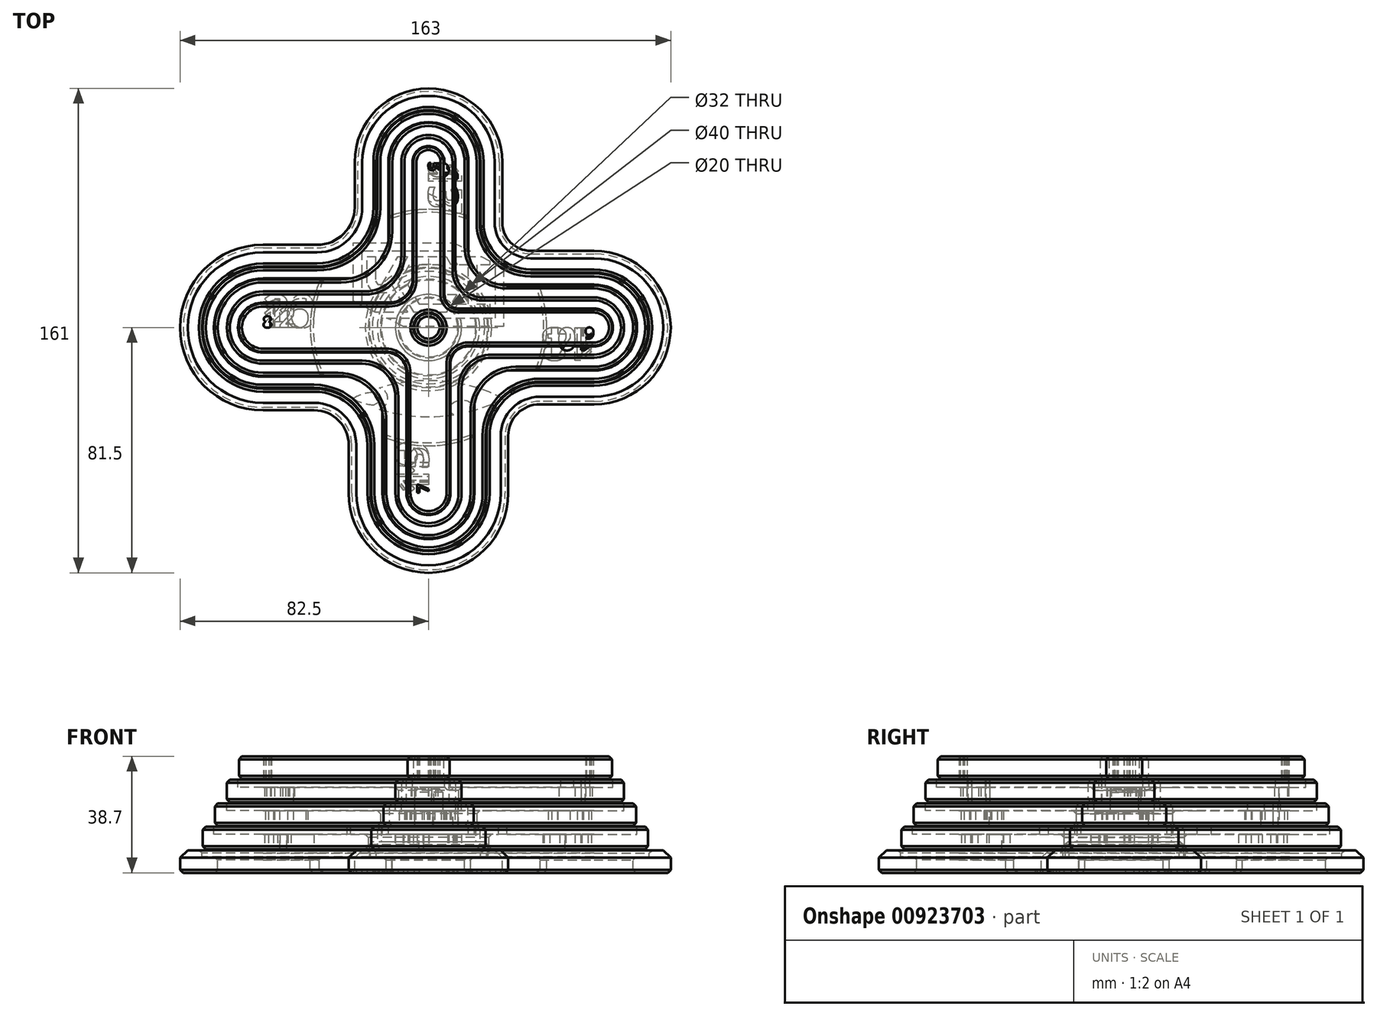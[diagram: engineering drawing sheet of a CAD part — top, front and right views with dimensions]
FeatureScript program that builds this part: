
annotation { "Feature Type Name" : "Feature", "Feature Type Description" : "" }
export const myFeature = defineFeature(function(context is Context, id is Id, definition is map)
    precondition{}
    {
        {
            assignVariable(context, id + "F0", {"name" : "x1", "anyValue" : 7.5});
        }
        {
            assignVariable(context, id + "F1", {"name" : "x2", "anyValue" : .3});
        }
        {
            assignVariable(context, id + "F2", {"name" : "x3", "anyValue" : 2.5});
        }
        {
            var Q0;
            Q0=qCreatedBy(makeId("Top.planeOp"),FACE);
            var sketch = newSketch(context, id + "F3", { "sketchPlane" : qUnion([Q0])});
            skLineSegment(sketch, "E0", {"start": v(-17, 55) * mm, "end": v(-17, 40) * mm});
            skLineSegment(sketch, "E1", {"start": v(-37, 20) * mm, "end": v(-55, 20) * mm});
            skLineSegment(sketch, "E2", {"start": v(-55, -20) * mm, "end": v(-38, -20) * mm});
            skLineSegment(sketch, "E3", {"start": v(-19, -39) * mm, "end": v(-19, -55) * mm});
            skLineSegment(sketch, "E4", {"start": v(19, -55) * mm, "end": v(19, -36) * mm});
            skLineSegment(sketch, "E5", {"start": v(37, -18) * mm, "end": v(55, -18) * mm});
            skLineSegment(sketch, "E6", {"start": v(55, 18) * mm, "end": v(34, 18) * mm});
            skLineSegment(sketch, "E7", {"start": v(17, 35) * mm, "end": v(17, 55) * mm});
            skArc(sketch, "E8", {"start": v(-55, 20) * mm, "mid": v(-75, 0) * mm, "end": v(-55, -20) * mm});
            skArc(sketch, "E9", {"start": v(-19, -55) * mm, "mid": v(0, -74) * mm, "end": v(19, -55) * mm});
            skArc(sketch, "E10", {"start": v(55, -18) * mm, "mid": v(73, 0) * mm, "end": v(55, 18) * mm});
            skArc(sketch, "E11", {"start": v(17, 55) * mm, "mid": v(0, 72) * mm, "end": v(-17, 55) * mm});
            skArc(sketch, "E12.filletArc", {"start": v(-37, 20) * mm, "mid": v(-22.86, 25.86) * mm, "end": v(-17, 40) * mm});
            skArc(sketch, "E13.filletArc", {"start": v(17, 35) * mm, "mid": v(21.98, 22.98) * mm, "end": v(34, 18) * mm});
            skArc(sketch, "E14.filletArc", {"start": v(37, -18) * mm, "mid": v(24.27, -23.27) * mm, "end": v(19, -36) * mm});
            skArc(sketch, "E15.filletArc", {"start": v(-19, -39) * mm, "mid": v(-24.56, -25.56) * mm, "end": v(-38, -20) * mm});
            skCircle(sketch, "E16", {"center": v(0, 0) * mm, "radius": 20 * mm});
            skText(sketch, "E17", { "text": "20\n", "fontName": "OpenSans-Bold.ttf"});
            skText(sketch, "E18", { "text": "19", "fontName": "OpenSans-Bold.ttf"});
            skText(sketch, "E19", { "text": "18", "fontName": "OpenSans-Bold.ttf"});
            skText(sketch, "E20", { "text": "17", "fontName": "OpenSans-Bold.ttf"});
            const initialGuessF3  = {"E17": [-0.055, 0, 1, 0, 0.01107], "E18": [0, -0.055, 0, 1, 0.01106], "E19": [0.055, 0, -1, 0, 0.01106], "E20": [0, 0.055, 0, -1, 0.01103]};
            skSetInitialGuess(sketch, initialGuessF3);
            skSolve(sketch);
        }
        {
            var Q0;
            Q0=makeQuery(id+"F3.imprint","IMPRINT",FACE,{"disambiguationData":[TD([[makeQuery(id+"F3.imprint","IMPRINT",EDGE,{"derivedFrom":sQuery(id+"F3.wireOp",EDGE,"E0")}),1.0]])]});
            extrude(context, id + "F4", {"entities" : qUnion([Q0]), "depth" : (getVariable(context, 'x1')) * mm, "offsetDistance" : 25 * mm});
        }
        {
            var Q0;
            Q0=makeQuery(id+"F4.opExtrude","CAP_FACE",FACE,{"disambiguationData":[OSD([sQuery(id+"F3.wireOp",EDGE,"E0"),sQuery(id+"F3.wireOp",EDGE,"E1"),sQuery(id+"F3.wireOp",EDGE,"E2"),sQuery(id+"F3.wireOp",EDGE,"E3"),sQuery(id+"F3.wireOp",EDGE,"E4"),sQuery(id+"F3.wireOp",EDGE,"E5"),sQuery(id+"F3.wireOp",EDGE,"E6"),sQuery(id+"F3.wireOp",EDGE,"E7"),sQuery(id+"F3.wireOp",EDGE,"E8"),sQuery(id+"F3.wireOp",EDGE,"E9"),sQuery(id+"F3.wireOp",EDGE,"E10"),sQuery(id+"F3.wireOp",EDGE,"E11"),sQuery(id+"F3.wireOp",EDGE,"E12.filletArc"),sQuery(id+"F3.wireOp",EDGE,"E13.filletArc"),sQuery(id+"F3.wireOp",EDGE,"E14.filletArc"),sQuery(id+"F3.wireOp",EDGE,"E15.filletArc"),sQuery(id+"F3.wireOp",EDGE,"E16")])],"isStart":false});
            cPlane(context, id + "F5", {"entities" : qUnion([Q0]), "cplaneType" : CPlaneType.OFFSET, "offset" : (getVariable(context, 'x2')) * mm, "width" : 150 * mm, "height" : 150 * mm});
        }
        {
            var Q0;
            Q0=qCreatedBy(id+"F5.planeOp",FACE);
            var sketch = newSketch(context, id + "F6", { "sketchPlane" : qUnion([Q0])});
            skLineSegment(sketch, "E21", {"start": v(-13, 55) * mm, "end": v(-13, 32) * mm});
            skLineSegment(sketch, "E22", {"start": v(-29, 16) * mm, "end": v(-55, 16) * mm});
            skLineSegment(sketch, "E23", {"start": v(-55, -16) * mm, "end": v(-30, -16) * mm});
            skLineSegment(sketch, "E24", {"start": v(-15, -31) * mm, "end": v(-15, -55) * mm});
            skLineSegment(sketch, "E25", {"start": v(15, -55) * mm, "end": v(15, -28) * mm});
            skLineSegment(sketch, "E26", {"start": v(29, -14) * mm, "end": v(55, -14) * mm});
            skLineSegment(sketch, "E27", {"start": v(55, 14) * mm, "end": v(26, 14) * mm});
            skLineSegment(sketch, "E28", {"start": v(13, 27) * mm, "end": v(13, 55) * mm});
            skArc(sketch, "E29", {"start": v(-55, 16) * mm, "mid": v(-71, 0) * mm, "end": v(-55, -16) * mm});
            skArc(sketch, "E30", {"start": v(-15, -55) * mm, "mid": v(0, -70) * mm, "end": v(15, -55) * mm});
            skArc(sketch, "E31", {"start": v(55, -14) * mm, "mid": v(69, 0) * mm, "end": v(55, 14) * mm});
            skArc(sketch, "E32", {"start": v(13, 55) * mm, "mid": v(0, 68) * mm, "end": v(-13, 55) * mm});
            skPoint(sketch, "E33.visualSharp", {"position": v(-13, 16) * mm});
            skArc(sketch, "E33.filletArc", {"start": v(-29, 16) * mm, "mid": v(-17.69, 20.69) * mm, "end": v(-13, 32) * mm});
            skPoint(sketch, "E34.visualSharp", {"position": v(13, 14) * mm});
            skArc(sketch, "E34.filletArc", {"start": v(13, 27) * mm, "mid": v(16.8, 17.8) * mm, "end": v(26, 14) * mm});
            skPoint(sketch, "E35.visualSharp", {"position": v(15, -14) * mm});
            skArc(sketch, "E35.filletArc", {"start": v(29, -14) * mm, "mid": v(19.1, -18.1) * mm, "end": v(15, -28) * mm});
            skPoint(sketch, "E36.visualSharp", {"position": v(-15, -16) * mm});
            skArc(sketch, "E36.filletArc", {"start": v(-15, -31) * mm, "mid": v(-19.4, -20.4) * mm, "end": v(-30, -16) * mm});
            skCircle(sketch, "E37", {"center": v(0, 0) * mm, "radius": 16 * mm});
            skText(sketch, "E38", { "text": "13\n", "fontName": "OpenSans-Bold.ttf"});
            skLineSegment(sketch, "E39", {"start": v(0, 27) * mm, "end": v(6.5, 27) * mm, "construction": true});
            skLineSegment(sketch, "E40", {"start": v(6.5, 27) * mm, "end": v(13, 27) * mm, "construction": true});
            skPoint(sketch, "E41", {"position": v(9.75, 27) * mm});
            skText(sketch, "E42", { "text": "16", "fontName": "OpenSans-Bold.ttf"});
            skText(sketch, "E43", { "text": "15", "fontName": "OpenSans-Bold.ttf"});
            skText(sketch, "E44", { "text": "14\n", "fontName": "OpenSans-Bold.ttf"});
            const initialGuessF6  = {"E38": [0, 0.055, 0, -1, 0.00975], "E42": [-0.055, 0, 1, 0, 0.0097], "E43": [0, -0.055, 0, 1, 0.0098], "E44": [0.055, 0, -1, 0, 0.00975]};
            skSetInitialGuess(sketch, initialGuessF6);
            skSolve(sketch);
        }
        {
            var Q0;
            Q0=makeQuery(id+"F6.imprint","IMPRINT",FACE,{"disambiguationData":[TD([[makeQuery(id+"F6.imprint","IMPRINT",EDGE,{"derivedFrom":sQuery(id+"F6.wireOp",EDGE,"E21")}),1.0]])]});
            extrude(context, id + "F7", {"entities" : qUnion([Q0]), "depth" : (getVariable(context, 'x1')) * mm, "offsetDistance" : 25 * mm});
        }
        {
            var Q0;
            Q0=makeQuery(id+"F7.opExtrude","CAP_FACE",FACE,{"disambiguationData":[OSD([sQuery(id+"F6.wireOp",EDGE,"E21"),sQuery(id+"F6.wireOp",EDGE,"E22"),sQuery(id+"F6.wireOp",EDGE,"E23"),sQuery(id+"F6.wireOp",EDGE,"E24"),sQuery(id+"F6.wireOp",EDGE,"E25"),sQuery(id+"F6.wireOp",EDGE,"E26"),sQuery(id+"F6.wireOp",EDGE,"E27"),sQuery(id+"F6.wireOp",EDGE,"E28"),sQuery(id+"F6.wireOp",EDGE,"E29"),sQuery(id+"F6.wireOp",EDGE,"E30"),sQuery(id+"F6.wireOp",EDGE,"E31"),sQuery(id+"F6.wireOp",EDGE,"E32"),sQuery(id+"F6.wireOp",EDGE,"E33.filletArc"),sQuery(id+"F6.wireOp",EDGE,"E34.filletArc"),sQuery(id+"F6.wireOp",EDGE,"E35.filletArc"),sQuery(id+"F6.wireOp",EDGE,"E36.filletArc"),sQuery(id+"F6.wireOp",EDGE,"E37")])],"isStart":false});
            cPlane(context, id + "F8", {"entities" : qUnion([Q0]), "cplaneType" : CPlaneType.OFFSET, "offset" : (getVariable(context, 'x2')) * mm, "width" : 150 * mm, "height" : 150 * mm});
        }
        {
            var Q0;
            Q0=qCreatedBy(id+"F8.planeOp",FACE);
            var sketch = newSketch(context, id + "F9", { "sketchPlane" : qUnion([Q0])});
            skLineSegment(sketch, "E45", {"start": v(-55, 12) * mm, "end": v(-21, 12) * mm});
            skLineSegment(sketch, "E46", {"start": v(-9, 24) * mm, "end": v(-9, 55) * mm});
            skLineSegment(sketch, "E47", {"start": v(9, 55) * mm, "end": v(9, 19) * mm});
            skLineSegment(sketch, "E48", {"start": v(18, 10) * mm, "end": v(55, 10) * mm});
            skLineSegment(sketch, "E49", {"start": v(55, -10) * mm, "end": v(21, -10) * mm});
            skLineSegment(sketch, "E50", {"start": v(11, -20) * mm, "end": v(11, -55) * mm});
            skLineSegment(sketch, "E51", {"start": v(-11, -55) * mm, "end": v(-11, -23) * mm});
            skLineSegment(sketch, "E52", {"start": v(-22, -12) * mm, "end": v(-55, -12) * mm});
            skArc(sketch, "E53", {"start": v(-55, 12) * mm, "mid": v(-67, 0) * mm, "end": v(-55, -12) * mm});
            skArc(sketch, "E54", {"start": v(9, 55) * mm, "mid": v(0, 64) * mm, "end": v(-9, 55) * mm});
            skArc(sketch, "E55", {"start": v(55, -10) * mm, "mid": v(65, 0) * mm, "end": v(55, 10) * mm});
            skArc(sketch, "E56", {"start": v(-11, -55) * mm, "mid": v(0, -66) * mm, "end": v(11, -55) * mm});
            skPoint(sketch, "E57.visualSharp", {"position": v(-9, 12) * mm});
            skArc(sketch, "E57.filletArc", {"start": v(-21, 12) * mm, "mid": v(-12.51, 15.51) * mm, "end": v(-9, 24) * mm});
            skPoint(sketch, "E58.visualSharp", {"position": v(9, 10) * mm});
            skArc(sketch, "E58.filletArc", {"start": v(9, 19) * mm, "mid": v(11.64, 12.64) * mm, "end": v(18, 10) * mm});
            skPoint(sketch, "E59.visualSharp", {"position": v(11, -10) * mm});
            skArc(sketch, "E59.filletArc", {"start": v(21, -10) * mm, "mid": v(13.93, -12.93) * mm, "end": v(11, -20) * mm});
            skPoint(sketch, "E60.visualSharp", {"position": v(-11, -12) * mm});
            skArc(sketch, "E60.filletArc", {"start": v(-11, -23) * mm, "mid": v(-14.22, -15.22) * mm, "end": v(-22, -12) * mm});
            skCircle(sketch, "E61", {"center": v(0, 0) * mm, "radius": 10 * mm});
            skText(sketch, "E62", { "text": "9\n", "fontName": "OpenSans-Bold.ttf"});
            skLineSegment(sketch, "E63", {"start": v(0, 19) * mm, "end": v(4.5, 19) * mm, "construction": true});
            skLineSegment(sketch, "E64", {"start": v(4.5, 19) * mm, "end": v(9, 19) * mm, "construction": true});
            skPoint(sketch, "E65", {"position": v(6.75, 19) * mm});
            skText(sketch, "E66", { "text": "12", "fontName": "OpenSans-Bold.ttf"});
            skText(sketch, "E67", { "text": "11\n", "fontName": "OpenSans-Bold.ttf"});
            skText(sketch, "E68", { "text": "10", "fontName": "OpenSans-Bold.ttf"});
            const initialGuessF9  = {"E62": [0, 0.055, 0, -1, 0.00675], "E66": [-0.055, 0, 1, 0, 0.00675], "E67": [0, -0.055, 0, 1, 0.00756], "E68": [0.055, 0, -1, 0, 0.00756]};
            skSetInitialGuess(sketch, initialGuessF9);
            skSolve(sketch);
        }
        {
            var Q0;
            Q0=makeQuery(id+"F9.imprint","IMPRINT",FACE,{"disambiguationData":[TD([[makeQuery(id+"F9.imprint","IMPRINT",EDGE,{"derivedFrom":sQuery(id+"F9.wireOp",EDGE,"E45")}),-1.0]])]});
            extrude(context, id + "F10", {"entities" : qUnion([Q0]), "depth" : (getVariable(context, 'x1')) * mm, "offsetDistance" : 25 * mm});
        }
        {
            var Q0;
            Q0=makeQuery(id+"F10.opExtrude","CAP_FACE",FACE,{"disambiguationData":[OSD([sQuery(id+"F9.wireOp",EDGE,"E45"),sQuery(id+"F9.wireOp",EDGE,"E46"),sQuery(id+"F9.wireOp",EDGE,"E47"),sQuery(id+"F9.wireOp",EDGE,"E48"),sQuery(id+"F9.wireOp",EDGE,"E49"),sQuery(id+"F9.wireOp",EDGE,"E50"),sQuery(id+"F9.wireOp",EDGE,"E51"),sQuery(id+"F9.wireOp",EDGE,"E52"),sQuery(id+"F9.wireOp",EDGE,"E53"),sQuery(id+"F9.wireOp",EDGE,"E54"),sQuery(id+"F9.wireOp",EDGE,"E55"),sQuery(id+"F9.wireOp",EDGE,"E56"),sQuery(id+"F9.wireOp",EDGE,"E57.filletArc"),sQuery(id+"F9.wireOp",EDGE,"E58.filletArc"),sQuery(id+"F9.wireOp",EDGE,"E59.filletArc"),sQuery(id+"F9.wireOp",EDGE,"E60.filletArc"),sQuery(id+"F9.wireOp",EDGE,"E61"),sQuery(id+"F9.wireOp",EDGE,"E62.sketch_text.stroke-0"),sQuery(id+"F9.wireOp",EDGE,"E62.sketch_text.stroke-1"),sQuery(id+"F9.wireOp",EDGE,"E62.sketch_text.stroke-2"),sQuery(id+"F9.wireOp",EDGE,"E62.sketch_text.stroke-3"),sQuery(id+"F9.wireOp",EDGE,"E62.sketch_text.stroke-4"),sQuery(id+"F9.wireOp",EDGE,"E62.sketch_text.stroke-5"),sQuery(id+"F9.wireOp",EDGE,"E62.sketch_text.stroke-6"),sQuery(id+"F9.wireOp",EDGE,"E62.sketch_text.stroke-7"),sQuery(id+"F9.wireOp",EDGE,"E62.sketch_text.stroke-8"),sQuery(id+"F9.wireOp",EDGE,"E62.sketch_text.stroke-9"),sQuery(id+"F9.wireOp",EDGE,"E62.sketch_text.stroke-10"),sQuery(id+"F9.wireOp",EDGE,"E62.sketch_text.stroke-11"),sQuery(id+"F9.wireOp",EDGE,"E62.sketch_text.stroke-12"),sQuery(id+"F9.wireOp",EDGE,"E62.sketch_text.stroke-13"),sQuery(id+"F9.wireOp",EDGE,"E62.sketch_text.stroke-14"),sQuery(id+"F9.wireOp",EDGE,"E62.sketch_text.stroke-15"),sQuery(id+"F9.wireOp",EDGE,"E62.sketch_text.stroke-16"),sQuery(id+"F9.wireOp",EDGE,"E62.sketch_text.stroke-17"),sQuery(id+"F9.wireOp",EDGE,"E66.sketch_text.stroke-0"),sQuery(id+"F9.wireOp",EDGE,"E66.sketch_text.stroke-1"),sQuery(id+"F9.wireOp",EDGE,"E66.sketch_text.stroke-2"),sQuery(id+"F9.wireOp",EDGE,"E66.sketch_text.stroke-3"),sQuery(id+"F9.wireOp",EDGE,"E66.sketch_text.stroke-4"),sQuery(id+"F9.wireOp",EDGE,"E66.sketch_text.stroke-5"),sQuery(id+"F9.wireOp",EDGE,"E66.sketch_text.stroke-6"),sQuery(id+"F9.wireOp",EDGE,"E66.sketch_text.stroke-7"),sQuery(id+"F9.wireOp",EDGE,"E66.sketch_text.stroke-8"),sQuery(id+"F9.wireOp",EDGE,"E66.sketch_text.stroke-9"),sQuery(id+"F9.wireOp",EDGE,"E66.sketch_text.stroke-10"),sQuery(id+"F9.wireOp",EDGE,"E66.sketch_text.stroke-11"),sQuery(id+"F9.wireOp",EDGE,"E66.sketch_text.stroke-12"),sQuery(id+"F9.wireOp",EDGE,"E66.sketch_text.stroke-13"),sQuery(id+"F9.wireOp",EDGE,"E66.sketch_text.stroke-14"),sQuery(id+"F9.wireOp",EDGE,"E66.sketch_text.stroke-15"),sQuery(id+"F9.wireOp",EDGE,"E66.sketch_text.stroke-16"),sQuery(id+"F9.wireOp",EDGE,"E66.sketch_text.stroke-17"),sQuery(id+"F9.wireOp",EDGE,"E66.sketch_text.stroke-18"),sQuery(id+"F9.wireOp",EDGE,"E66.sketch_text.stroke-19"),sQuery(id+"F9.wireOp",EDGE,"E66.sketch_text.stroke-20"),sQuery(id+"F9.wireOp",EDGE,"E66.sketch_text.stroke-21"),sQuery(id+"F9.wireOp",EDGE,"E66.sketch_text.stroke-22"),sQuery(id+"F9.wireOp",EDGE,"E66.sketch_text.stroke-23"),sQuery(id+"F9.wireOp",EDGE,"E66.sketch_text.stroke-24"),sQuery(id+"F9.wireOp",EDGE,"E66.sketch_text.stroke-25"),sQuery(id+"F9.wireOp",EDGE,"E66.sketch_text.stroke-26"),sQuery(id+"F9.wireOp",EDGE,"E66.sketch_text.stroke-27"),sQuery(id+"F9.wireOp",EDGE,"E66.sketch_text.stroke-28"),sQuery(id+"F9.wireOp",EDGE,"E66.sketch_text.stroke-29"),sQuery(id+"F9.wireOp",EDGE,"E66.sketch_text.stroke-30"),sQuery(id+"F9.wireOp",EDGE,"E66.sketch_text.stroke-31"),sQuery(id+"F9.wireOp",EDGE,"E66.sketch_text.stroke-32"),sQuery(id+"F9.wireOp",EDGE,"E66.sketch_text.stroke-33"),sQuery(id+"F9.wireOp",EDGE,"E67.sketch_text.stroke-0"),sQuery(id+"F9.wireOp",EDGE,"E67.sketch_text.stroke-1"),sQuery(id+"F9.wireOp",EDGE,"E67.sketch_text.stroke-2"),sQuery(id+"F9.wireOp",EDGE,"E67.sketch_text.stroke-3"),sQuery(id+"F9.wireOp",EDGE,"E67.sketch_text.stroke-4"),sQuery(id+"F9.wireOp",EDGE,"E67.sketch_text.stroke-5"),sQuery(id+"F9.wireOp",EDGE,"E67.sketch_text.stroke-6"),sQuery(id+"F9.wireOp",EDGE,"E67.sketch_text.stroke-7"),sQuery(id+"F9.wireOp",EDGE,"E67.sketch_text.stroke-8"),sQuery(id+"F9.wireOp",EDGE,"E67.sketch_text.stroke-9"),sQuery(id+"F9.wireOp",EDGE,"E67.sketch_text.stroke-10"),sQuery(id+"F9.wireOp",EDGE,"E67.sketch_text.stroke-11"),sQuery(id+"F9.wireOp",EDGE,"E67.sketch_text.stroke-12"),sQuery(id+"F9.wireOp",EDGE,"E67.sketch_text.stroke-13"),sQuery(id+"F9.wireOp",EDGE,"E67.sketch_text.stroke-14"),sQuery(id+"F9.wireOp",EDGE,"E67.sketch_text.stroke-15"),sQuery(id+"F9.wireOp",EDGE,"E67.sketch_text.stroke-16"),sQuery(id+"F9.wireOp",EDGE,"E67.sketch_text.stroke-17"),sQuery(id+"F9.wireOp",EDGE,"E67.sketch_text.stroke-18"),sQuery(id+"F9.wireOp",EDGE,"E67.sketch_text.stroke-19"),sQuery(id+"F9.wireOp",EDGE,"E68.sketch_text.stroke-0"),sQuery(id+"F9.wireOp",EDGE,"E68.sketch_text.stroke-1"),sQuery(id+"F9.wireOp",EDGE,"E68.sketch_text.stroke-2"),sQuery(id+"F9.wireOp",EDGE,"E68.sketch_text.stroke-3"),sQuery(id+"F9.wireOp",EDGE,"E68.sketch_text.stroke-4"),sQuery(id+"F9.wireOp",EDGE,"E68.sketch_text.stroke-5"),sQuery(id+"F9.wireOp",EDGE,"E68.sketch_text.stroke-6"),sQuery(id+"F9.wireOp",EDGE,"E68.sketch_text.stroke-7"),sQuery(id+"F9.wireOp",EDGE,"E68.sketch_text.stroke-8"),sQuery(id+"F9.wireOp",EDGE,"E68.sketch_text.stroke-9"),sQuery(id+"F9.wireOp",EDGE,"E68.sketch_text.stroke-10"),sQuery(id+"F9.wireOp",EDGE,"E68.sketch_text.stroke-11"),sQuery(id+"F9.wireOp",EDGE,"E68.sketch_text.stroke-12"),sQuery(id+"F9.wireOp",EDGE,"E68.sketch_text.stroke-13"),sQuery(id+"F9.wireOp",EDGE,"E68.sketch_text.stroke-14"),sQuery(id+"F9.wireOp",EDGE,"E68.sketch_text.stroke-15"),sQuery(id+"F9.wireOp",EDGE,"E68.sketch_text.stroke-16"),sQuery(id+"F9.wireOp",EDGE,"E68.sketch_text.stroke-17")])],"isStart":false});
            cPlane(context, id + "F11", {"entities" : qUnion([Q0]), "cplaneType" : CPlaneType.OFFSET, "offset" : (getVariable(context, 'x2')) * mm, "width" : 150 * mm, "height" : 150 * mm});
        }
        {
            var Q0;
            Q0=qCreatedBy(id+"F11.planeOp",FACE);
            var sketch = newSketch(context, id + "F12", { "sketchPlane" : qUnion([Q0])});
            skLineSegment(sketch, "E69", {"start": v(-5, 55) * mm, "end": v(-5, 16) * mm});
            skLineSegment(sketch, "E70", {"start": v(-13, 8) * mm, "end": v(-55, 8) * mm});
            skLineSegment(sketch, "E71", {"start": v(-55, -8) * mm, "end": v(-14, -8) * mm});
            skLineSegment(sketch, "E72", {"start": v(-7, -15) * mm, "end": v(-7, -55) * mm});
            skLineSegment(sketch, "E73", {"start": v(7, -55) * mm, "end": v(7, -12) * mm});
            skLineSegment(sketch, "E74", {"start": v(13, -6) * mm, "end": v(55, -6) * mm});
            skLineSegment(sketch, "E75", {"start": v(55, 6) * mm, "end": v(10, 6) * mm});
            skLineSegment(sketch, "E76", {"start": v(5, 11) * mm, "end": v(5, 55) * mm});
            skArc(sketch, "E77", {"start": v(-55, 8) * mm, "mid": v(-63, 0) * mm, "end": v(-55, -8) * mm});
            skArc(sketch, "E78", {"start": v(-7, -55) * mm, "mid": v(0, -62) * mm, "end": v(7, -55) * mm});
            skArc(sketch, "E79", {"start": v(55, -6) * mm, "mid": v(61, 0) * mm, "end": v(55, 6) * mm});
            skArc(sketch, "E80", {"start": v(5, 55) * mm, "mid": v(0, 60) * mm, "end": v(-5, 55) * mm});
            skPoint(sketch, "E81.visualSharp", {"position": v(-5, 8) * mm});
            skArc(sketch, "E81.filletArc", {"start": v(-13, 8) * mm, "mid": v(-7.34, 10.34) * mm, "end": v(-5, 16) * mm});
            skPoint(sketch, "E82.visualSharp", {"position": v(5, 6) * mm});
            skArc(sketch, "E82.filletArc", {"start": v(5, 11) * mm, "mid": v(6.46, 7.46) * mm, "end": v(10, 6) * mm});
            skPoint(sketch, "E83.visualSharp", {"position": v(7, -6) * mm});
            skArc(sketch, "E83.filletArc", {"start": v(13, -6) * mm, "mid": v(8.76, -7.76) * mm, "end": v(7, -12) * mm});
            skPoint(sketch, "E84.visualSharp", {"position": v(-7, -8) * mm});
            skArc(sketch, "E84.filletArc", {"start": v(-7, -15) * mm, "mid": v(-9.05, -10.05) * mm, "end": v(-14, -8) * mm});
            skCircle(sketch, "E85", {"center": v(0, 0) * mm, "radius": 5 * mm});
            skText(sketch, "E86", { "text": "5", "fontName": "OpenSans-Bold.ttf"});
            skLineSegment(sketch, "E87", {"start": v(5, 11) * mm, "end": v(2.5, 11) * mm, "construction": true});
            skLineSegment(sketch, "E88", {"start": v(2.5, 11) * mm, "end": v(0, 11) * mm, "construction": true});
            skPoint(sketch, "E89", {"position": v(3.75, 11) * mm});
            skText(sketch, "E90", { "text": "8", "fontName": "OpenSans-Bold.ttf"});
            skText(sketch, "E91", { "text": "7", "fontName": "OpenSans-Bold.ttf"});
            skText(sketch, "E92", { "text": "6", "fontName": "OpenSans-Bold.ttf"});
            const initialGuessF12  = {"E86": [0, 0.055, 0, -1, 0.00375], "E90": [-0.055, 0, 1, 0, 0.00375], "E91": [0, -0.055, 0, 1, 0.00375], "E92": [0.055, 0, -1, 0, 0.00375]};
            skSetInitialGuess(sketch, initialGuessF12);
            skSolve(sketch);
        }
        {
            var Q0;
            Q0=makeQuery(id+"F12.imprint","IMPRINT",FACE,{"disambiguationData":[TD([[makeQuery(id+"F12.imprint","IMPRINT",EDGE,{"derivedFrom":sQuery(id+"F12.wireOp",EDGE,"E69")}),1.0]])]});
            extrude(context, id + "F13", {"entities" : qUnion([Q0]), "depth" : (getVariable(context, 'x1')) * mm, "offsetDistance" : 25 * mm});
        }
        {
            var Q0;
            Q0=qCreatedBy(makeId("Top.planeOp"),FACE);
            cPlane(context, id + "F14", {"entities" : qUnion([Q0]), "cplaneType" : CPlaneType.OFFSET, "offset" : (getVariable(context, 'x2')) * mm, "oppositeDirection" : true, "width" : 150 * mm, "height" : 150 * mm});
        }
        {
            var Q0;
            Q0=qCreatedBy(id+"F14.planeOp",FACE);
            var sketch = newSketch(context, id + "F15", { "sketchPlane" : qUnion([Q0])});
            skLineSegment(sketch, "E93.0", {"start": v(46, 0) * mm, "end": v(46, -11.06) * mm});
            skLineSegment(sketch, "E93.1", {"start": v(-55, 0) * mm, "end": v(-55, 11.07) * mm});
            skCircle(sketch, "E93.3", {"center": v(0, 0) * mm, "radius": 20 * mm, "construction": true});
            skLineSegment(sketch, "E93.4", {"start": v(0, -55) * mm, "end": v(-11.06, -55) * mm});
            skLineSegment(sketch, "E93.5", {"start": v(0, 55) * mm, "end": v(0, 37) * mm});
            skArc(sketch, "E93.6", {"start": v(-19, -39) * mm, "mid": v(-19.17, -36.49) * mm, "end": v(-19.66, -34.02) * mm, "construction": true});
            skArc(sketch, "E93.7", {"start": v(17, 35) * mm, "mid": v(21.98, 22.98) * mm, "end": v(34, 18) * mm, "construction": true});
            skArc(sketch, "E93.8", {"start": v(37, -18) * mm, "mid": v(35.93, -18.03) * mm, "end": v(34.86, -18.13) * mm, "construction": true});
            skLineSegment(sketch, "E93.9", {"start": v(-17, 55) * mm, "end": v(-17, 40) * mm, "construction": true});
            skLineSegment(sketch, "E93.10", {"start": v(-37, 20) * mm, "end": v(-55, 20) * mm, "construction": true});
            skLineSegment(sketch, "E93.11", {"start": v(-55, -20) * mm, "end": v(-38, -20) * mm, "construction": true});
            skLineSegment(sketch, "E93.12", {"start": v(-19, -39) * mm, "end": v(-19, -55) * mm, "construction": true});
            skLineSegment(sketch, "E93.13", {"start": v(19, -55) * mm, "end": v(19, -36) * mm, "construction": true});
            skLineSegment(sketch, "E93.14", {"start": v(37, -18) * mm, "end": v(55, -18) * mm, "construction": true});
            skLineSegment(sketch, "E93.15", {"start": v(55, 18) * mm, "end": v(34, 18) * mm, "construction": true});
            skLineSegment(sketch, "E93.16", {"start": v(17, 35) * mm, "end": v(17, 55) * mm, "construction": true});
            skArc(sketch, "E93.17", {"start": v(-55, 20) * mm, "mid": v(-75, 0) * mm, "end": v(-55, -20) * mm, "construction": true});
            skArc(sketch, "E93.18", {"start": v(-19, -55) * mm, "mid": v(0, -74) * mm, "end": v(19, -55) * mm, "construction": true});
            skArc(sketch, "E93.19", {"start": v(55, -18) * mm, "mid": v(73, 0) * mm, "end": v(55, 18) * mm, "construction": true});
            skArc(sketch, "E93.20", {"start": v(17, 55) * mm, "mid": v(0, 72) * mm, "end": v(-17, 55) * mm, "construction": true});
            skArc(sketch, "E93.21", {"start": v(-37, 20) * mm, "mid": v(-35.32, 20.07) * mm, "end": v(-33.66, 20.28) * mm, "construction": true});
            skLineSegment(sketch, "E93.22", {"start": v(0, 55) * mm, "end": v(11.03, 55) * mm});
            skLineSegment(sketch, "E93.23", {"start": v(55, 0) * mm, "end": v(37, 0) * mm});
            skLineSegment(sketch, "E93.24", {"start": v(0, 46) * mm, "end": v(11.03, 46) * mm});
            skLineSegment(sketch, "E93.25", {"start": v(55, -11.06) * mm, "end": v(37, -11.06) * mm});
            skLineSegment(sketch, "E93.26", {"start": v(0, -46) * mm, "end": v(-11.06, -46) * mm});
            skLineSegment(sketch, "E93.28", {"start": v(55, 0) * mm, "end": v(55, -11.06) * mm});
            skLineSegment(sketch, "E93.29", {"start": v(-55, 11.07) * mm, "end": v(-37, 11.07) * mm});
            skLineSegment(sketch, "E93.30", {"start": v(0, -37) * mm, "end": v(-11.06, -37) * mm});
            skLineSegment(sketch, "E93.31", {"start": v(-37, 0) * mm, "end": v(-37, 11.07) * mm});
            skLineSegment(sketch, "E93.32", {"start": v(0, -55) * mm, "end": v(0, -37) * mm});
            skLineSegment(sketch, "E93.33", {"start": v(11.03, 55) * mm, "end": v(11.03, 37) * mm});
            skLineSegment(sketch, "E94.0", {"start": v(-37, 27.5) * mm, "end": v(-55, 27.5) * mm});
            skArc(sketch, "E94.1", {"start": v(-37, 27.5) * mm, "mid": v(-28.16, 31.16) * mm, "end": v(-24.5, 40) * mm});
            skLineSegment(sketch, "E94.2", {"start": v(-24.5, 55) * mm, "end": v(-24.5, 40) * mm});
            skArc(sketch, "E94.3", {"start": v(24.5, 55) * mm, "mid": v(0, 79.5) * mm, "end": v(-24.5, 55) * mm});
            skLineSegment(sketch, "E94.4", {"start": v(24.5, 35) * mm, "end": v(24.5, 55) * mm});
            skArc(sketch, "E94.5", {"start": v(-26.5, -55) * mm, "mid": v(0, -81.5) * mm, "end": v(26.5, -55) * mm});
            skLineSegment(sketch, "E94.6", {"start": v(-26.5, -39) * mm, "end": v(-26.5, -55) * mm});
            skArc(sketch, "E94.7", {"start": v(-26.5, -39) * mm, "mid": v(-29.87, -30.87) * mm, "end": v(-38, -27.5) * mm});
            skLineSegment(sketch, "E94.8", {"start": v(-55, -27.5) * mm, "end": v(-38, -27.5) * mm});
            skLineSegment(sketch, "E94.9", {"start": v(26.5, -55) * mm, "end": v(26.5, -36) * mm});
            skArc(sketch, "E94.10", {"start": v(37, -25.5) * mm, "mid": v(29.58, -28.58) * mm, "end": v(26.5, -36) * mm});
            skLineSegment(sketch, "E94.11", {"start": v(37, -25.5) * mm, "end": v(55, -25.5) * mm});
            skArc(sketch, "E94.12", {"start": v(55, -25.5) * mm, "mid": v(80.5, 0) * mm, "end": v(55, 25.5) * mm});
            skLineSegment(sketch, "E94.13", {"start": v(55, 25.5) * mm, "end": v(34, 25.5) * mm});
            skArc(sketch, "E94.14", {"start": v(-55, 27.5) * mm, "mid": v(-82.5, 0) * mm, "end": v(-55, -27.5) * mm});
            skArc(sketch, "E94.15", {"start": v(24.5, 35) * mm, "mid": v(27.28, 28.28) * mm, "end": v(34, 25.5) * mm});
            skArc(sketch, "E95.0", {"start": v(17, 35.43) * mm, "mid": v(-0.33, 39.3) * mm, "end": v(-17.6, 35.13) * mm});
            skArc(sketch, "E96.trimOffspring", {"start": v(-33.66, 20.28) * mm, "mid": v(-39.3, -0.15) * mm, "end": v(-33.5, -20.54) * mm});
            skArc(sketch, "E97.trimOffspring", {"start": v(-17.6, 35.13) * mm, "mid": v(-17.15, 37.55) * mm, "end": v(-17, 40) * mm, "construction": true});
            skArc(sketch, "E98.trimOffspring", {"start": v(-19.66, -34.02) * mm, "mid": v(-0.34, -39.3) * mm, "end": v(19.08, -34.36) * mm});
            skArc(sketch, "E99.trimOffspring", {"start": v(-33.5, -20.54) * mm, "mid": v(-35.73, -20.14) * mm, "end": v(-38, -20) * mm, "construction": true});
            skArc(sketch, "E100.trimOffspring", {"start": v(34.86, -18.13) * mm, "mid": v(39.3, -0.07) * mm, "end": v(34.93, 18) * mm});
            skArc(sketch, "E101.trimOffspring", {"start": v(19.08, -34.36) * mm, "mid": v(19.02, -35.18) * mm, "end": v(19, -36) * mm});
            skPoint(sketch, "E93.27.end.orphan", {"position": v(11.03, 37) * mm});
            skPoint(sketch, "E93.27.start.orphan", {"position": v(0, 37) * mm});
            skPoint(sketch, "E93.2.end.orphan", {"position": v(37, -11.06) * mm});
            skPoint(sketch, "E93.2.start.orphan", {"position": v(37, 0) * mm});
            skArc(sketch, "E102.0", {"start": v(-36.3, -15.06) * mm, "mid": v(-37.15, -15.02) * mm, "end": v(-38, -15) * mm});
            skArc(sketch, "E102.1", {"start": v(-37, 15) * mm, "mid": v(-36.66, 15) * mm, "end": v(-36.32, 15) * mm});
            skLineSegment(sketch, "E102.2", {"start": v(-37, 15) * mm, "end": v(-55, 15) * mm});
            skArc(sketch, "E102.3", {"start": v(-55, 15) * mm, "mid": v(-70, 0) * mm, "end": v(-55, -15) * mm});
            skLineSegment(sketch, "E102.4", {"start": v(-55, -15) * mm, "end": v(-38, -15) * mm});
            skArc(sketch, "E103.0", {"start": v(-14, -39) * mm, "mid": v(-14.03, -37.84) * mm, "end": v(-14.11, -36.67) * mm});
            skArc(sketch, "E103.1", {"start": v(14.1, -33.9) * mm, "mid": v(14.02, -34.95) * mm, "end": v(14, -36) * mm, "construction": true});
            skLineSegment(sketch, "E103.2", {"start": v(14, -55) * mm, "end": v(14, -36.72) * mm});
            skArc(sketch, "E103.3", {"start": v(-14, -55) * mm, "mid": v(0, -69) * mm, "end": v(14, -55) * mm});
            skLineSegment(sketch, "E103.4", {"start": v(-14, -39) * mm, "end": v(-14, -55) * mm});
            skLineSegment(sketch, "E104.0", {"start": v(55, 13) * mm, "end": v(37.08, 13) * mm});
            skArc(sketch, "E104.1", {"start": v(55, -13) * mm, "mid": v(68, 0) * mm, "end": v(55, 13) * mm});
            skLineSegment(sketch, "E104.2", {"start": v(37.08, -13) * mm, "end": v(55, -13) * mm});
            skLineSegment(sketch, "E105.0", {"start": v(12, 37.42) * mm, "end": v(12, 55) * mm});
            skArc(sketch, "E105.1", {"start": v(12, 55) * mm, "mid": v(0, 67) * mm, "end": v(-12, 55) * mm});
            skLineSegment(sketch, "E105.2", {"start": v(-12, 55) * mm, "end": v(-12, 40) * mm});
            skArc(sketch, "E105.3", {"start": v(-12.14, 37.37) * mm, "mid": v(-12.03, 38.69) * mm, "end": v(-12, 40) * mm});
            skSolve(sketch);
        }
        {
            var Q0;
            Q0 = qSketchRegion(id + "F15", true);
            extrude(context, id + "F16", {"entities" : qUnion([Q0]), "oppositeDirection" : true, "depth" : (getVariable(context, 'x1')) * mm, "offsetDistance" : 25 * mm});
        }
        {
            var Q0;
            Q0=makeQuery(id+"F3.imprint","IMPRINT",FACE,{"disambiguationData":[TD([[makeQuery(id+"F3.imprint","IMPRINT",EDGE,{"derivedFrom":sQuery(id+"F3.wireOp",EDGE,"E0")}),1.0]])]});
            var sketch = newSketch(context, id + "F17", { "sketchPlane" : qUnion([Q0])});
            skArc(sketch, "E106.0.0", {"start": v(-19, -55) * mm, "mid": v(0, -74) * mm, "end": v(19, -55) * mm});
            skLineSegment(sketch, "E106.0.1", {"start": v(19, -55) * mm, "end": v(19, -36) * mm});
            skArc(sketch, "E106.0.2", {"start": v(19, -36) * mm, "mid": v(24.27, -23.27) * mm, "end": v(37, -18) * mm});
            skLineSegment(sketch, "E106.0.3", {"start": v(37, -18) * mm, "end": v(55, -18) * mm});
            skArc(sketch, "E106.0.4", {"start": v(55, -18) * mm, "mid": v(73, 0) * mm, "end": v(55, 18) * mm});
            skLineSegment(sketch, "E106.0.5", {"start": v(55, 18) * mm, "end": v(34, 18) * mm});
            skArc(sketch, "E106.0.6", {"start": v(34, 18) * mm, "mid": v(21.98, 22.98) * mm, "end": v(17, 35) * mm});
            skLineSegment(sketch, "E106.0.7", {"start": v(17, 35) * mm, "end": v(17, 55) * mm});
            skArc(sketch, "E106.0.8", {"start": v(17, 55) * mm, "mid": v(0, 72) * mm, "end": v(-17, 55) * mm});
            skLineSegment(sketch, "E106.0.9", {"start": v(-17, 55) * mm, "end": v(-17, 40) * mm});
            skArc(sketch, "E106.0.10", {"start": v(-17, 40) * mm, "mid": v(-22.86, 25.86) * mm, "end": v(-37, 20) * mm});
            skLineSegment(sketch, "E106.0.11", {"start": v(-37, 20) * mm, "end": v(-55, 20) * mm});
            skArc(sketch, "E106.0.12", {"start": v(-55, 20) * mm, "mid": v(-75, 0) * mm, "end": v(-55, -20) * mm});
            skLineSegment(sketch, "E106.0.13", {"start": v(-55, -20) * mm, "end": v(-38, -20) * mm});
            skArc(sketch, "E106.0.14", {"start": v(-38, -20) * mm, "mid": v(-24.56, -25.56) * mm, "end": v(-19, -39) * mm});
            skLineSegment(sketch, "E106.0.15", {"start": v(-19, -39) * mm, "end": v(-19, -55) * mm});
            skLineSegment(sketch, "E107.0", {"start": v(-37, 20.3) * mm, "end": v(-55, 20.3) * mm});
            skArc(sketch, "E107.1", {"start": v(-17.3, 40) * mm, "mid": v(-23.07, 26.07) * mm, "end": v(-37, 20.3) * mm});
            skLineSegment(sketch, "E107.2", {"start": v(-17.3, 55) * mm, "end": v(-17.3, 40) * mm});
            skArc(sketch, "E107.3", {"start": v(17.3, 55) * mm, "mid": v(0, 72.3) * mm, "end": v(-17.3, 55) * mm});
            skLineSegment(sketch, "E107.4", {"start": v(17.3, 35) * mm, "end": v(17.3, 55) * mm});
            skArc(sketch, "E107.5", {"start": v(-19.3, -55) * mm, "mid": v(0, -74.3) * mm, "end": v(19.3, -55) * mm});
            skLineSegment(sketch, "E107.6", {"start": v(-19.3, -39) * mm, "end": v(-19.3, -55) * mm});
            skArc(sketch, "E107.7", {"start": v(-38, -20.3) * mm, "mid": v(-24.78, -25.78) * mm, "end": v(-19.3, -39) * mm});
            skLineSegment(sketch, "E107.8", {"start": v(-55, -20.3) * mm, "end": v(-38, -20.3) * mm});
            skLineSegment(sketch, "E107.9", {"start": v(19.3, -55) * mm, "end": v(19.3, -36) * mm});
            skArc(sketch, "E107.10", {"start": v(19.3, -36) * mm, "mid": v(24.48, -23.48) * mm, "end": v(37, -18.3) * mm});
            skLineSegment(sketch, "E107.11", {"start": v(37, -18.3) * mm, "end": v(55, -18.3) * mm});
            skArc(sketch, "E107.12", {"start": v(55, -18.3) * mm, "mid": v(73.3, 0) * mm, "end": v(55, 18.3) * mm});
            skLineSegment(sketch, "E107.13", {"start": v(55, 18.3) * mm, "end": v(34, 18.3) * mm});
            skArc(sketch, "E107.14", {"start": v(-55, 20.3) * mm, "mid": v(-75.3, 0) * mm, "end": v(-55, -20.3) * mm});
            skArc(sketch, "E107.15", {"start": v(34, 18.3) * mm, "mid": v(22.2, 23.2) * mm, "end": v(17.3, 35) * mm});
            skSolve(sketch);
        }
        {
            var Q0;
            Q0 = qSketchRegion(id + "F17", true);
            var Q1;
            Q1 = qSketchRegion(id + "F3", true);
            extrude(context, id + "F18", {"entities" : qUnion([Q0, Q1]), "operationType" : NewBodyOperationType.REMOVE, "oppositeDirection" : true, "depth" : (getVariable(context, 'x3')) * mm, "offsetDistance" : 25 * mm});
        }
        {
            var Q0;
            Q0=makeQuery(id+"F4.opExtrude","CAP_FACE",FACE,{"disambiguationData":[OSD([sQuery(id+"F3.wireOp",EDGE,"E0"),sQuery(id+"F3.wireOp",EDGE,"E1"),sQuery(id+"F3.wireOp",EDGE,"E2"),sQuery(id+"F3.wireOp",EDGE,"E3"),sQuery(id+"F3.wireOp",EDGE,"E4"),sQuery(id+"F3.wireOp",EDGE,"E5"),sQuery(id+"F3.wireOp",EDGE,"E6"),sQuery(id+"F3.wireOp",EDGE,"E7"),sQuery(id+"F3.wireOp",EDGE,"E8"),sQuery(id+"F3.wireOp",EDGE,"E9"),sQuery(id+"F3.wireOp",EDGE,"E10"),sQuery(id+"F3.wireOp",EDGE,"E11"),sQuery(id+"F3.wireOp",EDGE,"E12.filletArc"),sQuery(id+"F3.wireOp",EDGE,"E13.filletArc"),sQuery(id+"F3.wireOp",EDGE,"E14.filletArc"),sQuery(id+"F3.wireOp",EDGE,"E15.filletArc"),sQuery(id+"F3.wireOp",EDGE,"E16"),sQuery(id+"F3.wireOp",EDGE,"E17.sketch_text.stroke-0"),sQuery(id+"F3.wireOp",EDGE,"E17.sketch_text.stroke-1"),sQuery(id+"F3.wireOp",EDGE,"E17.sketch_text.stroke-2"),sQuery(id+"F3.wireOp",EDGE,"E17.sketch_text.stroke-3"),sQuery(id+"F3.wireOp",EDGE,"E17.sketch_text.stroke-4"),sQuery(id+"F3.wireOp",EDGE,"E17.sketch_text.stroke-5"),sQuery(id+"F3.wireOp",EDGE,"E17.sketch_text.stroke-6"),sQuery(id+"F3.wireOp",EDGE,"E17.sketch_text.stroke-7"),sQuery(id+"F3.wireOp",EDGE,"E17.sketch_text.stroke-8"),sQuery(id+"F3.wireOp",EDGE,"E17.sketch_text.stroke-9"),sQuery(id+"F3.wireOp",EDGE,"E17.sketch_text.stroke-10"),sQuery(id+"F3.wireOp",EDGE,"E17.sketch_text.stroke-11"),sQuery(id+"F3.wireOp",EDGE,"E17.sketch_text.stroke-12"),sQuery(id+"F3.wireOp",EDGE,"E17.sketch_text.stroke-13"),sQuery(id+"F3.wireOp",EDGE,"E17.sketch_text.stroke-14"),sQuery(id+"F3.wireOp",EDGE,"E17.sketch_text.stroke-15"),sQuery(id+"F3.wireOp",EDGE,"E17.sketch_text.stroke-16"),sQuery(id+"F3.wireOp",EDGE,"E17.sketch_text.stroke-17"),sQuery(id+"F3.wireOp",EDGE,"E17.sketch_text.stroke-18"),sQuery(id+"F3.wireOp",EDGE,"E17.sketch_text.stroke-19"),sQuery(id+"F3.wireOp",EDGE,"E17.sketch_text.stroke-20"),sQuery(id+"F3.wireOp",EDGE,"E17.sketch_text.stroke-21"),sQuery(id+"F3.wireOp",EDGE,"E17.sketch_text.stroke-22"),sQuery(id+"F3.wireOp",EDGE,"E17.sketch_text.stroke-23"),sQuery(id+"F3.wireOp",EDGE,"E17.sketch_text.stroke-24"),sQuery(id+"F3.wireOp",EDGE,"E17.sketch_text.stroke-25"),sQuery(id+"F3.wireOp",EDGE,"E17.sketch_text.stroke-26"),sQuery(id+"F3.wireOp",EDGE,"E17.sketch_text.stroke-27"),sQuery(id+"F3.wireOp",EDGE,"E17.sketch_text.stroke-28"),sQuery(id+"F3.wireOp",EDGE,"E17.sketch_text.stroke-29"),sQuery(id+"F3.wireOp",EDGE,"E17.sketch_text.stroke-30"),sQuery(id+"F3.wireOp",EDGE,"E17.sketch_text.stroke-31"),sQuery(id+"F3.wireOp",EDGE,"E18.sketch_text.stroke-0"),sQuery(id+"F3.wireOp",EDGE,"E18.sketch_text.stroke-1"),sQuery(id+"F3.wireOp",EDGE,"E18.sketch_text.stroke-2"),sQuery(id+"F3.wireOp",EDGE,"E18.sketch_text.stroke-3"),sQuery(id+"F3.wireOp",EDGE,"E18.sketch_text.stroke-4"),sQuery(id+"F3.wireOp",EDGE,"E18.sketch_text.stroke-5"),sQuery(id+"F3.wireOp",EDGE,"E18.sketch_text.stroke-6"),sQuery(id+"F3.wireOp",EDGE,"E18.sketch_text.stroke-7"),sQuery(id+"F3.wireOp",EDGE,"E18.sketch_text.stroke-8"),sQuery(id+"F3.wireOp",EDGE,"E18.sketch_text.stroke-9"),sQuery(id+"F3.wireOp",EDGE,"E18.sketch_text.stroke-10"),sQuery(id+"F3.wireOp",EDGE,"E18.sketch_text.stroke-11"),sQuery(id+"F3.wireOp",EDGE,"E18.sketch_text.stroke-12"),sQuery(id+"F3.wireOp",EDGE,"E18.sketch_text.stroke-13"),sQuery(id+"F3.wireOp",EDGE,"E18.sketch_text.stroke-14"),sQuery(id+"F3.wireOp",EDGE,"E18.sketch_text.stroke-15"),sQuery(id+"F3.wireOp",EDGE,"E18.sketch_text.stroke-16"),sQuery(id+"F3.wireOp",EDGE,"E18.sketch_text.stroke-17"),sQuery(id+"F3.wireOp",EDGE,"E18.sketch_text.stroke-18"),sQuery(id+"F3.wireOp",EDGE,"E18.sketch_text.stroke-19"),sQuery(id+"F3.wireOp",EDGE,"E18.sketch_text.stroke-20"),sQuery(id+"F3.wireOp",EDGE,"E18.sketch_text.stroke-21"),sQuery(id+"F3.wireOp",EDGE,"E18.sketch_text.stroke-22"),sQuery(id+"F3.wireOp",EDGE,"E18.sketch_text.stroke-23"),sQuery(id+"F3.wireOp",EDGE,"E18.sketch_text.stroke-24"),sQuery(id+"F3.wireOp",EDGE,"E18.sketch_text.stroke-25"),sQuery(id+"F3.wireOp",EDGE,"E18.sketch_text.stroke-26"),sQuery(id+"F3.wireOp",EDGE,"E18.sketch_text.stroke-27"),sQuery(id+"F3.wireOp",EDGE,"E19.sketch_text.stroke-0"),sQuery(id+"F3.wireOp",EDGE,"E19.sketch_text.stroke-1"),sQuery(id+"F3.wireOp",EDGE,"E19.sketch_text.stroke-2"),sQuery(id+"F3.wireOp",EDGE,"E19.sketch_text.stroke-3"),sQuery(id+"F3.wireOp",EDGE,"E19.sketch_text.stroke-4"),sQuery(id+"F3.wireOp",EDGE,"E19.sketch_text.stroke-5"),sQuery(id+"F3.wireOp",EDGE,"E19.sketch_text.stroke-6"),sQuery(id+"F3.wireOp",EDGE,"E19.sketch_text.stroke-7"),sQuery(id+"F3.wireOp",EDGE,"E19.sketch_text.stroke-8"),sQuery(id+"F3.wireOp",EDGE,"E19.sketch_text.stroke-9"),sQuery(id+"F3.wireOp",EDGE,"E19.sketch_text.stroke-10"),sQuery(id+"F3.wireOp",EDGE,"E19.sketch_text.stroke-11"),sQuery(id+"F3.wireOp",EDGE,"E19.sketch_text.stroke-12"),sQuery(id+"F3.wireOp",EDGE,"E19.sketch_text.stroke-13"),sQuery(id+"F3.wireOp",EDGE,"E19.sketch_text.stroke-14"),sQuery(id+"F3.wireOp",EDGE,"E19.sketch_text.stroke-15"),sQuery(id+"F3.wireOp",EDGE,"E19.sketch_text.stroke-16"),sQuery(id+"F3.wireOp",EDGE,"E19.sketch_text.stroke-17"),sQuery(id+"F3.wireOp",EDGE,"E19.sketch_text.stroke-18"),sQuery(id+"F3.wireOp",EDGE,"E19.sketch_text.stroke-19"),sQuery(id+"F3.wireOp",EDGE,"E19.sketch_text.stroke-20"),sQuery(id+"F3.wireOp",EDGE,"E19.sketch_text.stroke-21"),sQuery(id+"F3.wireOp",EDGE,"E19.sketch_text.stroke-22"),sQuery(id+"F3.wireOp",EDGE,"E19.sketch_text.stroke-23"),sQuery(id+"F3.wireOp",EDGE,"E19.sketch_text.stroke-24"),sQuery(id+"F3.wireOp",EDGE,"E19.sketch_text.stroke-25"),sQuery(id+"F3.wireOp",EDGE,"E20.sketch_text.stroke-0"),sQuery(id+"F3.wireOp",EDGE,"E20.sketch_text.stroke-1"),sQuery(id+"F3.wireOp",EDGE,"E20.sketch_text.stroke-2"),sQuery(id+"F3.wireOp",EDGE,"E20.sketch_text.stroke-3"),sQuery(id+"F3.wireOp",EDGE,"E20.sketch_text.stroke-4"),sQuery(id+"F3.wireOp",EDGE,"E20.sketch_text.stroke-5"),sQuery(id+"F3.wireOp",EDGE,"E20.sketch_text.stroke-6"),sQuery(id+"F3.wireOp",EDGE,"E20.sketch_text.stroke-7"),sQuery(id+"F3.wireOp",EDGE,"E20.sketch_text.stroke-8"),sQuery(id+"F3.wireOp",EDGE,"E20.sketch_text.stroke-9"),sQuery(id+"F3.wireOp",EDGE,"E20.sketch_text.stroke-10"),sQuery(id+"F3.wireOp",EDGE,"E20.sketch_text.stroke-11"),sQuery(id+"F3.wireOp",EDGE,"E20.sketch_text.stroke-12"),sQuery(id+"F3.wireOp",EDGE,"E20.sketch_text.stroke-13"),sQuery(id+"F3.wireOp",EDGE,"E20.sketch_text.stroke-14"),sQuery(id+"F3.wireOp",EDGE,"E20.sketch_text.stroke-15"),sQuery(id+"F3.wireOp",EDGE,"E20.sketch_text.stroke-16")])],"isStart":false});
            var sketch = newSketch(context, id + "F19", { "sketchPlane" : qUnion([Q0])});
            skArc(sketch, "E108.0.0", {"start": v(-15, -55) * mm, "mid": v(0, -70) * mm, "end": v(15, -55) * mm});
            skLineSegment(sketch, "E108.0.1", {"start": v(15, -55) * mm, "end": v(15, -28) * mm});
            skArc(sketch, "E108.0.2", {"start": v(15, -28) * mm, "mid": v(19.1, -18.1) * mm, "end": v(29, -14) * mm});
            skLineSegment(sketch, "E108.0.3", {"start": v(29, -14) * mm, "end": v(55, -14) * mm});
            skArc(sketch, "E108.0.4", {"start": v(55, -14) * mm, "mid": v(69, 0) * mm, "end": v(55, 14) * mm});
            skLineSegment(sketch, "E108.0.5", {"start": v(55, 14) * mm, "end": v(26, 14) * mm});
            skArc(sketch, "E108.0.6", {"start": v(26, 14) * mm, "mid": v(16.8, 17.8) * mm, "end": v(13, 27) * mm});
            skLineSegment(sketch, "E108.0.7", {"start": v(13, 27) * mm, "end": v(13, 55) * mm});
            skArc(sketch, "E108.0.8", {"start": v(13, 55) * mm, "mid": v(0, 68) * mm, "end": v(-13, 55) * mm});
            skLineSegment(sketch, "E108.0.9", {"start": v(-13, 55) * mm, "end": v(-13, 32) * mm});
            skArc(sketch, "E108.0.10", {"start": v(-13, 32) * mm, "mid": v(-17.69, 20.69) * mm, "end": v(-29, 16) * mm});
            skLineSegment(sketch, "E108.0.11", {"start": v(-29, 16) * mm, "end": v(-55, 16) * mm});
            skArc(sketch, "E108.0.12", {"start": v(-55, 16) * mm, "mid": v(-71, 0) * mm, "end": v(-55, -16) * mm});
            skLineSegment(sketch, "E108.0.13", {"start": v(-55, -16) * mm, "end": v(-30, -16) * mm});
            skArc(sketch, "E108.0.14", {"start": v(-30, -16) * mm, "mid": v(-19.4, -20.4) * mm, "end": v(-15, -31) * mm});
            skLineSegment(sketch, "E108.0.15", {"start": v(-15, -31) * mm, "end": v(-15, -55) * mm});
            skLineSegment(sketch, "E109.0", {"start": v(-13.3, 16.3) * mm, "end": v(-55, 16.3) * mm});
            skLineSegment(sketch, "E109.1", {"start": v(15.3, -55) * mm, "end": v(15.3, -14.3) * mm});
            skArc(sketch, "E109.2", {"start": v(-15.3, -55) * mm, "mid": v(0, -70.3) * mm, "end": v(15.3, -55) * mm});
            skLineSegment(sketch, "E109.3", {"start": v(-15.3, -16.3) * mm, "end": v(-15.3, -55) * mm});
            skLineSegment(sketch, "E109.4", {"start": v(-55, -16.3) * mm, "end": v(-15.3, -16.3) * mm});
            skLineSegment(sketch, "E109.5", {"start": v(15.3, -14.3) * mm, "end": v(55, -14.3) * mm});
            skArc(sketch, "E109.6", {"start": v(-55, 16.3) * mm, "mid": v(-71.3, 0) * mm, "end": v(-55, -16.3) * mm});
            skArc(sketch, "E109.7", {"start": v(55, -14.3) * mm, "mid": v(69.3, 0) * mm, "end": v(55, 14.3) * mm});
            skLineSegment(sketch, "E109.8", {"start": v(55, 14.3) * mm, "end": v(13.3, 14.3) * mm});
            skLineSegment(sketch, "E109.9", {"start": v(13.3, 14.3) * mm, "end": v(13.3, 55) * mm});
            skArc(sketch, "E109.10", {"start": v(13.3, 55) * mm, "mid": v(0, 68.3) * mm, "end": v(-13.3, 55) * mm});
            skLineSegment(sketch, "E109.11", {"start": v(-13.3, 55) * mm, "end": v(-13.3, 16.3) * mm});
            skSolve(sketch);
        }
        {
            var Q0;
            Q0 = qSketchRegion(id + "F19", true);
            var Q1;
            Q1 = qSketchRegion(id + "F6", true);
            extrude(context, id + "F20", {"entities" : qUnion([Q0, Q1]), "operationType" : NewBodyOperationType.REMOVE, "oppositeDirection" : true, "depth" : (getVariable(context, 'x3')) * mm, "offsetDistance" : 25 * mm});
        }
        {
            var Q0;
            Q0=makeQuery(id+"F7.opExtrude","CAP_FACE",FACE,{"disambiguationData":[OSD([sQuery(id+"F6.wireOp",EDGE,"E21"),sQuery(id+"F6.wireOp",EDGE,"E22"),sQuery(id+"F6.wireOp",EDGE,"E23"),sQuery(id+"F6.wireOp",EDGE,"E24"),sQuery(id+"F6.wireOp",EDGE,"E25"),sQuery(id+"F6.wireOp",EDGE,"E26"),sQuery(id+"F6.wireOp",EDGE,"E27"),sQuery(id+"F6.wireOp",EDGE,"E28"),sQuery(id+"F6.wireOp",EDGE,"E29"),sQuery(id+"F6.wireOp",EDGE,"E30"),sQuery(id+"F6.wireOp",EDGE,"E31"),sQuery(id+"F6.wireOp",EDGE,"E32"),sQuery(id+"F6.wireOp",EDGE,"E33.filletArc"),sQuery(id+"F6.wireOp",EDGE,"E34.filletArc"),sQuery(id+"F6.wireOp",EDGE,"E35.filletArc"),sQuery(id+"F6.wireOp",EDGE,"E36.filletArc"),sQuery(id+"F6.wireOp",EDGE,"E37"),sQuery(id+"F6.wireOp",EDGE,"E38.sketch_text.stroke-0"),sQuery(id+"F6.wireOp",EDGE,"E38.sketch_text.stroke-1"),sQuery(id+"F6.wireOp",EDGE,"E38.sketch_text.stroke-2"),sQuery(id+"F6.wireOp",EDGE,"E38.sketch_text.stroke-3"),sQuery(id+"F6.wireOp",EDGE,"E38.sketch_text.stroke-4"),sQuery(id+"F6.wireOp",EDGE,"E38.sketch_text.stroke-5"),sQuery(id+"F6.wireOp",EDGE,"E38.sketch_text.stroke-6"),sQuery(id+"F6.wireOp",EDGE,"E38.sketch_text.stroke-7"),sQuery(id+"F6.wireOp",EDGE,"E38.sketch_text.stroke-8"),sQuery(id+"F6.wireOp",EDGE,"E38.sketch_text.stroke-9"),sQuery(id+"F6.wireOp",EDGE,"E38.sketch_text.stroke-10"),sQuery(id+"F6.wireOp",EDGE,"E38.sketch_text.stroke-11"),sQuery(id+"F6.wireOp",EDGE,"E38.sketch_text.stroke-12"),sQuery(id+"F6.wireOp",EDGE,"E38.sketch_text.stroke-13"),sQuery(id+"F6.wireOp",EDGE,"E38.sketch_text.stroke-14"),sQuery(id+"F6.wireOp",EDGE,"E38.sketch_text.stroke-15"),sQuery(id+"F6.wireOp",EDGE,"E38.sketch_text.stroke-16"),sQuery(id+"F6.wireOp",EDGE,"E38.sketch_text.stroke-17"),sQuery(id+"F6.wireOp",EDGE,"E38.sketch_text.stroke-18"),sQuery(id+"F6.wireOp",EDGE,"E38.sketch_text.stroke-19"),sQuery(id+"F6.wireOp",EDGE,"E38.sketch_text.stroke-20"),sQuery(id+"F6.wireOp",EDGE,"E38.sketch_text.stroke-21"),sQuery(id+"F6.wireOp",EDGE,"E38.sketch_text.stroke-22"),sQuery(id+"F6.wireOp",EDGE,"E38.sketch_text.stroke-23"),sQuery(id+"F6.wireOp",EDGE,"E38.sketch_text.stroke-24"),sQuery(id+"F6.wireOp",EDGE,"E38.sketch_text.stroke-25"),sQuery(id+"F6.wireOp",EDGE,"E38.sketch_text.stroke-26"),sQuery(id+"F6.wireOp",EDGE,"E38.sketch_text.stroke-27"),sQuery(id+"F6.wireOp",EDGE,"E38.sketch_text.stroke-28"),sQuery(id+"F6.wireOp",EDGE,"E38.sketch_text.stroke-29"),sQuery(id+"F6.wireOp",EDGE,"E38.sketch_text.stroke-30"),sQuery(id+"F6.wireOp",EDGE,"E38.sketch_text.stroke-31"),sQuery(id+"F6.wireOp",EDGE,"E38.sketch_text.stroke-32"),sQuery(id+"F6.wireOp",EDGE,"E38.sketch_text.stroke-33"),sQuery(id+"F6.wireOp",EDGE,"E38.sketch_text.stroke-34"),sQuery(id+"F6.wireOp",EDGE,"E38.sketch_text.stroke-35"),sQuery(id+"F6.wireOp",EDGE,"E38.sketch_text.stroke-36"),sQuery(id+"F6.wireOp",EDGE,"E42.sketch_text.stroke-0"),sQuery(id+"F6.wireOp",EDGE,"E42.sketch_text.stroke-1"),sQuery(id+"F6.wireOp",EDGE,"E42.sketch_text.stroke-2"),sQuery(id+"F6.wireOp",EDGE,"E42.sketch_text.stroke-3"),sQuery(id+"F6.wireOp",EDGE,"E42.sketch_text.stroke-4"),sQuery(id+"F6.wireOp",EDGE,"E42.sketch_text.stroke-5"),sQuery(id+"F6.wireOp",EDGE,"E42.sketch_text.stroke-6"),sQuery(id+"F6.wireOp",EDGE,"E42.sketch_text.stroke-7"),sQuery(id+"F6.wireOp",EDGE,"E42.sketch_text.stroke-8"),sQuery(id+"F6.wireOp",EDGE,"E42.sketch_text.stroke-9"),sQuery(id+"F6.wireOp",EDGE,"E42.sketch_text.stroke-10"),sQuery(id+"F6.wireOp",EDGE,"E42.sketch_text.stroke-11"),sQuery(id+"F6.wireOp",EDGE,"E42.sketch_text.stroke-12"),sQuery(id+"F6.wireOp",EDGE,"E42.sketch_text.stroke-13"),sQuery(id+"F6.wireOp",EDGE,"E42.sketch_text.stroke-14"),sQuery(id+"F6.wireOp",EDGE,"E42.sketch_text.stroke-15"),sQuery(id+"F6.wireOp",EDGE,"E42.sketch_text.stroke-16"),sQuery(id+"F6.wireOp",EDGE,"E42.sketch_text.stroke-17"),sQuery(id+"F6.wireOp",EDGE,"E42.sketch_text.stroke-18"),sQuery(id+"F6.wireOp",EDGE,"E42.sketch_text.stroke-19"),sQuery(id+"F6.wireOp",EDGE,"E42.sketch_text.stroke-20"),sQuery(id+"F6.wireOp",EDGE,"E42.sketch_text.stroke-21"),sQuery(id+"F6.wireOp",EDGE,"E42.sketch_text.stroke-22"),sQuery(id+"F6.wireOp",EDGE,"E42.sketch_text.stroke-23"),sQuery(id+"F6.wireOp",EDGE,"E42.sketch_text.stroke-24"),sQuery(id+"F6.wireOp",EDGE,"E42.sketch_text.stroke-25"),sQuery(id+"F6.wireOp",EDGE,"E42.sketch_text.stroke-26"),sQuery(id+"F6.wireOp",EDGE,"E43.sketch_text.stroke-0"),sQuery(id+"F6.wireOp",EDGE,"E43.sketch_text.stroke-1"),sQuery(id+"F6.wireOp",EDGE,"E43.sketch_text.stroke-2"),sQuery(id+"F6.wireOp",EDGE,"E43.sketch_text.stroke-3"),sQuery(id+"F6.wireOp",EDGE,"E43.sketch_text.stroke-4"),sQuery(id+"F6.wireOp",EDGE,"E43.sketch_text.stroke-5"),sQuery(id+"F6.wireOp",EDGE,"E43.sketch_text.stroke-6"),sQuery(id+"F6.wireOp",EDGE,"E43.sketch_text.stroke-7"),sQuery(id+"F6.wireOp",EDGE,"E43.sketch_text.stroke-8"),sQuery(id+"F6.wireOp",EDGE,"E43.sketch_text.stroke-9"),sQuery(id+"F6.wireOp",EDGE,"E43.sketch_text.stroke-10"),sQuery(id+"F6.wireOp",EDGE,"E43.sketch_text.stroke-11"),sQuery(id+"F6.wireOp",EDGE,"E43.sketch_text.stroke-12"),sQuery(id+"F6.wireOp",EDGE,"E43.sketch_text.stroke-13"),sQuery(id+"F6.wireOp",EDGE,"E43.sketch_text.stroke-14"),sQuery(id+"F6.wireOp",EDGE,"E43.sketch_text.stroke-15"),sQuery(id+"F6.wireOp",EDGE,"E43.sketch_text.stroke-16"),sQuery(id+"F6.wireOp",EDGE,"E43.sketch_text.stroke-17"),sQuery(id+"F6.wireOp",EDGE,"E43.sketch_text.stroke-18"),sQuery(id+"F6.wireOp",EDGE,"E43.sketch_text.stroke-19"),sQuery(id+"F6.wireOp",EDGE,"E43.sketch_text.stroke-20"),sQuery(id+"F6.wireOp",EDGE,"E43.sketch_text.stroke-21"),sQuery(id+"F6.wireOp",EDGE,"E43.sketch_text.stroke-22"),sQuery(id+"F6.wireOp",EDGE,"E43.sketch_text.stroke-23"),sQuery(id+"F6.wireOp",EDGE,"E43.sketch_text.stroke-24"),sQuery(id+"F6.wireOp",EDGE,"E43.sketch_text.stroke-25"),sQuery(id+"F6.wireOp",EDGE,"E43.sketch_text.stroke-26"),sQuery(id+"F6.wireOp",EDGE,"E43.sketch_text.stroke-27"),sQuery(id+"F6.wireOp",EDGE,"E43.sketch_text.stroke-28"),sQuery(id+"F6.wireOp",EDGE,"E43.sketch_text.stroke-29"),sQuery(id+"F6.wireOp",EDGE,"E44.sketch_text.stroke-0"),sQuery(id+"F6.wireOp",EDGE,"E44.sketch_text.stroke-1"),sQuery(id+"F6.wireOp",EDGE,"E44.sketch_text.stroke-2"),sQuery(id+"F6.wireOp",EDGE,"E44.sketch_text.stroke-3"),sQuery(id+"F6.wireOp",EDGE,"E44.sketch_text.stroke-4"),sQuery(id+"F6.wireOp",EDGE,"E44.sketch_text.stroke-5"),sQuery(id+"F6.wireOp",EDGE,"E44.sketch_text.stroke-6"),sQuery(id+"F6.wireOp",EDGE,"E44.sketch_text.stroke-7"),sQuery(id+"F6.wireOp",EDGE,"E44.sketch_text.stroke-8"),sQuery(id+"F6.wireOp",EDGE,"E44.sketch_text.stroke-9"),sQuery(id+"F6.wireOp",EDGE,"E44.sketch_text.stroke-10"),sQuery(id+"F6.wireOp",EDGE,"E44.sketch_text.stroke-11"),sQuery(id+"F6.wireOp",EDGE,"E44.sketch_text.stroke-12"),sQuery(id+"F6.wireOp",EDGE,"E44.sketch_text.stroke-13"),sQuery(id+"F6.wireOp",EDGE,"E44.sketch_text.stroke-14"),sQuery(id+"F6.wireOp",EDGE,"E44.sketch_text.stroke-15"),sQuery(id+"F6.wireOp",EDGE,"E44.sketch_text.stroke-16"),sQuery(id+"F6.wireOp",EDGE,"E44.sketch_text.stroke-17"),sQuery(id+"F6.wireOp",EDGE,"E44.sketch_text.stroke-18"),sQuery(id+"F6.wireOp",EDGE,"E44.sketch_text.stroke-19"),sQuery(id+"F6.wireOp",EDGE,"E44.sketch_text.stroke-20")])],"isStart":false});
            var sketch = newSketch(context, id + "F21", { "sketchPlane" : qUnion([Q0])});
            skLineSegment(sketch, "E110.0", {"start": v(11, -20) * mm, "end": v(11, -55) * mm});
            skArc(sketch, "E111.0", {"start": v(-11, -55) * mm, "mid": v(0, -66) * mm, "end": v(11, -55) * mm});
            skLineSegment(sketch, "E112.0", {"start": v(-11, -55) * mm, "end": v(-11, -23) * mm});
            skArc(sketch, "E113.0", {"start": v(-11, -23) * mm, "mid": v(-14.22, -15.22) * mm, "end": v(-22, -12) * mm});
            skLineSegment(sketch, "E114.0", {"start": v(-22, -12) * mm, "end": v(-55, -12) * mm});
            skArc(sketch, "E115.0", {"start": v(-55, 12) * mm, "mid": v(-67, 0) * mm, "end": v(-55, -12) * mm});
            skLineSegment(sketch, "E116.0", {"start": v(-55, 12) * mm, "end": v(-21, 12) * mm});
            skArc(sketch, "E117.0", {"start": v(-21, 12) * mm, "mid": v(-12.51, 15.51) * mm, "end": v(-9, 24) * mm});
            skLineSegment(sketch, "E117.1", {"start": v(-9, 24) * mm, "end": v(-9, 55) * mm});
            skLineSegment(sketch, "E117.2", {"start": v(9, 55) * mm, "end": v(9, 19) * mm});
            skArc(sketch, "E117.3", {"start": v(9, 55) * mm, "mid": v(0, 64) * mm, "end": v(-9, 55) * mm});
            skLineSegment(sketch, "E117.4", {"start": v(18, 10) * mm, "end": v(55, 10) * mm});
            skArc(sketch, "E117.5", {"start": v(9, 19) * mm, "mid": v(11.64, 12.64) * mm, "end": v(18, 10) * mm});
            skArc(sketch, "E117.6", {"start": v(55, -10) * mm, "mid": v(65, 0) * mm, "end": v(55, 10) * mm});
            skLineSegment(sketch, "E117.7", {"start": v(55, -10) * mm, "end": v(21, -10) * mm});
            skArc(sketch, "E117.8", {"start": v(21, -10) * mm, "mid": v(13.93, -12.93) * mm, "end": v(11, -20) * mm});
            skSolve(sketch);
        }
        {
            var Q0;
            Q0 = qSketchRegion(id + "F21", true);
            var Q1;
            Q1=makeQuery(id+"F9.imprint","IMPRINT",FACE,{"disambiguationData":[TD([[makeQuery(id+"F9.imprint","IMPRINT",EDGE,{"derivedFrom":sQuery(id+"F9.wireOp",EDGE,"E45")}),-1.0]])]});
            extrude(context, id + "F22", {"entities" : qUnion([Q0, Q1]), "operationType" : NewBodyOperationType.REMOVE, "oppositeDirection" : true, "depth" : (getVariable(context, 'x3')) * mm, "offsetDistance" : 25 * mm});
        }
        {
            var Q0;
            Q0=makeQuery(id+"F21.imprint","IMPRINT",FACE,{"disambiguationData":[TD([[makeQuery(id+"F21.imprint","IMPRINT",EDGE,{"derivedFrom":sQuery(id+"F21.wireOp",EDGE,"E110.0")}),1.0]])]});
            var sketch = newSketch(context, id + "F23", { "sketchPlane" : qUnion([Q0])});
            skArc(sketch, "E118.0", {"start": v(-55, 12) * mm, "mid": v(-67, 0) * mm, "end": v(-55, -12) * mm});
            skLineSegment(sketch, "E119.0", {"start": v(-55, 12) * mm, "end": v(-21, 12) * mm});
            skArc(sketch, "E120.0", {"start": v(-21, 12) * mm, "mid": v(-12.51, 15.51) * mm, "end": v(-9, 24) * mm});
            skLineSegment(sketch, "E121.0", {"start": v(-9, 24) * mm, "end": v(-9, 55) * mm});
            skArc(sketch, "E122.0", {"start": v(9, 55) * mm, "mid": v(0, 64) * mm, "end": v(-9, 55) * mm});
            skLineSegment(sketch, "E123.0", {"start": v(9, 55) * mm, "end": v(9, 19) * mm});
            skArc(sketch, "E124.0", {"start": v(9, 19) * mm, "mid": v(11.64, 12.64) * mm, "end": v(18, 10) * mm});
            skLineSegment(sketch, "E125.0", {"start": v(18, 10) * mm, "end": v(55, 10) * mm});
            skArc(sketch, "E126.0", {"start": v(55, -10) * mm, "mid": v(65, 0) * mm, "end": v(55, 10) * mm});
            skLineSegment(sketch, "E127.0", {"start": v(55, -10) * mm, "end": v(21, -10) * mm});
            skArc(sketch, "E128.0", {"start": v(21, -10) * mm, "mid": v(13.93, -12.93) * mm, "end": v(11, -20) * mm});
            skLineSegment(sketch, "E129.0", {"start": v(11, -20) * mm, "end": v(11, -55) * mm});
            skArc(sketch, "E130.0", {"start": v(-11, -55) * mm, "mid": v(0, -66) * mm, "end": v(11, -55) * mm});
            skLineSegment(sketch, "E131.0", {"start": v(-11, -55) * mm, "end": v(-11, -23) * mm});
            skArc(sketch, "E132.0", {"start": v(-11, -23) * mm, "mid": v(-14.22, -15.22) * mm, "end": v(-22, -12) * mm});
            skLineSegment(sketch, "E133.0", {"start": v(-22, -12) * mm, "end": v(-55, -12) * mm});
            skLineSegment(sketch, "E134.0", {"start": v(-55, 12.3) * mm, "end": v(-21, 12.3) * mm});
            skArc(sketch, "E134.1", {"start": v(-55, 12.3) * mm, "mid": v(-67.3, 0) * mm, "end": v(-55, -12.3) * mm});
            skLineSegment(sketch, "E134.2", {"start": v(-22, -12.3) * mm, "end": v(-55, -12.3) * mm});
            skArc(sketch, "E134.3", {"start": v(-11.3, -23) * mm, "mid": v(-14.43, -15.43) * mm, "end": v(-22, -12.3) * mm});
            skLineSegment(sketch, "E134.4", {"start": v(-11.3, -55) * mm, "end": v(-11.3, -23) * mm});
            skArc(sketch, "E134.5", {"start": v(9.3, 19) * mm, "mid": v(11.85, 12.85) * mm, "end": v(18, 10.3) * mm});
            skLineSegment(sketch, "E134.6", {"start": v(9.3, 55) * mm, "end": v(9.3, 19) * mm});
            skArc(sketch, "E134.7", {"start": v(9.3, 55) * mm, "mid": v(0, 64.3) * mm, "end": v(-9.3, 55) * mm});
            skLineSegment(sketch, "E134.8", {"start": v(-9.3, 24) * mm, "end": v(-9.3, 55) * mm});
            skLineSegment(sketch, "E134.9", {"start": v(18, 10.3) * mm, "end": v(55, 10.3) * mm});
            skArc(sketch, "E134.10", {"start": v(55, -10.3) * mm, "mid": v(65.3, 0) * mm, "end": v(55, 10.3) * mm});
            skLineSegment(sketch, "E134.11", {"start": v(55, -10.3) * mm, "end": v(21, -10.3) * mm});
            skArc(sketch, "E134.12", {"start": v(21, -10.3) * mm, "mid": v(14.14, -13.14) * mm, "end": v(11.3, -20) * mm});
            skLineSegment(sketch, "E134.13", {"start": v(11.3, -20) * mm, "end": v(11.3, -55) * mm});
            skArc(sketch, "E134.14", {"start": v(-21, 12.3) * mm, "mid": v(-12.73, 15.73) * mm, "end": v(-9.3, 24) * mm});
            skArc(sketch, "E134.15", {"start": v(-11.3, -55) * mm, "mid": v(0, -66.3) * mm, "end": v(11.3, -55) * mm});
            skSolve(sketch);
        }
        {
            var Q0;
            Q0=makeQuery(id+"F23.imprint","IMPRINT",FACE,{"disambiguationData":[TD([[makeQuery(id+"F23.imprint","IMPRINT",EDGE,{"derivedFrom":sQuery(id+"F23.wireOp",EDGE,"E118.0")}),-1.0]])]});
            var Q1;
            Q1=makeQuery(id+"F22.boolean.opBoolean","COPY",FACE,{"derivedFrom":makeQuery(id+"F22.opExtrude","CAP_FACE",FACE,{"disambiguationData":[OSD([sQuery(id+"F21.wireOp",EDGE,"E110.0"),sQuery(id+"F21.wireOp",EDGE,"E111.0"),sQuery(id+"F21.wireOp",EDGE,"E112.0"),sQuery(id+"F21.wireOp",EDGE,"E113.0"),sQuery(id+"F21.wireOp",EDGE,"E114.0"),sQuery(id+"F21.wireOp",EDGE,"E115.0"),sQuery(id+"F21.wireOp",EDGE,"E116.0"),sQuery(id+"F21.wireOp",EDGE,"E117.0"),sQuery(id+"F21.wireOp",EDGE,"E117.1"),sQuery(id+"F21.wireOp",EDGE,"E117.2"),sQuery(id+"F21.wireOp",EDGE,"E117.3"),sQuery(id+"F21.wireOp",EDGE,"E117.4"),sQuery(id+"F21.wireOp",EDGE,"E117.5"),sQuery(id+"F21.wireOp",EDGE,"E117.6"),sQuery(id+"F21.wireOp",EDGE,"E117.7"),sQuery(id+"F21.wireOp",EDGE,"E117.8")])],"isStart":false})});
            extrude(context, id + "F24", {"entities" : qUnion([Q0]), "operationType" : NewBodyOperationType.ADD, "endBound" : BoundingType.UP_TO_SURFACE, "oppositeDirection" : true, "depth" : 25 * mm, "endBoundEntityFace" : qUnion([Q1]), "offsetDistance" : 25 * mm});
        }
        {
            var Q0;
            Q0=makeQuery(id+"F10.opExtrude","CAP_FACE",FACE,{"disambiguationData":[OSD([sQuery(id+"F9.wireOp",EDGE,"E45"),sQuery(id+"F9.wireOp",EDGE,"E46"),sQuery(id+"F9.wireOp",EDGE,"E47"),sQuery(id+"F9.wireOp",EDGE,"E48"),sQuery(id+"F9.wireOp",EDGE,"E49"),sQuery(id+"F9.wireOp",EDGE,"E50"),sQuery(id+"F9.wireOp",EDGE,"E51"),sQuery(id+"F9.wireOp",EDGE,"E52"),sQuery(id+"F9.wireOp",EDGE,"E53"),sQuery(id+"F9.wireOp",EDGE,"E54"),sQuery(id+"F9.wireOp",EDGE,"E55"),sQuery(id+"F9.wireOp",EDGE,"E56"),sQuery(id+"F9.wireOp",EDGE,"E57.filletArc"),sQuery(id+"F9.wireOp",EDGE,"E58.filletArc"),sQuery(id+"F9.wireOp",EDGE,"E59.filletArc"),sQuery(id+"F9.wireOp",EDGE,"E60.filletArc"),sQuery(id+"F9.wireOp",EDGE,"E61"),sQuery(id+"F9.wireOp",EDGE,"E62.sketch_text.stroke-0"),sQuery(id+"F9.wireOp",EDGE,"E62.sketch_text.stroke-1"),sQuery(id+"F9.wireOp",EDGE,"E62.sketch_text.stroke-2"),sQuery(id+"F9.wireOp",EDGE,"E62.sketch_text.stroke-3"),sQuery(id+"F9.wireOp",EDGE,"E62.sketch_text.stroke-4"),sQuery(id+"F9.wireOp",EDGE,"E62.sketch_text.stroke-5"),sQuery(id+"F9.wireOp",EDGE,"E62.sketch_text.stroke-6"),sQuery(id+"F9.wireOp",EDGE,"E62.sketch_text.stroke-7"),sQuery(id+"F9.wireOp",EDGE,"E62.sketch_text.stroke-8"),sQuery(id+"F9.wireOp",EDGE,"E62.sketch_text.stroke-9"),sQuery(id+"F9.wireOp",EDGE,"E62.sketch_text.stroke-10"),sQuery(id+"F9.wireOp",EDGE,"E62.sketch_text.stroke-11"),sQuery(id+"F9.wireOp",EDGE,"E62.sketch_text.stroke-12"),sQuery(id+"F9.wireOp",EDGE,"E62.sketch_text.stroke-13"),sQuery(id+"F9.wireOp",EDGE,"E62.sketch_text.stroke-14"),sQuery(id+"F9.wireOp",EDGE,"E62.sketch_text.stroke-15"),sQuery(id+"F9.wireOp",EDGE,"E62.sketch_text.stroke-16"),sQuery(id+"F9.wireOp",EDGE,"E62.sketch_text.stroke-17"),sQuery(id+"F9.wireOp",EDGE,"E66.sketch_text.stroke-0"),sQuery(id+"F9.wireOp",EDGE,"E66.sketch_text.stroke-1"),sQuery(id+"F9.wireOp",EDGE,"E66.sketch_text.stroke-2"),sQuery(id+"F9.wireOp",EDGE,"E66.sketch_text.stroke-3"),sQuery(id+"F9.wireOp",EDGE,"E66.sketch_text.stroke-4"),sQuery(id+"F9.wireOp",EDGE,"E66.sketch_text.stroke-5"),sQuery(id+"F9.wireOp",EDGE,"E66.sketch_text.stroke-6"),sQuery(id+"F9.wireOp",EDGE,"E66.sketch_text.stroke-7"),sQuery(id+"F9.wireOp",EDGE,"E66.sketch_text.stroke-8"),sQuery(id+"F9.wireOp",EDGE,"E66.sketch_text.stroke-9"),sQuery(id+"F9.wireOp",EDGE,"E66.sketch_text.stroke-10"),sQuery(id+"F9.wireOp",EDGE,"E66.sketch_text.stroke-11"),sQuery(id+"F9.wireOp",EDGE,"E66.sketch_text.stroke-12"),sQuery(id+"F9.wireOp",EDGE,"E66.sketch_text.stroke-13"),sQuery(id+"F9.wireOp",EDGE,"E66.sketch_text.stroke-14"),sQuery(id+"F9.wireOp",EDGE,"E66.sketch_text.stroke-15"),sQuery(id+"F9.wireOp",EDGE,"E66.sketch_text.stroke-16"),sQuery(id+"F9.wireOp",EDGE,"E66.sketch_text.stroke-17"),sQuery(id+"F9.wireOp",EDGE,"E66.sketch_text.stroke-18"),sQuery(id+"F9.wireOp",EDGE,"E66.sketch_text.stroke-19"),sQuery(id+"F9.wireOp",EDGE,"E66.sketch_text.stroke-20"),sQuery(id+"F9.wireOp",EDGE,"E66.sketch_text.stroke-21"),sQuery(id+"F9.wireOp",EDGE,"E66.sketch_text.stroke-22"),sQuery(id+"F9.wireOp",EDGE,"E66.sketch_text.stroke-23"),sQuery(id+"F9.wireOp",EDGE,"E66.sketch_text.stroke-24"),sQuery(id+"F9.wireOp",EDGE,"E66.sketch_text.stroke-25"),sQuery(id+"F9.wireOp",EDGE,"E66.sketch_text.stroke-26"),sQuery(id+"F9.wireOp",EDGE,"E66.sketch_text.stroke-27"),sQuery(id+"F9.wireOp",EDGE,"E66.sketch_text.stroke-28"),sQuery(id+"F9.wireOp",EDGE,"E66.sketch_text.stroke-29"),sQuery(id+"F9.wireOp",EDGE,"E66.sketch_text.stroke-30"),sQuery(id+"F9.wireOp",EDGE,"E66.sketch_text.stroke-31"),sQuery(id+"F9.wireOp",EDGE,"E66.sketch_text.stroke-32"),sQuery(id+"F9.wireOp",EDGE,"E66.sketch_text.stroke-33"),sQuery(id+"F9.wireOp",EDGE,"E67.sketch_text.stroke-0"),sQuery(id+"F9.wireOp",EDGE,"E67.sketch_text.stroke-1"),sQuery(id+"F9.wireOp",EDGE,"E67.sketch_text.stroke-2"),sQuery(id+"F9.wireOp",EDGE,"E67.sketch_text.stroke-3"),sQuery(id+"F9.wireOp",EDGE,"E67.sketch_text.stroke-4"),sQuery(id+"F9.wireOp",EDGE,"E67.sketch_text.stroke-5"),sQuery(id+"F9.wireOp",EDGE,"E67.sketch_text.stroke-6"),sQuery(id+"F9.wireOp",EDGE,"E67.sketch_text.stroke-7"),sQuery(id+"F9.wireOp",EDGE,"E67.sketch_text.stroke-8"),sQuery(id+"F9.wireOp",EDGE,"E67.sketch_text.stroke-9"),sQuery(id+"F9.wireOp",EDGE,"E67.sketch_text.stroke-10"),sQuery(id+"F9.wireOp",EDGE,"E67.sketch_text.stroke-11"),sQuery(id+"F9.wireOp",EDGE,"E67.sketch_text.stroke-12"),sQuery(id+"F9.wireOp",EDGE,"E67.sketch_text.stroke-13"),sQuery(id+"F9.wireOp",EDGE,"E67.sketch_text.stroke-14"),sQuery(id+"F9.wireOp",EDGE,"E67.sketch_text.stroke-15"),sQuery(id+"F9.wireOp",EDGE,"E67.sketch_text.stroke-16"),sQuery(id+"F9.wireOp",EDGE,"E67.sketch_text.stroke-17"),sQuery(id+"F9.wireOp",EDGE,"E67.sketch_text.stroke-18"),sQuery(id+"F9.wireOp",EDGE,"E67.sketch_text.stroke-19"),sQuery(id+"F9.wireOp",EDGE,"E68.sketch_text.stroke-0"),sQuery(id+"F9.wireOp",EDGE,"E68.sketch_text.stroke-1"),sQuery(id+"F9.wireOp",EDGE,"E68.sketch_text.stroke-2"),sQuery(id+"F9.wireOp",EDGE,"E68.sketch_text.stroke-3"),sQuery(id+"F9.wireOp",EDGE,"E68.sketch_text.stroke-4"),sQuery(id+"F9.wireOp",EDGE,"E68.sketch_text.stroke-5"),sQuery(id+"F9.wireOp",EDGE,"E68.sketch_text.stroke-6"),sQuery(id+"F9.wireOp",EDGE,"E68.sketch_text.stroke-7"),sQuery(id+"F9.wireOp",EDGE,"E68.sketch_text.stroke-8"),sQuery(id+"F9.wireOp",EDGE,"E68.sketch_text.stroke-9"),sQuery(id+"F9.wireOp",EDGE,"E68.sketch_text.stroke-10"),sQuery(id+"F9.wireOp",EDGE,"E68.sketch_text.stroke-11"),sQuery(id+"F9.wireOp",EDGE,"E68.sketch_text.stroke-12"),sQuery(id+"F9.wireOp",EDGE,"E68.sketch_text.stroke-13"),sQuery(id+"F9.wireOp",EDGE,"E68.sketch_text.stroke-14"),sQuery(id+"F9.wireOp",EDGE,"E68.sketch_text.stroke-15"),sQuery(id+"F9.wireOp",EDGE,"E68.sketch_text.stroke-16"),sQuery(id+"F9.wireOp",EDGE,"E68.sketch_text.stroke-17")])],"isStart":false});
            var sketch = newSketch(context, id + "F25", { "sketchPlane" : qUnion([Q0])});
            skLineSegment(sketch, "E135.0", {"start": v(7, -55) * mm, "end": v(7, -12) * mm});
            skArc(sketch, "E136.0", {"start": v(13, -6) * mm, "mid": v(8.76, -7.76) * mm, "end": v(7, -12) * mm});
            skLineSegment(sketch, "E137.0", {"start": v(13, -6) * mm, "end": v(55, -6) * mm});
            skLineSegment(sketch, "E138.0", {"start": v(55, 6) * mm, "end": v(10, 6) * mm});
            skArc(sketch, "E139.0", {"start": v(5, 11) * mm, "mid": v(6.46, 7.46) * mm, "end": v(10, 6) * mm});
            skLineSegment(sketch, "E140.0", {"start": v(5, 11) * mm, "end": v(5, 55) * mm});
            skLineSegment(sketch, "E141.0", {"start": v(-5, 55) * mm, "end": v(-5, 16) * mm});
            skArc(sketch, "E142.0", {"start": v(-13, 8) * mm, "mid": v(-7.34, 10.34) * mm, "end": v(-5, 16) * mm});
            skLineSegment(sketch, "E143.0", {"start": v(-13, 8) * mm, "end": v(-55, 8) * mm});
            skLineSegment(sketch, "E144.0", {"start": v(-55, -8) * mm, "end": v(-14, -8) * mm});
            skArc(sketch, "E145.0", {"start": v(-7, -15) * mm, "mid": v(-9.05, -10.05) * mm, "end": v(-14, -8) * mm});
            skLineSegment(sketch, "E146.0", {"start": v(-7, -15) * mm, "end": v(-7, -55) * mm});
            skArc(sketch, "E147.0", {"start": v(-55, 8) * mm, "mid": v(-63, 0) * mm, "end": v(-55, -8) * mm});
            skArc(sketch, "E148.0", {"start": v(-7, -55) * mm, "mid": v(0, -62) * mm, "end": v(7, -55) * mm});
            skArc(sketch, "E149.0", {"start": v(55, -6) * mm, "mid": v(61, 0) * mm, "end": v(55, 6) * mm});
            skArc(sketch, "E150.0", {"start": v(5, 55) * mm, "mid": v(0, 60) * mm, "end": v(-5, 55) * mm});
            skArc(sketch, "E151.0", {"start": v(-55, 8.3) * mm, "mid": v(-63.3, 0) * mm, "end": v(-55, -8.3) * mm});
            skLineSegment(sketch, "E151.1", {"start": v(-13, 8.3) * mm, "end": v(-55, 8.3) * mm});
            skArc(sketch, "E151.2", {"start": v(-13, 8.3) * mm, "mid": v(-7.56, 10.56) * mm, "end": v(-5.3, 16) * mm});
            skLineSegment(sketch, "E151.3", {"start": v(7.3, -55) * mm, "end": v(7.3, -12) * mm});
            skArc(sketch, "E151.4", {"start": v(-7.3, -55) * mm, "mid": v(0, -62.3) * mm, "end": v(7.3, -55) * mm});
            skLineSegment(sketch, "E151.5", {"start": v(-7.3, -15) * mm, "end": v(-7.3, -55) * mm});
            skArc(sketch, "E151.6", {"start": v(-7.3, -15) * mm, "mid": v(-9.26, -10.26) * mm, "end": v(-14, -8.3) * mm});
            skLineSegment(sketch, "E151.7", {"start": v(13, -6.3) * mm, "end": v(55, -6.3) * mm});
            skArc(sketch, "E151.8", {"start": v(55, -6.3) * mm, "mid": v(61.3, 0) * mm, "end": v(55, 6.3) * mm});
            skLineSegment(sketch, "E151.9", {"start": v(55, 6.3) * mm, "end": v(10, 6.3) * mm});
            skLineSegment(sketch, "E151.10", {"start": v(-55, -8.3) * mm, "end": v(-14, -8.3) * mm});
            skLineSegment(sketch, "E151.11", {"start": v(5.3, 11) * mm, "end": v(5.3, 55) * mm});
            skArc(sketch, "E151.12", {"start": v(5.3, 55) * mm, "mid": v(0, 60.3) * mm, "end": v(-5.3, 55) * mm});
            skLineSegment(sketch, "E151.13", {"start": v(-5.3, 55) * mm, "end": v(-5.3, 16) * mm});
            skPoint(sketch, "E152.visualSharp", {"position": v(7.3, -6.3) * mm});
            skArc(sketch, "E152.filletArc", {"start": v(13, -6.3) * mm, "mid": v(8.97, -7.97) * mm, "end": v(7.3, -12) * mm});
            skPoint(sketch, "E153.visualSharp", {"position": v(5.3, 6.3) * mm});
            skArc(sketch, "E154", {"start": v(5.3, 11) * mm, "mid": v(6.68, 7.68) * mm, "end": v(10, 6.3) * mm});
            skSolve(sketch);
        }
        {
            var Q0;
            Q0 = qSketchRegion(id + "F25", true);
            var Q1;
            {var subQ6=sQuery(id+"F25.wireOp",EDGE,"E135.0");Q1=makeQuery(id+"F25.imprint","IMPRINT",FACE,{"disambiguationData":[TD([[makeQuery(id+"F25.imprint","IMPRINT",EDGE,{"derivedFrom":subQ6}),1.0]])]});}
            extrude(context, id + "F26", {"entities" : qUnion([Q0, Q1]), "operationType" : NewBodyOperationType.REMOVE, "oppositeDirection" : true, "depth" : (getVariable(context, 'x3')) * mm, "offsetDistance" : 25 * mm});
        }
        {
            var Q0;
            {var subQ0=sQuery(id+"F15.wireOp",EDGE,"E96.trimOffspring");Q0=makeQuery(id+"F18.boolean.opBoolean","SPLIT",FACE,{"disambiguationData":[TD([makeQuery(id+"F16.opExtrude","SWEPT_FACE",FACE,{"disambiguationData":[OSD([subQ0])]})])],"derivedFrom":makeQuery(id+"F16.opExtrude","CAP_FACE",FACE,{"disambiguationData":[OSD([sQuery(id+"F15.wireOp",EDGE,"E94.0"),sQuery(id+"F15.wireOp",EDGE,"E94.1"),sQuery(id+"F15.wireOp",EDGE,"E94.2"),sQuery(id+"F15.wireOp",EDGE,"E94.3"),sQuery(id+"F15.wireOp",EDGE,"E94.4"),sQuery(id+"F15.wireOp",EDGE,"E94.5"),sQuery(id+"F15.wireOp",EDGE,"E94.6"),sQuery(id+"F15.wireOp",EDGE,"E94.7"),sQuery(id+"F15.wireOp",EDGE,"E94.8"),sQuery(id+"F15.wireOp",EDGE,"E94.9"),sQuery(id+"F15.wireOp",EDGE,"E94.10"),sQuery(id+"F15.wireOp",EDGE,"E94.11"),sQuery(id+"F15.wireOp",EDGE,"E94.12"),sQuery(id+"F15.wireOp",EDGE,"E94.13"),sQuery(id+"F15.wireOp",EDGE,"E94.14"),sQuery(id+"F15.wireOp",EDGE,"E94.15"),sQuery(id+"F15.wireOp",EDGE,"E95.0"),subQ0,sQuery(id+"F15.wireOp",EDGE,"E98.trimOffspring"),sQuery(id+"F15.wireOp",EDGE,"E100.trimOffspring"),sQuery(id+"F15.wireOp",EDGE,"E102.0"),sQuery(id+"F15.wireOp",EDGE,"E102.1"),sQuery(id+"F15.wireOp",EDGE,"E102.2"),sQuery(id+"F15.wireOp",EDGE,"E102.3"),sQuery(id+"F15.wireOp",EDGE,"E102.4"),sQuery(id+"F15.wireOp",EDGE,"E103.0"),sQuery(id+"F15.wireOp",EDGE,"E103.2"),sQuery(id+"F15.wireOp",EDGE,"E103.3"),sQuery(id+"F15.wireOp",EDGE,"E103.4"),sQuery(id+"F15.wireOp",EDGE,"E104.0"),sQuery(id+"F15.wireOp",EDGE,"E104.1"),sQuery(id+"F15.wireOp",EDGE,"E104.2"),sQuery(id+"F15.wireOp",EDGE,"E105.0"),sQuery(id+"F15.wireOp",EDGE,"E105.1"),sQuery(id+"F15.wireOp",EDGE,"E105.2"),sQuery(id+"F15.wireOp",EDGE,"E105.3")])],"isStart":true})});}
            var Q1;
            {var subQ0=sQuery(id+"F15.wireOp",EDGE,"E98.trimOffspring");Q1=makeQuery(id+"F18.boolean.opBoolean","SPLIT",FACE,{"disambiguationData":[TD([makeQuery(id+"F16.opExtrude","SWEPT_FACE",FACE,{"disambiguationData":[OSD([subQ0])]})])],"derivedFrom":makeQuery(id+"F16.opExtrude","CAP_FACE",FACE,{"disambiguationData":[OSD([sQuery(id+"F15.wireOp",EDGE,"E94.0"),sQuery(id+"F15.wireOp",EDGE,"E94.1"),sQuery(id+"F15.wireOp",EDGE,"E94.2"),sQuery(id+"F15.wireOp",EDGE,"E94.3"),sQuery(id+"F15.wireOp",EDGE,"E94.4"),sQuery(id+"F15.wireOp",EDGE,"E94.5"),sQuery(id+"F15.wireOp",EDGE,"E94.6"),sQuery(id+"F15.wireOp",EDGE,"E94.7"),sQuery(id+"F15.wireOp",EDGE,"E94.8"),sQuery(id+"F15.wireOp",EDGE,"E94.9"),sQuery(id+"F15.wireOp",EDGE,"E94.10"),sQuery(id+"F15.wireOp",EDGE,"E94.11"),sQuery(id+"F15.wireOp",EDGE,"E94.12"),sQuery(id+"F15.wireOp",EDGE,"E94.13"),sQuery(id+"F15.wireOp",EDGE,"E94.14"),sQuery(id+"F15.wireOp",EDGE,"E94.15"),sQuery(id+"F15.wireOp",EDGE,"E95.0"),sQuery(id+"F15.wireOp",EDGE,"E96.trimOffspring"),subQ0,sQuery(id+"F15.wireOp",EDGE,"E100.trimOffspring"),sQuery(id+"F15.wireOp",EDGE,"E102.0"),sQuery(id+"F15.wireOp",EDGE,"E102.1"),sQuery(id+"F15.wireOp",EDGE,"E102.2"),sQuery(id+"F15.wireOp",EDGE,"E102.3"),sQuery(id+"F15.wireOp",EDGE,"E102.4"),sQuery(id+"F15.wireOp",EDGE,"E103.0"),sQuery(id+"F15.wireOp",EDGE,"E103.2"),sQuery(id+"F15.wireOp",EDGE,"E103.3"),sQuery(id+"F15.wireOp",EDGE,"E103.4"),sQuery(id+"F15.wireOp",EDGE,"E104.0"),sQuery(id+"F15.wireOp",EDGE,"E104.1"),sQuery(id+"F15.wireOp",EDGE,"E104.2"),sQuery(id+"F15.wireOp",EDGE,"E105.0"),sQuery(id+"F15.wireOp",EDGE,"E105.1"),sQuery(id+"F15.wireOp",EDGE,"E105.2"),sQuery(id+"F15.wireOp",EDGE,"E105.3")])],"isStart":true})});}
            var Q2;
            {var subQ0=sQuery(id+"F15.wireOp",EDGE,"E100.trimOffspring");Q2=makeQuery(id+"F18.boolean.opBoolean","SPLIT",FACE,{"disambiguationData":[TD([makeQuery(id+"F18.opExtrude","SWEPT_FACE",FACE,{"disambiguationData":[OSD([sQuery(id+"F3.wireOp",EDGE,"E19.sketch_text.stroke-11")])]})])],"derivedFrom":makeQuery(id+"F16.opExtrude","CAP_FACE",FACE,{"disambiguationData":[OSD([sQuery(id+"F15.wireOp",EDGE,"E94.0"),sQuery(id+"F15.wireOp",EDGE,"E94.1"),sQuery(id+"F15.wireOp",EDGE,"E94.2"),sQuery(id+"F15.wireOp",EDGE,"E94.3"),sQuery(id+"F15.wireOp",EDGE,"E94.4"),sQuery(id+"F15.wireOp",EDGE,"E94.5"),sQuery(id+"F15.wireOp",EDGE,"E94.6"),sQuery(id+"F15.wireOp",EDGE,"E94.7"),sQuery(id+"F15.wireOp",EDGE,"E94.8"),sQuery(id+"F15.wireOp",EDGE,"E94.9"),sQuery(id+"F15.wireOp",EDGE,"E94.10"),sQuery(id+"F15.wireOp",EDGE,"E94.11"),sQuery(id+"F15.wireOp",EDGE,"E94.12"),sQuery(id+"F15.wireOp",EDGE,"E94.13"),sQuery(id+"F15.wireOp",EDGE,"E94.14"),sQuery(id+"F15.wireOp",EDGE,"E94.15"),sQuery(id+"F15.wireOp",EDGE,"E95.0"),sQuery(id+"F15.wireOp",EDGE,"E96.trimOffspring"),sQuery(id+"F15.wireOp",EDGE,"E98.trimOffspring"),subQ0,sQuery(id+"F15.wireOp",EDGE,"E102.0"),sQuery(id+"F15.wireOp",EDGE,"E102.1"),sQuery(id+"F15.wireOp",EDGE,"E102.2"),sQuery(id+"F15.wireOp",EDGE,"E102.3"),sQuery(id+"F15.wireOp",EDGE,"E102.4"),sQuery(id+"F15.wireOp",EDGE,"E103.0"),sQuery(id+"F15.wireOp",EDGE,"E103.2"),sQuery(id+"F15.wireOp",EDGE,"E103.3"),sQuery(id+"F15.wireOp",EDGE,"E103.4"),sQuery(id+"F15.wireOp",EDGE,"E104.0"),sQuery(id+"F15.wireOp",EDGE,"E104.1"),sQuery(id+"F15.wireOp",EDGE,"E104.2"),sQuery(id+"F15.wireOp",EDGE,"E105.0"),sQuery(id+"F15.wireOp",EDGE,"E105.1"),sQuery(id+"F15.wireOp",EDGE,"E105.2"),sQuery(id+"F15.wireOp",EDGE,"E105.3")])],"isStart":true})});}
            var Q3;
            {var subQ0=sQuery(id+"F15.wireOp",EDGE,"E100.trimOffspring");Q3=makeQuery(id+"F18.boolean.opBoolean","SPLIT",FACE,{"disambiguationData":[TD([makeQuery(id+"F18.opExtrude","SWEPT_FACE",FACE,{"disambiguationData":[OSD([sQuery(id+"F3.wireOp",EDGE,"E19.sketch_text.stroke-14")])]})])],"derivedFrom":makeQuery(id+"F16.opExtrude","CAP_FACE",FACE,{"disambiguationData":[OSD([sQuery(id+"F15.wireOp",EDGE,"E94.0"),sQuery(id+"F15.wireOp",EDGE,"E94.1"),sQuery(id+"F15.wireOp",EDGE,"E94.2"),sQuery(id+"F15.wireOp",EDGE,"E94.3"),sQuery(id+"F15.wireOp",EDGE,"E94.4"),sQuery(id+"F15.wireOp",EDGE,"E94.5"),sQuery(id+"F15.wireOp",EDGE,"E94.6"),sQuery(id+"F15.wireOp",EDGE,"E94.7"),sQuery(id+"F15.wireOp",EDGE,"E94.8"),sQuery(id+"F15.wireOp",EDGE,"E94.9"),sQuery(id+"F15.wireOp",EDGE,"E94.10"),sQuery(id+"F15.wireOp",EDGE,"E94.11"),sQuery(id+"F15.wireOp",EDGE,"E94.12"),sQuery(id+"F15.wireOp",EDGE,"E94.13"),sQuery(id+"F15.wireOp",EDGE,"E94.14"),sQuery(id+"F15.wireOp",EDGE,"E94.15"),sQuery(id+"F15.wireOp",EDGE,"E95.0"),sQuery(id+"F15.wireOp",EDGE,"E96.trimOffspring"),sQuery(id+"F15.wireOp",EDGE,"E98.trimOffspring"),subQ0,sQuery(id+"F15.wireOp",EDGE,"E102.0"),sQuery(id+"F15.wireOp",EDGE,"E102.1"),sQuery(id+"F15.wireOp",EDGE,"E102.2"),sQuery(id+"F15.wireOp",EDGE,"E102.3"),sQuery(id+"F15.wireOp",EDGE,"E102.4"),sQuery(id+"F15.wireOp",EDGE,"E103.0"),sQuery(id+"F15.wireOp",EDGE,"E103.2"),sQuery(id+"F15.wireOp",EDGE,"E103.3"),sQuery(id+"F15.wireOp",EDGE,"E103.4"),sQuery(id+"F15.wireOp",EDGE,"E104.0"),sQuery(id+"F15.wireOp",EDGE,"E104.1"),sQuery(id+"F15.wireOp",EDGE,"E104.2"),sQuery(id+"F15.wireOp",EDGE,"E105.0"),sQuery(id+"F15.wireOp",EDGE,"E105.1"),sQuery(id+"F15.wireOp",EDGE,"E105.2"),sQuery(id+"F15.wireOp",EDGE,"E105.3")])],"isStart":true})});}
            var Q4;
            {var subQ0=sQuery(id+"F15.wireOp",EDGE,"E95.0");Q4=makeQuery(id+"F18.boolean.opBoolean","SPLIT",FACE,{"disambiguationData":[TD([makeQuery(id+"F16.opExtrude","SWEPT_FACE",FACE,{"disambiguationData":[OSD([subQ0])]})])],"derivedFrom":makeQuery(id+"F16.opExtrude","CAP_FACE",FACE,{"disambiguationData":[OSD([sQuery(id+"F15.wireOp",EDGE,"E94.0"),sQuery(id+"F15.wireOp",EDGE,"E94.1"),sQuery(id+"F15.wireOp",EDGE,"E94.2"),sQuery(id+"F15.wireOp",EDGE,"E94.3"),sQuery(id+"F15.wireOp",EDGE,"E94.4"),sQuery(id+"F15.wireOp",EDGE,"E94.5"),sQuery(id+"F15.wireOp",EDGE,"E94.6"),sQuery(id+"F15.wireOp",EDGE,"E94.7"),sQuery(id+"F15.wireOp",EDGE,"E94.8"),sQuery(id+"F15.wireOp",EDGE,"E94.9"),sQuery(id+"F15.wireOp",EDGE,"E94.10"),sQuery(id+"F15.wireOp",EDGE,"E94.11"),sQuery(id+"F15.wireOp",EDGE,"E94.12"),sQuery(id+"F15.wireOp",EDGE,"E94.13"),sQuery(id+"F15.wireOp",EDGE,"E94.14"),sQuery(id+"F15.wireOp",EDGE,"E94.15"),subQ0,sQuery(id+"F15.wireOp",EDGE,"E96.trimOffspring"),sQuery(id+"F15.wireOp",EDGE,"E98.trimOffspring"),sQuery(id+"F15.wireOp",EDGE,"E100.trimOffspring"),sQuery(id+"F15.wireOp",EDGE,"E102.0"),sQuery(id+"F15.wireOp",EDGE,"E102.1"),sQuery(id+"F15.wireOp",EDGE,"E102.2"),sQuery(id+"F15.wireOp",EDGE,"E102.3"),sQuery(id+"F15.wireOp",EDGE,"E102.4"),sQuery(id+"F15.wireOp",EDGE,"E103.0"),sQuery(id+"F15.wireOp",EDGE,"E103.2"),sQuery(id+"F15.wireOp",EDGE,"E103.3"),sQuery(id+"F15.wireOp",EDGE,"E103.4"),sQuery(id+"F15.wireOp",EDGE,"E104.0"),sQuery(id+"F15.wireOp",EDGE,"E104.1"),sQuery(id+"F15.wireOp",EDGE,"E104.2"),sQuery(id+"F15.wireOp",EDGE,"E105.0"),sQuery(id+"F15.wireOp",EDGE,"E105.1"),sQuery(id+"F15.wireOp",EDGE,"E105.2"),sQuery(id+"F15.wireOp",EDGE,"E105.3")])],"isStart":true})});}
            var Q5;
            Q5=makeQuery(id+"F18.boolean.opBoolean","SPLIT",FACE,{"disambiguationData":[TD([makeQuery(id+"F18.opExtrude","SWEPT_FACE",FACE,{"disambiguationData":[OSD([sQuery(id+"F3.wireOp",EDGE,"E16")])]})])],"derivedFrom":makeQuery(id+"F16.opExtrude","CAP_FACE",FACE,{"disambiguationData":[OSD([sQuery(id+"F15.wireOp",EDGE,"E94.0"),sQuery(id+"F15.wireOp",EDGE,"E94.1"),sQuery(id+"F15.wireOp",EDGE,"E94.2"),sQuery(id+"F15.wireOp",EDGE,"E94.3"),sQuery(id+"F15.wireOp",EDGE,"E94.4"),sQuery(id+"F15.wireOp",EDGE,"E94.5"),sQuery(id+"F15.wireOp",EDGE,"E94.6"),sQuery(id+"F15.wireOp",EDGE,"E94.7"),sQuery(id+"F15.wireOp",EDGE,"E94.8"),sQuery(id+"F15.wireOp",EDGE,"E94.9"),sQuery(id+"F15.wireOp",EDGE,"E94.10"),sQuery(id+"F15.wireOp",EDGE,"E94.11"),sQuery(id+"F15.wireOp",EDGE,"E94.12"),sQuery(id+"F15.wireOp",EDGE,"E94.13"),sQuery(id+"F15.wireOp",EDGE,"E94.14"),sQuery(id+"F15.wireOp",EDGE,"E94.15"),sQuery(id+"F15.wireOp",EDGE,"E95.0"),sQuery(id+"F15.wireOp",EDGE,"E96.trimOffspring"),sQuery(id+"F15.wireOp",EDGE,"E98.trimOffspring"),sQuery(id+"F15.wireOp",EDGE,"E100.trimOffspring"),sQuery(id+"F15.wireOp",EDGE,"E102.0"),sQuery(id+"F15.wireOp",EDGE,"E102.1"),sQuery(id+"F15.wireOp",EDGE,"E102.2"),sQuery(id+"F15.wireOp",EDGE,"E102.3"),sQuery(id+"F15.wireOp",EDGE,"E102.4"),sQuery(id+"F15.wireOp",EDGE,"E103.0"),sQuery(id+"F15.wireOp",EDGE,"E103.2"),sQuery(id+"F15.wireOp",EDGE,"E103.3"),sQuery(id+"F15.wireOp",EDGE,"E103.4"),sQuery(id+"F15.wireOp",EDGE,"E104.0"),sQuery(id+"F15.wireOp",EDGE,"E104.1"),sQuery(id+"F15.wireOp",EDGE,"E104.2"),sQuery(id+"F15.wireOp",EDGE,"E105.0"),sQuery(id+"F15.wireOp",EDGE,"E105.1"),sQuery(id+"F15.wireOp",EDGE,"E105.2"),sQuery(id+"F15.wireOp",EDGE,"E105.3")])],"isStart":true})});
            var Q6;
            Q6=makeQuery(id+"F18.boolean.opBoolean","MERGE",FACE,{"derivedFrom":[],"fromTools":[makeQuery(id+"F18.opExtrude","CAP_FACE",FACE,{"disambiguationData":[OSD([sQuery(id+"F3.wireOp",EDGE,"E0"),sQuery(id+"F3.wireOp",EDGE,"E1"),sQuery(id+"F3.wireOp",EDGE,"E2"),sQuery(id+"F3.wireOp",EDGE,"E3"),sQuery(id+"F3.wireOp",EDGE,"E4"),sQuery(id+"F3.wireOp",EDGE,"E5"),sQuery(id+"F3.wireOp",EDGE,"E6"),sQuery(id+"F3.wireOp",EDGE,"E7"),sQuery(id+"F3.wireOp",EDGE,"E8"),sQuery(id+"F3.wireOp",EDGE,"E9"),sQuery(id+"F3.wireOp",EDGE,"E10"),sQuery(id+"F3.wireOp",EDGE,"E11"),sQuery(id+"F3.wireOp",EDGE,"E12.filletArc"),sQuery(id+"F3.wireOp",EDGE,"E13.filletArc"),sQuery(id+"F3.wireOp",EDGE,"E14.filletArc"),sQuery(id+"F3.wireOp",EDGE,"E15.filletArc"),sQuery(id+"F3.wireOp",EDGE,"E16"),sQuery(id+"F3.wireOp",EDGE,"E17.sketch_text.stroke-0"),sQuery(id+"F3.wireOp",EDGE,"E17.sketch_text.stroke-1"),sQuery(id+"F3.wireOp",EDGE,"E17.sketch_text.stroke-2"),sQuery(id+"F3.wireOp",EDGE,"E17.sketch_text.stroke-3"),sQuery(id+"F3.wireOp",EDGE,"E17.sketch_text.stroke-4"),sQuery(id+"F3.wireOp",EDGE,"E17.sketch_text.stroke-5"),sQuery(id+"F3.wireOp",EDGE,"E17.sketch_text.stroke-6"),sQuery(id+"F3.wireOp",EDGE,"E17.sketch_text.stroke-7"),sQuery(id+"F3.wireOp",EDGE,"E17.sketch_text.stroke-8"),sQuery(id+"F3.wireOp",EDGE,"E17.sketch_text.stroke-9"),sQuery(id+"F3.wireOp",EDGE,"E17.sketch_text.stroke-10"),sQuery(id+"F3.wireOp",EDGE,"E17.sketch_text.stroke-11"),sQuery(id+"F3.wireOp",EDGE,"E17.sketch_text.stroke-12"),sQuery(id+"F3.wireOp",EDGE,"E17.sketch_text.stroke-13"),sQuery(id+"F3.wireOp",EDGE,"E17.sketch_text.stroke-14"),sQuery(id+"F3.wireOp",EDGE,"E17.sketch_text.stroke-15"),sQuery(id+"F3.wireOp",EDGE,"E17.sketch_text.stroke-16"),sQuery(id+"F3.wireOp",EDGE,"E17.sketch_text.stroke-17"),sQuery(id+"F3.wireOp",EDGE,"E17.sketch_text.stroke-18"),sQuery(id+"F3.wireOp",EDGE,"E17.sketch_text.stroke-19"),sQuery(id+"F3.wireOp",EDGE,"E17.sketch_text.stroke-20"),sQuery(id+"F3.wireOp",EDGE,"E17.sketch_text.stroke-21"),sQuery(id+"F3.wireOp",EDGE,"E17.sketch_text.stroke-22"),sQuery(id+"F3.wireOp",EDGE,"E17.sketch_text.stroke-23"),sQuery(id+"F3.wireOp",EDGE,"E17.sketch_text.stroke-24"),sQuery(id+"F3.wireOp",EDGE,"E17.sketch_text.stroke-25"),sQuery(id+"F3.wireOp",EDGE,"E17.sketch_text.stroke-26"),sQuery(id+"F3.wireOp",EDGE,"E17.sketch_text.stroke-27"),sQuery(id+"F3.wireOp",EDGE,"E17.sketch_text.stroke-28"),sQuery(id+"F3.wireOp",EDGE,"E17.sketch_text.stroke-29"),sQuery(id+"F3.wireOp",EDGE,"E17.sketch_text.stroke-30"),sQuery(id+"F3.wireOp",EDGE,"E17.sketch_text.stroke-31"),sQuery(id+"F3.wireOp",EDGE,"E18.sketch_text.stroke-0"),sQuery(id+"F3.wireOp",EDGE,"E18.sketch_text.stroke-1"),sQuery(id+"F3.wireOp",EDGE,"E18.sketch_text.stroke-2"),sQuery(id+"F3.wireOp",EDGE,"E18.sketch_text.stroke-3"),sQuery(id+"F3.wireOp",EDGE,"E18.sketch_text.stroke-4"),sQuery(id+"F3.wireOp",EDGE,"E18.sketch_text.stroke-5"),sQuery(id+"F3.wireOp",EDGE,"E18.sketch_text.stroke-6"),sQuery(id+"F3.wireOp",EDGE,"E18.sketch_text.stroke-7"),sQuery(id+"F3.wireOp",EDGE,"E18.sketch_text.stroke-8"),sQuery(id+"F3.wireOp",EDGE,"E18.sketch_text.stroke-9"),sQuery(id+"F3.wireOp",EDGE,"E18.sketch_text.stroke-10"),sQuery(id+"F3.wireOp",EDGE,"E18.sketch_text.stroke-11"),sQuery(id+"F3.wireOp",EDGE,"E18.sketch_text.stroke-12"),sQuery(id+"F3.wireOp",EDGE,"E18.sketch_text.stroke-13"),sQuery(id+"F3.wireOp",EDGE,"E18.sketch_text.stroke-14"),sQuery(id+"F3.wireOp",EDGE,"E18.sketch_text.stroke-15"),sQuery(id+"F3.wireOp",EDGE,"E18.sketch_text.stroke-16"),sQuery(id+"F3.wireOp",EDGE,"E18.sketch_text.stroke-17"),sQuery(id+"F3.wireOp",EDGE,"E18.sketch_text.stroke-18"),sQuery(id+"F3.wireOp",EDGE,"E18.sketch_text.stroke-19"),sQuery(id+"F3.wireOp",EDGE,"E18.sketch_text.stroke-20"),sQuery(id+"F3.wireOp",EDGE,"E18.sketch_text.stroke-21"),sQuery(id+"F3.wireOp",EDGE,"E18.sketch_text.stroke-22"),sQuery(id+"F3.wireOp",EDGE,"E18.sketch_text.stroke-23"),sQuery(id+"F3.wireOp",EDGE,"E18.sketch_text.stroke-24"),sQuery(id+"F3.wireOp",EDGE,"E18.sketch_text.stroke-25"),sQuery(id+"F3.wireOp",EDGE,"E18.sketch_text.stroke-26"),sQuery(id+"F3.wireOp",EDGE,"E18.sketch_text.stroke-27"),sQuery(id+"F3.wireOp",EDGE,"E19.sketch_text.stroke-0"),sQuery(id+"F3.wireOp",EDGE,"E19.sketch_text.stroke-1"),sQuery(id+"F3.wireOp",EDGE,"E19.sketch_text.stroke-2"),sQuery(id+"F3.wireOp",EDGE,"E19.sketch_text.stroke-3"),sQuery(id+"F3.wireOp",EDGE,"E19.sketch_text.stroke-4"),sQuery(id+"F3.wireOp",EDGE,"E19.sketch_text.stroke-5"),sQuery(id+"F3.wireOp",EDGE,"E19.sketch_text.stroke-6"),sQuery(id+"F3.wireOp",EDGE,"E19.sketch_text.stroke-7"),sQuery(id+"F3.wireOp",EDGE,"E19.sketch_text.stroke-8"),sQuery(id+"F3.wireOp",EDGE,"E19.sketch_text.stroke-9"),sQuery(id+"F3.wireOp",EDGE,"E19.sketch_text.stroke-10"),sQuery(id+"F3.wireOp",EDGE,"E19.sketch_text.stroke-11"),sQuery(id+"F3.wireOp",EDGE,"E19.sketch_text.stroke-12"),sQuery(id+"F3.wireOp",EDGE,"E19.sketch_text.stroke-13"),sQuery(id+"F3.wireOp",EDGE,"E19.sketch_text.stroke-14"),sQuery(id+"F3.wireOp",EDGE,"E19.sketch_text.stroke-15"),sQuery(id+"F3.wireOp",EDGE,"E19.sketch_text.stroke-16"),sQuery(id+"F3.wireOp",EDGE,"E19.sketch_text.stroke-17"),sQuery(id+"F3.wireOp",EDGE,"E19.sketch_text.stroke-18"),sQuery(id+"F3.wireOp",EDGE,"E19.sketch_text.stroke-19"),sQuery(id+"F3.wireOp",EDGE,"E19.sketch_text.stroke-20"),sQuery(id+"F3.wireOp",EDGE,"E19.sketch_text.stroke-21"),sQuery(id+"F3.wireOp",EDGE,"E19.sketch_text.stroke-22"),sQuery(id+"F3.wireOp",EDGE,"E19.sketch_text.stroke-23"),sQuery(id+"F3.wireOp",EDGE,"E19.sketch_text.stroke-24"),sQuery(id+"F3.wireOp",EDGE,"E19.sketch_text.stroke-25"),sQuery(id+"F3.wireOp",EDGE,"E20.sketch_text.stroke-0"),sQuery(id+"F3.wireOp",EDGE,"E20.sketch_text.stroke-1"),sQuery(id+"F3.wireOp",EDGE,"E20.sketch_text.stroke-2"),sQuery(id+"F3.wireOp",EDGE,"E20.sketch_text.stroke-3"),sQuery(id+"F3.wireOp",EDGE,"E20.sketch_text.stroke-4"),sQuery(id+"F3.wireOp",EDGE,"E20.sketch_text.stroke-5"),sQuery(id+"F3.wireOp",EDGE,"E20.sketch_text.stroke-6"),sQuery(id+"F3.wireOp",EDGE,"E20.sketch_text.stroke-7"),sQuery(id+"F3.wireOp",EDGE,"E20.sketch_text.stroke-8"),sQuery(id+"F3.wireOp",EDGE,"E20.sketch_text.stroke-9"),sQuery(id+"F3.wireOp",EDGE,"E20.sketch_text.stroke-10"),sQuery(id+"F3.wireOp",EDGE,"E20.sketch_text.stroke-11"),sQuery(id+"F3.wireOp",EDGE,"E20.sketch_text.stroke-12"),sQuery(id+"F3.wireOp",EDGE,"E20.sketch_text.stroke-13"),sQuery(id+"F3.wireOp",EDGE,"E20.sketch_text.stroke-14"),sQuery(id+"F3.wireOp",EDGE,"E20.sketch_text.stroke-15"),sQuery(id+"F3.wireOp",EDGE,"E20.sketch_text.stroke-16")])],"isStart":false}),makeQuery(id+"F18.opExtrude","CAP_FACE",FACE,{"disambiguationData":[OSD([sQuery(id+"F17.wireOp",EDGE,"E106.0.0"),sQuery(id+"F17.wireOp",EDGE,"E106.0.1"),sQuery(id+"F17.wireOp",EDGE,"E106.0.2"),sQuery(id+"F17.wireOp",EDGE,"E106.0.3"),sQuery(id+"F17.wireOp",EDGE,"E106.0.4"),sQuery(id+"F17.wireOp",EDGE,"E106.0.5"),sQuery(id+"F17.wireOp",EDGE,"E106.0.6"),sQuery(id+"F17.wireOp",EDGE,"E106.0.7"),sQuery(id+"F17.wireOp",EDGE,"E106.0.8"),sQuery(id+"F17.wireOp",EDGE,"E106.0.9"),sQuery(id+"F17.wireOp",EDGE,"E106.0.10"),sQuery(id+"F17.wireOp",EDGE,"E106.0.11"),sQuery(id+"F17.wireOp",EDGE,"E106.0.12"),sQuery(id+"F17.wireOp",EDGE,"E106.0.13"),sQuery(id+"F17.wireOp",EDGE,"E106.0.14"),sQuery(id+"F17.wireOp",EDGE,"E106.0.15"),sQuery(id+"F17.wireOp",EDGE,"E107.0"),sQuery(id+"F17.wireOp",EDGE,"E107.1"),sQuery(id+"F17.wireOp",EDGE,"E107.2"),sQuery(id+"F17.wireOp",EDGE,"E107.3"),sQuery(id+"F17.wireOp",EDGE,"E107.4"),sQuery(id+"F17.wireOp",EDGE,"E107.5"),sQuery(id+"F17.wireOp",EDGE,"E107.6"),sQuery(id+"F17.wireOp",EDGE,"E107.7"),sQuery(id+"F17.wireOp",EDGE,"E107.8"),sQuery(id+"F17.wireOp",EDGE,"E107.9"),sQuery(id+"F17.wireOp",EDGE,"E107.10"),sQuery(id+"F17.wireOp",EDGE,"E107.11"),sQuery(id+"F17.wireOp",EDGE,"E107.12"),sQuery(id+"F17.wireOp",EDGE,"E107.13"),sQuery(id+"F17.wireOp",EDGE,"E107.14"),sQuery(id+"F17.wireOp",EDGE,"E107.15")])],"isStart":false})]});
            extrude(context, id + "F27", {"entities" : qUnion([Q0, Q1, Q2, Q3, Q4, Q5]), "operationType" : NewBodyOperationType.REMOVE, "endBound" : BoundingType.UP_TO_SURFACE, "oppositeDirection" : true, "depth" : 25 * mm, "endBoundEntityFace" : qUnion([Q6]), "offsetDistance" : 25 * mm});
        }
        {
            var Q0;
            {var subQ0=sQuery(id+"F3.wireOp",EDGE,"E19.sketch_text.stroke-16");var subQ1=sQuery(id+"F3.wireOp",EDGE,"E19.sketch_text.stroke-15");var subQ2=sQuery(id+"F3.wireOp",EDGE,"E19.sketch_text.stroke-14");var subQ3=sQuery(id+"F15.wireOp",EDGE,"E100.trimOffspring");var subQ5=sQuery(id+"F3.wireOp",EDGE,"E19.sketch_text.stroke-17");var subQ6=sQuery(id+"F15.wireOp",EDGE,"E105.3");var subQ7=sQuery(id+"F15.wireOp",EDGE,"E105.2");var subQ8=sQuery(id+"F15.wireOp",EDGE,"E105.1");var subQ9=sQuery(id+"F15.wireOp",EDGE,"E105.0");var subQ10=sQuery(id+"F15.wireOp",EDGE,"E104.2");var subQ11=sQuery(id+"F15.wireOp",EDGE,"E104.1");var subQ12=sQuery(id+"F15.wireOp",EDGE,"E104.0");var subQ13=sQuery(id+"F15.wireOp",EDGE,"E103.4");var subQ14=sQuery(id+"F15.wireOp",EDGE,"E103.3");var subQ15=sQuery(id+"F15.wireOp",EDGE,"E103.2");var subQ16=sQuery(id+"F15.wireOp",EDGE,"E103.0");var subQ17=sQuery(id+"F15.wireOp",EDGE,"E102.4");var subQ18=sQuery(id+"F15.wireOp",EDGE,"E102.3");var subQ19=sQuery(id+"F15.wireOp",EDGE,"E102.2");var subQ20=sQuery(id+"F15.wireOp",EDGE,"E102.1");var subQ21=sQuery(id+"F15.wireOp",EDGE,"E102.0");var subQ22=sQuery(id+"F15.wireOp",EDGE,"E98.trimOffspring");var subQ23=sQuery(id+"F15.wireOp",EDGE,"E96.trimOffspring");var subQ24=sQuery(id+"F15.wireOp",EDGE,"E95.0");var subQ25=sQuery(id+"F15.wireOp",EDGE,"E94.15");var subQ26=sQuery(id+"F15.wireOp",EDGE,"E94.14");var subQ27=sQuery(id+"F15.wireOp",EDGE,"E94.13");var subQ28=sQuery(id+"F15.wireOp",EDGE,"E94.12");var subQ29=sQuery(id+"F15.wireOp",EDGE,"E94.11");var subQ30=sQuery(id+"F15.wireOp",EDGE,"E94.10");var subQ31=sQuery(id+"F15.wireOp",EDGE,"E94.9");var subQ32=sQuery(id+"F15.wireOp",EDGE,"E94.8");var subQ33=sQuery(id+"F15.wireOp",EDGE,"E94.7");var subQ34=sQuery(id+"F15.wireOp",EDGE,"E94.6");var subQ35=sQuery(id+"F15.wireOp",EDGE,"E94.5");var subQ36=sQuery(id+"F15.wireOp",EDGE,"E94.4");var subQ37=sQuery(id+"F15.wireOp",EDGE,"E94.3");var subQ38=sQuery(id+"F15.wireOp",EDGE,"E94.2");var subQ39=sQuery(id+"F15.wireOp",EDGE,"E94.1");var subQ40=sQuery(id+"F15.wireOp",EDGE,"E94.0");var subQ41=makeQuery(id+"F16.opExtrude","CAP_FACE",FACE,{"disambiguationData":[OSD([subQ40,subQ39,subQ38,subQ37,subQ36,subQ35,subQ34,subQ33,subQ32,subQ31,subQ30,subQ29,subQ28,subQ27,subQ26,subQ25,subQ24,subQ23,subQ22,subQ3,subQ21,subQ20,subQ19,subQ18,subQ17,subQ16,subQ15,subQ14,subQ13,subQ12,subQ11,subQ10,subQ9,subQ8,subQ7,subQ6])],"isStart":true});var subQ42=sQuery(id+"F3.wireOp",EDGE,"E17.sketch_text.stroke-24");var subQ43=sQuery(id+"F3.wireOp",EDGE,"E17.sketch_text.stroke-25");var subQ44=sQuery(id+"F3.wireOp",EDGE,"E17.sketch_text.stroke-31");var subQ45=sQuery(id+"F3.wireOp",EDGE,"E19.sketch_text.stroke-11");var subQ46=sQuery(id+"F3.wireOp",EDGE,"E19.sketch_text.stroke-12");var subQ47=sQuery(id+"F3.wireOp",EDGE,"E18.sketch_text.stroke-10");var subQ48=sQuery(id+"F3.wireOp",EDGE,"E18.sketch_text.stroke-27");var subQ49=sQuery(id+"F3.wireOp",EDGE,"E20.sketch_text.stroke-15");var subQ50=sQuery(id+"F3.wireOp",EDGE,"E20.sketch_text.stroke-14");var subQ51=sQuery(id+"F3.wireOp",EDGE,"E16");Q0=makeQuery(id+"F27.boolean.opBoolean","MERGE",FACE,{"derivedFrom":[makeQuery(id+"F18.boolean.opBoolean","MERGE",FACE,{"derivedFrom":[],"fromTools":[makeQuery(id+"F18.opExtrude","CAP_FACE",FACE,{"disambiguationData":[OSD([sQuery(id+"F3.wireOp",EDGE,"E0"),sQuery(id+"F3.wireOp",EDGE,"E1"),sQuery(id+"F3.wireOp",EDGE,"E2"),sQuery(id+"F3.wireOp",EDGE,"E3"),sQuery(id+"F3.wireOp",EDGE,"E4"),sQuery(id+"F3.wireOp",EDGE,"E5"),sQuery(id+"F3.wireOp",EDGE,"E6"),sQuery(id+"F3.wireOp",EDGE,"E7"),sQuery(id+"F3.wireOp",EDGE,"E8"),sQuery(id+"F3.wireOp",EDGE,"E9"),sQuery(id+"F3.wireOp",EDGE,"E10"),sQuery(id+"F3.wireOp",EDGE,"E11"),sQuery(id+"F3.wireOp",EDGE,"E12.filletArc"),sQuery(id+"F3.wireOp",EDGE,"E13.filletArc"),sQuery(id+"F3.wireOp",EDGE,"E14.filletArc"),sQuery(id+"F3.wireOp",EDGE,"E15.filletArc"),subQ51,sQuery(id+"F3.wireOp",EDGE,"E17.sketch_text.stroke-0"),sQuery(id+"F3.wireOp",EDGE,"E17.sketch_text.stroke-1"),sQuery(id+"F3.wireOp",EDGE,"E17.sketch_text.stroke-2"),sQuery(id+"F3.wireOp",EDGE,"E17.sketch_text.stroke-3"),sQuery(id+"F3.wireOp",EDGE,"E17.sketch_text.stroke-4"),sQuery(id+"F3.wireOp",EDGE,"E17.sketch_text.stroke-5"),sQuery(id+"F3.wireOp",EDGE,"E17.sketch_text.stroke-6"),sQuery(id+"F3.wireOp",EDGE,"E17.sketch_text.stroke-7"),sQuery(id+"F3.wireOp",EDGE,"E17.sketch_text.stroke-8"),sQuery(id+"F3.wireOp",EDGE,"E17.sketch_text.stroke-9"),sQuery(id+"F3.wireOp",EDGE,"E17.sketch_text.stroke-10"),sQuery(id+"F3.wireOp",EDGE,"E17.sketch_text.stroke-11"),sQuery(id+"F3.wireOp",EDGE,"E17.sketch_text.stroke-12"),sQuery(id+"F3.wireOp",EDGE,"E17.sketch_text.stroke-13"),sQuery(id+"F3.wireOp",EDGE,"E17.sketch_text.stroke-14"),sQuery(id+"F3.wireOp",EDGE,"E17.sketch_text.stroke-15"),sQuery(id+"F3.wireOp",EDGE,"E17.sketch_text.stroke-16"),sQuery(id+"F3.wireOp",EDGE,"E17.sketch_text.stroke-17"),sQuery(id+"F3.wireOp",EDGE,"E17.sketch_text.stroke-18"),sQuery(id+"F3.wireOp",EDGE,"E17.sketch_text.stroke-19"),sQuery(id+"F3.wireOp",EDGE,"E17.sketch_text.stroke-20"),sQuery(id+"F3.wireOp",EDGE,"E17.sketch_text.stroke-21"),sQuery(id+"F3.wireOp",EDGE,"E17.sketch_text.stroke-22"),sQuery(id+"F3.wireOp",EDGE,"E17.sketch_text.stroke-23"),subQ42,subQ43,sQuery(id+"F3.wireOp",EDGE,"E17.sketch_text.stroke-26"),sQuery(id+"F3.wireOp",EDGE,"E17.sketch_text.stroke-27"),sQuery(id+"F3.wireOp",EDGE,"E17.sketch_text.stroke-28"),sQuery(id+"F3.wireOp",EDGE,"E17.sketch_text.stroke-29"),sQuery(id+"F3.wireOp",EDGE,"E17.sketch_text.stroke-30"),subQ44,sQuery(id+"F3.wireOp",EDGE,"E18.sketch_text.stroke-0"),sQuery(id+"F3.wireOp",EDGE,"E18.sketch_text.stroke-1"),sQuery(id+"F3.wireOp",EDGE,"E18.sketch_text.stroke-2"),sQuery(id+"F3.wireOp",EDGE,"E18.sketch_text.stroke-3"),sQuery(id+"F3.wireOp",EDGE,"E18.sketch_text.stroke-4"),sQuery(id+"F3.wireOp",EDGE,"E18.sketch_text.stroke-5"),sQuery(id+"F3.wireOp",EDGE,"E18.sketch_text.stroke-6"),sQuery(id+"F3.wireOp",EDGE,"E18.sketch_text.stroke-7"),sQuery(id+"F3.wireOp",EDGE,"E18.sketch_text.stroke-8"),sQuery(id+"F3.wireOp",EDGE,"E18.sketch_text.stroke-9"),subQ47,sQuery(id+"F3.wireOp",EDGE,"E18.sketch_text.stroke-11"),sQuery(id+"F3.wireOp",EDGE,"E18.sketch_text.stroke-12"),sQuery(id+"F3.wireOp",EDGE,"E18.sketch_text.stroke-13"),sQuery(id+"F3.wireOp",EDGE,"E18.sketch_text.stroke-14"),sQuery(id+"F3.wireOp",EDGE,"E18.sketch_text.stroke-15"),sQuery(id+"F3.wireOp",EDGE,"E18.sketch_text.stroke-16"),sQuery(id+"F3.wireOp",EDGE,"E18.sketch_text.stroke-17"),sQuery(id+"F3.wireOp",EDGE,"E18.sketch_text.stroke-18"),sQuery(id+"F3.wireOp",EDGE,"E18.sketch_text.stroke-19"),sQuery(id+"F3.wireOp",EDGE,"E18.sketch_text.stroke-20"),sQuery(id+"F3.wireOp",EDGE,"E18.sketch_text.stroke-21"),sQuery(id+"F3.wireOp",EDGE,"E18.sketch_text.stroke-22"),sQuery(id+"F3.wireOp",EDGE,"E18.sketch_text.stroke-23"),sQuery(id+"F3.wireOp",EDGE,"E18.sketch_text.stroke-24"),sQuery(id+"F3.wireOp",EDGE,"E18.sketch_text.stroke-25"),sQuery(id+"F3.wireOp",EDGE,"E18.sketch_text.stroke-26"),subQ48,sQuery(id+"F3.wireOp",EDGE,"E19.sketch_text.stroke-0"),sQuery(id+"F3.wireOp",EDGE,"E19.sketch_text.stroke-1"),sQuery(id+"F3.wireOp",EDGE,"E19.sketch_text.stroke-2"),sQuery(id+"F3.wireOp",EDGE,"E19.sketch_text.stroke-3"),sQuery(id+"F3.wireOp",EDGE,"E19.sketch_text.stroke-4"),sQuery(id+"F3.wireOp",EDGE,"E19.sketch_text.stroke-5"),sQuery(id+"F3.wireOp",EDGE,"E19.sketch_text.stroke-6"),sQuery(id+"F3.wireOp",EDGE,"E19.sketch_text.stroke-7"),sQuery(id+"F3.wireOp",EDGE,"E19.sketch_text.stroke-8"),sQuery(id+"F3.wireOp",EDGE,"E19.sketch_text.stroke-9"),sQuery(id+"F3.wireOp",EDGE,"E19.sketch_text.stroke-10"),subQ45,subQ46,sQuery(id+"F3.wireOp",EDGE,"E19.sketch_text.stroke-13"),subQ2,subQ1,subQ0,subQ5,sQuery(id+"F3.wireOp",EDGE,"E19.sketch_text.stroke-18"),sQuery(id+"F3.wireOp",EDGE,"E19.sketch_text.stroke-19"),sQuery(id+"F3.wireOp",EDGE,"E19.sketch_text.stroke-20"),sQuery(id+"F3.wireOp",EDGE,"E19.sketch_text.stroke-21"),sQuery(id+"F3.wireOp",EDGE,"E19.sketch_text.stroke-22"),sQuery(id+"F3.wireOp",EDGE,"E19.sketch_text.stroke-23"),sQuery(id+"F3.wireOp",EDGE,"E19.sketch_text.stroke-24"),sQuery(id+"F3.wireOp",EDGE,"E19.sketch_text.stroke-25"),sQuery(id+"F3.wireOp",EDGE,"E20.sketch_text.stroke-0"),sQuery(id+"F3.wireOp",EDGE,"E20.sketch_text.stroke-1"),sQuery(id+"F3.wireOp",EDGE,"E20.sketch_text.stroke-2"),sQuery(id+"F3.wireOp",EDGE,"E20.sketch_text.stroke-3"),sQuery(id+"F3.wireOp",EDGE,"E20.sketch_text.stroke-4"),sQuery(id+"F3.wireOp",EDGE,"E20.sketch_text.stroke-5"),sQuery(id+"F3.wireOp",EDGE,"E20.sketch_text.stroke-6"),sQuery(id+"F3.wireOp",EDGE,"E20.sketch_text.stroke-7"),sQuery(id+"F3.wireOp",EDGE,"E20.sketch_text.stroke-8"),sQuery(id+"F3.wireOp",EDGE,"E20.sketch_text.stroke-9"),sQuery(id+"F3.wireOp",EDGE,"E20.sketch_text.stroke-10"),sQuery(id+"F3.wireOp",EDGE,"E20.sketch_text.stroke-11"),sQuery(id+"F3.wireOp",EDGE,"E20.sketch_text.stroke-12"),sQuery(id+"F3.wireOp",EDGE,"E20.sketch_text.stroke-13"),subQ50,subQ49,sQuery(id+"F3.wireOp",EDGE,"E20.sketch_text.stroke-16")])],"isStart":false}),makeQuery(id+"F18.opExtrude","CAP_FACE",FACE,{"disambiguationData":[OSD([sQuery(id+"F17.wireOp",EDGE,"E106.0.0"),sQuery(id+"F17.wireOp",EDGE,"E106.0.1"),sQuery(id+"F17.wireOp",EDGE,"E106.0.2"),sQuery(id+"F17.wireOp",EDGE,"E106.0.3"),sQuery(id+"F17.wireOp",EDGE,"E106.0.4"),sQuery(id+"F17.wireOp",EDGE,"E106.0.5"),sQuery(id+"F17.wireOp",EDGE,"E106.0.6"),sQuery(id+"F17.wireOp",EDGE,"E106.0.7"),sQuery(id+"F17.wireOp",EDGE,"E106.0.8"),sQuery(id+"F17.wireOp",EDGE,"E106.0.9"),sQuery(id+"F17.wireOp",EDGE,"E106.0.10"),sQuery(id+"F17.wireOp",EDGE,"E106.0.11"),sQuery(id+"F17.wireOp",EDGE,"E106.0.12"),sQuery(id+"F17.wireOp",EDGE,"E106.0.13"),sQuery(id+"F17.wireOp",EDGE,"E106.0.14"),sQuery(id+"F17.wireOp",EDGE,"E106.0.15"),sQuery(id+"F17.wireOp",EDGE,"E107.0"),sQuery(id+"F17.wireOp",EDGE,"E107.1"),sQuery(id+"F17.wireOp",EDGE,"E107.2"),sQuery(id+"F17.wireOp",EDGE,"E107.3"),sQuery(id+"F17.wireOp",EDGE,"E107.4"),sQuery(id+"F17.wireOp",EDGE,"E107.5"),sQuery(id+"F17.wireOp",EDGE,"E107.6"),sQuery(id+"F17.wireOp",EDGE,"E107.7"),sQuery(id+"F17.wireOp",EDGE,"E107.8"),sQuery(id+"F17.wireOp",EDGE,"E107.9"),sQuery(id+"F17.wireOp",EDGE,"E107.10"),sQuery(id+"F17.wireOp",EDGE,"E107.11"),sQuery(id+"F17.wireOp",EDGE,"E107.12"),sQuery(id+"F17.wireOp",EDGE,"E107.13"),sQuery(id+"F17.wireOp",EDGE,"E107.14"),sQuery(id+"F17.wireOp",EDGE,"E107.15")])],"isStart":false})]})],"fromTools":[makeQuery(id+"F27.opExtrude","CAP_FACE",FACE,{"disambiguationData":[OSD([subQ40,subQ39,subQ38,subQ37,subQ36,subQ35,subQ34,subQ33,subQ32,subQ31,subQ30,subQ29,subQ28,subQ27,subQ26,subQ25,subQ24,subQ23,subQ22,subQ3,subQ21,subQ20,subQ19,subQ18,subQ17,subQ16,subQ15,subQ14,subQ13,subQ12,subQ11,subQ10,subQ9,subQ8,subQ7,subQ6]),TDD([makeQuery(id+"F18.boolean.opBoolean","SPLIT",FACE,{"disambiguationData":[TD([makeQuery(id+"F18.opExtrude","SWEPT_FACE",FACE,{"disambiguationData":[OSD([subQ51])]})])],"derivedFrom":subQ41})])],"isStart":false}),makeQuery(id+"F27.opExtrude","CAP_FACE",FACE,{"disambiguationData":[OSD([subQ40,subQ39,subQ38,subQ37,subQ36,subQ35,subQ34,subQ33,subQ32,subQ31,subQ30,subQ29,subQ28,subQ27,subQ26,subQ25,subQ24,subQ23,subQ22,subQ3,subQ21,subQ20,subQ19,subQ18,subQ17,subQ16,subQ15,subQ14,subQ13,subQ12,subQ11,subQ10,subQ9,subQ8,subQ7,subQ6]),TDD([makeQuery(id+"F18.boolean.opBoolean","SPLIT",FACE,{"disambiguationData":[TD([makeQuery(id+"F16.opExtrude","SWEPT_FACE",FACE,{"disambiguationData":[OSD([subQ24])]})])],"derivedFrom":subQ41})])],"isStart":false}),makeQuery(id+"F27.opExtrude","CAP_FACE",FACE,{"disambiguationData":[OSD([subQ40,subQ39,subQ38,subQ37,subQ36,subQ35,subQ34,subQ33,subQ32,subQ31,subQ30,subQ29,subQ28,subQ27,subQ26,subQ25,subQ24,subQ23,subQ22,subQ3,subQ21,subQ20,subQ19,subQ18,subQ17,subQ16,subQ15,subQ14,subQ13,subQ12,subQ11,subQ10,subQ9,subQ8,subQ7,subQ6]),TDD([makeQuery(id+"F18.boolean.opBoolean","SPLIT",FACE,{"disambiguationData":[TD([makeQuery(id+"F16.opExtrude","SWEPT_FACE",FACE,{"disambiguationData":[OSD([subQ22])]})])],"derivedFrom":subQ41})])],"isStart":false}),makeQuery(id+"F27.opExtrude","CAP_FACE",FACE,{"disambiguationData":[OSD([subQ40,subQ39,subQ38,subQ37,subQ36,subQ35,subQ34,subQ33,subQ32,subQ31,subQ30,subQ29,subQ28,subQ27,subQ26,subQ25,subQ24,subQ23,subQ22,subQ3,subQ21,subQ20,subQ19,subQ18,subQ17,subQ16,subQ15,subQ14,subQ13,subQ12,subQ11,subQ10,subQ9,subQ8,subQ7,subQ6]),TDD([makeQuery(id+"F18.boolean.opBoolean","SPLIT",FACE,{"disambiguationData":[TD([makeQuery(id+"F18.opExtrude","SWEPT_FACE",FACE,{"disambiguationData":[OSD([subQ45])]})])],"derivedFrom":subQ41})])],"isStart":false}),makeQuery(id+"F27.opExtrude","CAP_FACE",FACE,{"disambiguationData":[OSD([subQ40,subQ39,subQ38,subQ37,subQ36,subQ35,subQ34,subQ33,subQ32,subQ31,subQ30,subQ29,subQ28,subQ27,subQ26,subQ25,subQ24,subQ23,subQ22,subQ3,subQ21,subQ20,subQ19,subQ18,subQ17,subQ16,subQ15,subQ14,subQ13,subQ12,subQ11,subQ10,subQ9,subQ8,subQ7,subQ6]),TDD([makeQuery(id+"F18.boolean.opBoolean","SPLIT",FACE,{"disambiguationData":[TD([makeQuery(id+"F16.opExtrude","SWEPT_FACE",FACE,{"disambiguationData":[OSD([subQ23])]})])],"derivedFrom":subQ41})])],"isStart":false}),makeQuery(id+"F27.opExtrude","CAP_FACE",FACE,{"disambiguationData":[OSD([subQ40,subQ39,subQ38,subQ37,subQ36,subQ35,subQ34,subQ33,subQ32,subQ31,subQ30,subQ29,subQ28,subQ27,subQ26,subQ25,subQ24,subQ23,subQ22,subQ3,subQ21,subQ20,subQ19,subQ18,subQ17,subQ16,subQ15,subQ14,subQ13,subQ12,subQ11,subQ10,subQ9,subQ8,subQ7,subQ6]),TDD([makeQuery(id+"F18.boolean.opBoolean","SPLIT",FACE,{"disambiguationData":[TD([makeQuery(id+"F18.opExtrude","SWEPT_FACE",FACE,{"disambiguationData":[OSD([subQ2])]})])],"derivedFrom":subQ41})])],"isStart":false})]});}
            var sketch = newSketch(context, id + "F28", { "sketchPlane" : qUnion([Q0])});
            skCircle(sketch, "E155.0", {"center": v(0, 0) * mm, "radius": 20 * mm, "construction": true});
            skCircle(sketch, "E156.0", {"center": v(0, 0) * mm, "radius": 16 * mm, "construction": true});
            skCircle(sketch, "E157.0", {"center": v(0, 0) * mm, "radius": 10 * mm, "construction": true});
            skCircle(sketch, "E158.0", {"center": v(0, 0) * mm, "radius": 5 * mm, "construction": true});
            skCircle(sketch, "E159.0", {"center": v(0, 0) * mm, "radius": 19.7 * mm});
            skCircle(sketch, "E160.0", {"center": v(0, 0) * mm, "radius": 15.7 * mm});
            skCircle(sketch, "E161.0", {"center": v(0, 0) * mm, "radius": 9.7 * mm});
            skCircle(sketch, "E162.0", {"center": v(0, 0) * mm, "radius": 4.7 * mm});
            skSolve(sketch);
        }
        {
            var Q0;
            Q0=makeQuery(id+"F28.imprint","IMPRINT",FACE,{"disambiguationData":[TD([[makeQuery(id+"F28.imprint","IMPRINT",EDGE,{"derivedFrom":sQuery(id+"F28.wireOp",EDGE,"E159.0")}),1.0]])]});
            var Q1;
            Q1=makeQuery(id+"F28.imprint","IMPRINT",FACE,{"disambiguationData":[TD([[makeQuery(id+"F28.imprint","IMPRINT",EDGE,{"derivedFrom":sQuery(id+"F28.wireOp",EDGE,"E160.0")}),1.0]])]});
            var Q2;
            Q2=makeQuery(id+"F28.imprint","IMPRINT",FACE,{"disambiguationData":[TD([[makeQuery(id+"F28.imprint","IMPRINT",EDGE,{"derivedFrom":sQuery(id+"F28.wireOp",EDGE,"E161.0")}),1.0]])]});
            var Q3;
            Q3=makeQuery(id+"F28.imprint","IMPRINT",FACE,{"disambiguationData":[TD([[makeQuery(id+"F28.imprint","IMPRINT",EDGE,{"derivedFrom":sQuery(id+"F28.wireOp",EDGE,"E162.0")}),1.0]])]});
            var Q4;
            Q4=makeQuery(id+"F20.boolean.opBoolean","COPY",FACE,{"derivedFrom":makeQuery(id+"F20.opExtrude","CAP_FACE",FACE,{"disambiguationData":[OSD([sQuery(id+"F19.wireOp",EDGE,"E108.0.2"),sQuery(id+"F19.wireOp",EDGE,"E108.0.6"),sQuery(id+"F19.wireOp",EDGE,"E108.0.10"),sQuery(id+"F19.wireOp",EDGE,"E108.0.14"),sQuery(id+"F19.wireOp",EDGE,"E109.0"),sQuery(id+"F19.wireOp",EDGE,"E109.1"),sQuery(id+"F19.wireOp",EDGE,"E109.2"),sQuery(id+"F19.wireOp",EDGE,"E109.3"),sQuery(id+"F19.wireOp",EDGE,"E109.4"),sQuery(id+"F19.wireOp",EDGE,"E109.5"),sQuery(id+"F19.wireOp",EDGE,"E109.6"),sQuery(id+"F19.wireOp",EDGE,"E109.7"),sQuery(id+"F19.wireOp",EDGE,"E109.8"),sQuery(id+"F19.wireOp",EDGE,"E109.9"),sQuery(id+"F19.wireOp",EDGE,"E109.10"),sQuery(id+"F19.wireOp",EDGE,"E109.11")])],"isStart":false})});
            extrude(context, id + "F29", {"entities" : qUnion([Q0, Q1, Q2, Q3]), "operationType" : NewBodyOperationType.ADD, "endBound" : BoundingType.UP_TO_SURFACE, "depth" : 25 * mm, "endBoundEntityFace" : qUnion([Q4]), "hasOffset" : true, "offsetDistance" : (getVariable(context, 'x3')) * mm});
        }
        {
            var Q0;
            Q0=makeQuery(id+"F28.imprint","IMPRINT",FACE,{"disambiguationData":[TD([[makeQuery(id+"F28.imprint","IMPRINT",EDGE,{"derivedFrom":sQuery(id+"F28.wireOp",EDGE,"E160.0")}),1.0]])]});
            var Q1;
            Q1=makeQuery(id+"F28.imprint","IMPRINT",FACE,{"disambiguationData":[TD([[makeQuery(id+"F28.imprint","IMPRINT",EDGE,{"derivedFrom":sQuery(id+"F28.wireOp",EDGE,"E162.0")}),1.0]])]});
            var Q2;
            Q2=makeQuery(id+"F28.imprint","IMPRINT",FACE,{"disambiguationData":[TD([[makeQuery(id+"F28.imprint","IMPRINT",EDGE,{"derivedFrom":sQuery(id+"F28.wireOp",EDGE,"E161.0")}),1.0]])]});
            var Q3;
            Q3=makeQuery(id+"F22.boolean.opBoolean","COPY",FACE,{"derivedFrom":makeQuery(id+"F22.opExtrude","CAP_FACE",FACE,{"disambiguationData":[OSD([sQuery(id+"F21.wireOp",EDGE,"E110.0"),sQuery(id+"F21.wireOp",EDGE,"E111.0"),sQuery(id+"F21.wireOp",EDGE,"E112.0"),sQuery(id+"F21.wireOp",EDGE,"E113.0"),sQuery(id+"F21.wireOp",EDGE,"E114.0"),sQuery(id+"F21.wireOp",EDGE,"E115.0"),sQuery(id+"F21.wireOp",EDGE,"E116.0"),sQuery(id+"F21.wireOp",EDGE,"E117.0"),sQuery(id+"F21.wireOp",EDGE,"E117.1"),sQuery(id+"F21.wireOp",EDGE,"E117.2"),sQuery(id+"F21.wireOp",EDGE,"E117.3"),sQuery(id+"F21.wireOp",EDGE,"E117.4"),sQuery(id+"F21.wireOp",EDGE,"E117.5"),sQuery(id+"F21.wireOp",EDGE,"E117.6"),sQuery(id+"F21.wireOp",EDGE,"E117.7"),sQuery(id+"F21.wireOp",EDGE,"E117.8")])],"isStart":false})});
            extrude(context, id + "F30", {"entities" : qUnion([Q0, Q1, Q2]), "operationType" : NewBodyOperationType.ADD, "endBound" : BoundingType.UP_TO_SURFACE, "depth" : 25 * mm, "endBoundEntityFace" : qUnion([Q3]), "hasOffset" : true, "offsetDistance" : (getVariable(context, 'x3')) * 2 * mm});
        }
        {
            var Q0;
            Q0=makeQuery(id+"F30.opExtrude","CAP_FACE",FACE,{"disambiguationData":[OSD([sQuery(id+"F28.wireOp",EDGE,"E160.0")])],"isStart":false});
            extrude(context, id + "F31", {"entities" : qUnion([Q0]), "operationType" : NewBodyOperationType.REMOVE, "oppositeDirection" : true, "depth" : (getVariable(context, 'x2')) * mm, "offsetDistance" : 25 * mm});
        }
        {
            var Q0;
            Q0=makeQuery(id+"F28.imprint","IMPRINT",FACE,{"disambiguationData":[TD([[makeQuery(id+"F28.imprint","IMPRINT",EDGE,{"derivedFrom":sQuery(id+"F28.wireOp",EDGE,"E161.0")}),1.0]])]});
            var Q1;
            Q1=makeQuery(id+"F28.imprint","IMPRINT",FACE,{"disambiguationData":[TD([[makeQuery(id+"F28.imprint","IMPRINT",EDGE,{"derivedFrom":sQuery(id+"F28.wireOp",EDGE,"E162.0")}),1.0]])]});
            var Q2;
            Q2=makeQuery(id+"F26.boolean.opBoolean","COPY",FACE,{"derivedFrom":makeQuery(id+"F26.opExtrude","CAP_FACE",FACE,{"disambiguationData":[OSD([sQuery(id+"F9.wireOp",EDGE,"E61"),sQuery(id+"F9.wireOp",EDGE,"E62.sketch_text.stroke-0"),sQuery(id+"F9.wireOp",EDGE,"E62.sketch_text.stroke-1"),sQuery(id+"F9.wireOp",EDGE,"E62.sketch_text.stroke-2"),sQuery(id+"F9.wireOp",EDGE,"E62.sketch_text.stroke-3"),sQuery(id+"F9.wireOp",EDGE,"E62.sketch_text.stroke-4"),sQuery(id+"F9.wireOp",EDGE,"E62.sketch_text.stroke-5"),sQuery(id+"F9.wireOp",EDGE,"E62.sketch_text.stroke-6"),sQuery(id+"F9.wireOp",EDGE,"E62.sketch_text.stroke-7"),sQuery(id+"F9.wireOp",EDGE,"E62.sketch_text.stroke-8"),sQuery(id+"F9.wireOp",EDGE,"E62.sketch_text.stroke-9"),sQuery(id+"F9.wireOp",EDGE,"E62.sketch_text.stroke-10"),sQuery(id+"F9.wireOp",EDGE,"E62.sketch_text.stroke-11"),sQuery(id+"F9.wireOp",EDGE,"E62.sketch_text.stroke-12"),sQuery(id+"F9.wireOp",EDGE,"E62.sketch_text.stroke-13"),sQuery(id+"F9.wireOp",EDGE,"E62.sketch_text.stroke-17"),sQuery(id+"F9.wireOp",EDGE,"E66.sketch_text.stroke-0"),sQuery(id+"F9.wireOp",EDGE,"E66.sketch_text.stroke-1"),sQuery(id+"F9.wireOp",EDGE,"E66.sketch_text.stroke-2"),sQuery(id+"F9.wireOp",EDGE,"E66.sketch_text.stroke-3"),sQuery(id+"F9.wireOp",EDGE,"E66.sketch_text.stroke-4"),sQuery(id+"F9.wireOp",EDGE,"E66.sketch_text.stroke-5"),sQuery(id+"F9.wireOp",EDGE,"E66.sketch_text.stroke-6"),sQuery(id+"F9.wireOp",EDGE,"E66.sketch_text.stroke-7"),sQuery(id+"F9.wireOp",EDGE,"E66.sketch_text.stroke-8"),sQuery(id+"F9.wireOp",EDGE,"E66.sketch_text.stroke-9"),sQuery(id+"F9.wireOp",EDGE,"E66.sketch_text.stroke-10"),sQuery(id+"F9.wireOp",EDGE,"E66.sketch_text.stroke-11"),sQuery(id+"F9.wireOp",EDGE,"E66.sketch_text.stroke-12"),sQuery(id+"F9.wireOp",EDGE,"E66.sketch_text.stroke-13"),sQuery(id+"F9.wireOp",EDGE,"E66.sketch_text.stroke-14"),sQuery(id+"F9.wireOp",EDGE,"E66.sketch_text.stroke-15"),sQuery(id+"F9.wireOp",EDGE,"E66.sketch_text.stroke-16"),sQuery(id+"F9.wireOp",EDGE,"E66.sketch_text.stroke-17"),sQuery(id+"F9.wireOp",EDGE,"E66.sketch_text.stroke-18"),sQuery(id+"F9.wireOp",EDGE,"E66.sketch_text.stroke-19"),sQuery(id+"F9.wireOp",EDGE,"E66.sketch_text.stroke-20"),sQuery(id+"F9.wireOp",EDGE,"E66.sketch_text.stroke-21"),sQuery(id+"F9.wireOp",EDGE,"E66.sketch_text.stroke-22"),sQuery(id+"F9.wireOp",EDGE,"E66.sketch_text.stroke-23"),sQuery(id+"F9.wireOp",EDGE,"E66.sketch_text.stroke-24"),sQuery(id+"F9.wireOp",EDGE,"E66.sketch_text.stroke-25"),sQuery(id+"F9.wireOp",EDGE,"E66.sketch_text.stroke-26"),sQuery(id+"F9.wireOp",EDGE,"E66.sketch_text.stroke-27"),sQuery(id+"F9.wireOp",EDGE,"E66.sketch_text.stroke-28"),sQuery(id+"F9.wireOp",EDGE,"E66.sketch_text.stroke-29"),sQuery(id+"F9.wireOp",EDGE,"E66.sketch_text.stroke-30"),sQuery(id+"F9.wireOp",EDGE,"E66.sketch_text.stroke-31"),sQuery(id+"F9.wireOp",EDGE,"E66.sketch_text.stroke-32"),sQuery(id+"F9.wireOp",EDGE,"E66.sketch_text.stroke-33"),sQuery(id+"F9.wireOp",EDGE,"E67.sketch_text.stroke-0"),sQuery(id+"F9.wireOp",EDGE,"E67.sketch_text.stroke-1"),sQuery(id+"F9.wireOp",EDGE,"E67.sketch_text.stroke-2"),sQuery(id+"F9.wireOp",EDGE,"E67.sketch_text.stroke-3"),sQuery(id+"F9.wireOp",EDGE,"E67.sketch_text.stroke-4"),sQuery(id+"F9.wireOp",EDGE,"E67.sketch_text.stroke-5"),sQuery(id+"F9.wireOp",EDGE,"E67.sketch_text.stroke-6"),sQuery(id+"F9.wireOp",EDGE,"E67.sketch_text.stroke-7"),sQuery(id+"F9.wireOp",EDGE,"E67.sketch_text.stroke-9"),sQuery(id+"F9.wireOp",EDGE,"E67.sketch_text.stroke-10"),sQuery(id+"F9.wireOp",EDGE,"E67.sketch_text.stroke-11"),sQuery(id+"F9.wireOp",EDGE,"E67.sketch_text.stroke-12"),sQuery(id+"F9.wireOp",EDGE,"E67.sketch_text.stroke-13"),sQuery(id+"F9.wireOp",EDGE,"E67.sketch_text.stroke-14"),sQuery(id+"F9.wireOp",EDGE,"E67.sketch_text.stroke-15"),sQuery(id+"F9.wireOp",EDGE,"E67.sketch_text.stroke-16"),sQuery(id+"F9.wireOp",EDGE,"E67.sketch_text.stroke-17"),sQuery(id+"F9.wireOp",EDGE,"E67.sketch_text.stroke-19"),sQuery(id+"F9.wireOp",EDGE,"E68.sketch_text.stroke-0"),sQuery(id+"F9.wireOp",EDGE,"E68.sketch_text.stroke-1"),sQuery(id+"F9.wireOp",EDGE,"E68.sketch_text.stroke-2"),sQuery(id+"F9.wireOp",EDGE,"E68.sketch_text.stroke-3"),sQuery(id+"F9.wireOp",EDGE,"E68.sketch_text.stroke-4"),sQuery(id+"F9.wireOp",EDGE,"E68.sketch_text.stroke-5"),sQuery(id+"F9.wireOp",EDGE,"E68.sketch_text.stroke-6"),sQuery(id+"F9.wireOp",EDGE,"E68.sketch_text.stroke-7"),sQuery(id+"F9.wireOp",EDGE,"E68.sketch_text.stroke-9"),sQuery(id+"F9.wireOp",EDGE,"E68.sketch_text.stroke-10"),sQuery(id+"F9.wireOp",EDGE,"E68.sketch_text.stroke-11"),sQuery(id+"F9.wireOp",EDGE,"E68.sketch_text.stroke-12"),sQuery(id+"F9.wireOp",EDGE,"E68.sketch_text.stroke-13"),sQuery(id+"F9.wireOp",EDGE,"E68.sketch_text.stroke-14"),sQuery(id+"F9.wireOp",EDGE,"E68.sketch_text.stroke-17"),sQuery(id+"F25.wireOp",EDGE,"E137.0"),sQuery(id+"F25.wireOp",EDGE,"E139.0"),sQuery(id+"F25.wireOp",EDGE,"E140.0"),sQuery(id+"F25.wireOp",EDGE,"E146.0"),sQuery(id+"F25.wireOp",EDGE,"E151.0"),sQuery(id+"F25.wireOp",EDGE,"E151.1"),sQuery(id+"F25.wireOp",EDGE,"E151.2"),sQuery(id+"F25.wireOp",EDGE,"E151.3"),sQuery(id+"F25.wireOp",EDGE,"E151.4"),sQuery(id+"F25.wireOp",EDGE,"E151.5"),sQuery(id+"F25.wireOp",EDGE,"E151.6"),sQuery(id+"F25.wireOp",EDGE,"E151.7"),sQuery(id+"F25.wireOp",EDGE,"E151.8"),sQuery(id+"F25.wireOp",EDGE,"E151.9"),sQuery(id+"F25.wireOp",EDGE,"E151.10"),sQuery(id+"F25.wireOp",EDGE,"E151.11"),sQuery(id+"F25.wireOp",EDGE,"E151.12"),sQuery(id+"F25.wireOp",EDGE,"E151.13"),sQuery(id+"F25.wireOp",EDGE,"E152.filletArc"),sQuery(id+"F25.wireOp",EDGE,"E154")])],"isStart":false})});
            extrude(context, id + "F32", {"entities" : qUnion([Q0, Q1]), "operationType" : NewBodyOperationType.ADD, "endBound" : BoundingType.UP_TO_SURFACE, "depth" : 25 * mm, "endBoundEntityFace" : qUnion([Q2]), "hasOffset" : true, "offsetDistance" : (getVariable(context, 'x3')) * 3 * mm});
        }
        {
            var Q0;
            Q0=makeQuery(id+"F32.opExtrude","CAP_FACE",FACE,{"disambiguationData":[OSD([sQuery(id+"F28.wireOp",EDGE,"E161.0")])],"isStart":false});
            extrude(context, id + "F33", {"entities" : qUnion([Q0]), "operationType" : NewBodyOperationType.REMOVE, "oppositeDirection" : true, "depth" : (getVariable(context, 'x2') * 2) * mm, "offsetDistance" : 25 * mm});
        }
        {
            var Q0;
            Q0=makeQuery(id+"F28.imprint","IMPRINT",FACE,{"disambiguationData":[TD([[makeQuery(id+"F28.imprint","IMPRINT",EDGE,{"derivedFrom":sQuery(id+"F28.wireOp",EDGE,"E162.0")}),1.0]])]});
            var Q1;
            Q1=makeQuery(id+"F13.opExtrude","CAP_FACE",FACE,{"disambiguationData":[OSD([sQuery(id+"F12.wireOp",EDGE,"E69"),sQuery(id+"F12.wireOp",EDGE,"E70"),sQuery(id+"F12.wireOp",EDGE,"E71"),sQuery(id+"F12.wireOp",EDGE,"E72"),sQuery(id+"F12.wireOp",EDGE,"E73"),sQuery(id+"F12.wireOp",EDGE,"E74"),sQuery(id+"F12.wireOp",EDGE,"E75"),sQuery(id+"F12.wireOp",EDGE,"E76"),sQuery(id+"F12.wireOp",EDGE,"E77"),sQuery(id+"F12.wireOp",EDGE,"E78"),sQuery(id+"F12.wireOp",EDGE,"E79"),sQuery(id+"F12.wireOp",EDGE,"E80"),sQuery(id+"F12.wireOp",EDGE,"E81.filletArc"),sQuery(id+"F12.wireOp",EDGE,"E82.filletArc"),sQuery(id+"F12.wireOp",EDGE,"E83.filletArc"),sQuery(id+"F12.wireOp",EDGE,"E84.filletArc"),sQuery(id+"F12.wireOp",EDGE,"E85"),sQuery(id+"F12.wireOp",EDGE,"E86.sketch_text.stroke-0"),sQuery(id+"F12.wireOp",EDGE,"E86.sketch_text.stroke-1"),sQuery(id+"F12.wireOp",EDGE,"E86.sketch_text.stroke-2"),sQuery(id+"F12.wireOp",EDGE,"E86.sketch_text.stroke-3"),sQuery(id+"F12.wireOp",EDGE,"E86.sketch_text.stroke-4"),sQuery(id+"F12.wireOp",EDGE,"E86.sketch_text.stroke-5"),sQuery(id+"F12.wireOp",EDGE,"E86.sketch_text.stroke-6"),sQuery(id+"F12.wireOp",EDGE,"E86.sketch_text.stroke-7"),sQuery(id+"F12.wireOp",EDGE,"E86.sketch_text.stroke-8"),sQuery(id+"F12.wireOp",EDGE,"E86.sketch_text.stroke-9"),sQuery(id+"F12.wireOp",EDGE,"E86.sketch_text.stroke-10"),sQuery(id+"F12.wireOp",EDGE,"E86.sketch_text.stroke-11"),sQuery(id+"F12.wireOp",EDGE,"E86.sketch_text.stroke-12"),sQuery(id+"F12.wireOp",EDGE,"E86.sketch_text.stroke-13"),sQuery(id+"F12.wireOp",EDGE,"E86.sketch_text.stroke-14"),sQuery(id+"F12.wireOp",EDGE,"E86.sketch_text.stroke-15"),sQuery(id+"F12.wireOp",EDGE,"E86.sketch_text.stroke-16"),sQuery(id+"F12.wireOp",EDGE,"E86.sketch_text.stroke-17"),sQuery(id+"F12.wireOp",EDGE,"E86.sketch_text.stroke-18"),sQuery(id+"F12.wireOp",EDGE,"E86.sketch_text.stroke-19"),sQuery(id+"F12.wireOp",EDGE,"E90.sketch_text.stroke-0"),sQuery(id+"F12.wireOp",EDGE,"E90.sketch_text.stroke-1"),sQuery(id+"F12.wireOp",EDGE,"E90.sketch_text.stroke-2"),sQuery(id+"F12.wireOp",EDGE,"E90.sketch_text.stroke-3"),sQuery(id+"F12.wireOp",EDGE,"E90.sketch_text.stroke-4"),sQuery(id+"F12.wireOp",EDGE,"E90.sketch_text.stroke-5"),sQuery(id+"F12.wireOp",EDGE,"E90.sketch_text.stroke-6"),sQuery(id+"F12.wireOp",EDGE,"E90.sketch_text.stroke-7"),sQuery(id+"F12.wireOp",EDGE,"E90.sketch_text.stroke-8"),sQuery(id+"F12.wireOp",EDGE,"E90.sketch_text.stroke-9"),sQuery(id+"F12.wireOp",EDGE,"E90.sketch_text.stroke-10"),sQuery(id+"F12.wireOp",EDGE,"E90.sketch_text.stroke-11"),sQuery(id+"F12.wireOp",EDGE,"E90.sketch_text.stroke-12"),sQuery(id+"F12.wireOp",EDGE,"E90.sketch_text.stroke-13"),sQuery(id+"F12.wireOp",EDGE,"E90.sketch_text.stroke-14"),sQuery(id+"F12.wireOp",EDGE,"E90.sketch_text.stroke-15"),sQuery(id+"F12.wireOp",EDGE,"E91.sketch_text.stroke-0"),sQuery(id+"F12.wireOp",EDGE,"E91.sketch_text.stroke-1"),sQuery(id+"F12.wireOp",EDGE,"E91.sketch_text.stroke-2"),sQuery(id+"F12.wireOp",EDGE,"E91.sketch_text.stroke-3"),sQuery(id+"F12.wireOp",EDGE,"E91.sketch_text.stroke-4"),sQuery(id+"F12.wireOp",EDGE,"E91.sketch_text.stroke-5"),sQuery(id+"F12.wireOp",EDGE,"E91.sketch_text.stroke-6"),sQuery(id+"F12.wireOp",EDGE,"E92.sketch_text.stroke-0"),sQuery(id+"F12.wireOp",EDGE,"E92.sketch_text.stroke-1"),sQuery(id+"F12.wireOp",EDGE,"E92.sketch_text.stroke-2"),sQuery(id+"F12.wireOp",EDGE,"E92.sketch_text.stroke-3"),sQuery(id+"F12.wireOp",EDGE,"E92.sketch_text.stroke-4"),sQuery(id+"F12.wireOp",EDGE,"E92.sketch_text.stroke-5"),sQuery(id+"F12.wireOp",EDGE,"E92.sketch_text.stroke-6"),sQuery(id+"F12.wireOp",EDGE,"E92.sketch_text.stroke-7"),sQuery(id+"F12.wireOp",EDGE,"E92.sketch_text.stroke-8"),sQuery(id+"F12.wireOp",EDGE,"E92.sketch_text.stroke-9"),sQuery(id+"F12.wireOp",EDGE,"E92.sketch_text.stroke-10"),sQuery(id+"F12.wireOp",EDGE,"E92.sketch_text.stroke-11"),sQuery(id+"F12.wireOp",EDGE,"E92.sketch_text.stroke-12"),sQuery(id+"F12.wireOp",EDGE,"E92.sketch_text.stroke-13"),sQuery(id+"F12.wireOp",EDGE,"E92.sketch_text.stroke-14"),sQuery(id+"F12.wireOp",EDGE,"E92.sketch_text.stroke-15"),sQuery(id+"F12.wireOp",EDGE,"E92.sketch_text.stroke-16")])],"isStart":false});
            extrude(context, id + "F34", {"entities" : qUnion([Q0]), "operationType" : NewBodyOperationType.ADD, "depth" : 22.5 * mm, "endBoundEntityFace" : qUnion([Q1]), "offsetDistance" : (getVariable(context, 'x3') * 5 - getVariable(context, 'x2') * 5) * mm});
        }
        {
            var Q0;
            Q0=makeQuery(id+"F16.opExtrude","CAP_EDGE",EDGE,{"disambiguationData":[OSD([sQuery(id+"F15.wireOp",EDGE,"E94.5")])],"isStart":true});
            chamfer(context, id + "F35", {"entities" : qUnion([Q0]), "width" : 2.5 * mm, "tangentPropagation" : true});
        }
        {
            var Q0;
            Q0=makeQuery(id+"F29.opExtrude","CAP_EDGE",EDGE,{"disambiguationData":[OSD([sQuery(id+"F28.wireOp",EDGE,"E159.0")])],"isStart":false});
            var Q1;
            Q1=makeQuery(id+"F31.boolean.opBoolean","COPY",EDGE,{"derivedFrom":makeQuery(id+"F31.opExtrude","CAP_EDGE",EDGE,{"disambiguationData":[OSD([sQuery(id+"F28.wireOp",EDGE,"E160.0")])],"isStart":false})});
            var Q2;
            Q2=makeQuery(id+"F33.boolean.opBoolean","COPY",EDGE,{"derivedFrom":makeQuery(id+"F33.opExtrude","CAP_EDGE",EDGE,{"disambiguationData":[OSD([sQuery(id+"F28.wireOp",EDGE,"E161.0")])],"isStart":false})});
            var Q3;
            Q3=makeQuery(id+"F34.opExtrude","CAP_EDGE",EDGE,{"disambiguationData":[OSD([sQuery(id+"F28.wireOp",EDGE,"E162.0")])],"isStart":false});
            var Q4;
            Q4=makeQuery(id+"F18.boolean.opBoolean","INTERSECT",EDGE,{"derivedFrom":[makeQuery(id+"F16.opExtrude","CAP_FACE",FACE,{"disambiguationData":[OSD([sQuery(id+"F15.wireOp",EDGE,"E94.0"),sQuery(id+"F15.wireOp",EDGE,"E94.1"),sQuery(id+"F15.wireOp",EDGE,"E94.2"),sQuery(id+"F15.wireOp",EDGE,"E94.3"),sQuery(id+"F15.wireOp",EDGE,"E94.4"),sQuery(id+"F15.wireOp",EDGE,"E94.5"),sQuery(id+"F15.wireOp",EDGE,"E94.6"),sQuery(id+"F15.wireOp",EDGE,"E94.7"),sQuery(id+"F15.wireOp",EDGE,"E94.8"),sQuery(id+"F15.wireOp",EDGE,"E94.9"),sQuery(id+"F15.wireOp",EDGE,"E94.10"),sQuery(id+"F15.wireOp",EDGE,"E94.11"),sQuery(id+"F15.wireOp",EDGE,"E94.12"),sQuery(id+"F15.wireOp",EDGE,"E94.13"),sQuery(id+"F15.wireOp",EDGE,"E94.14"),sQuery(id+"F15.wireOp",EDGE,"E94.15"),sQuery(id+"F15.wireOp",EDGE,"E95.0"),sQuery(id+"F15.wireOp",EDGE,"E96.trimOffspring"),sQuery(id+"F15.wireOp",EDGE,"E98.trimOffspring"),sQuery(id+"F15.wireOp",EDGE,"E100.trimOffspring"),sQuery(id+"F15.wireOp",EDGE,"E102.0"),sQuery(id+"F15.wireOp",EDGE,"E102.1"),sQuery(id+"F15.wireOp",EDGE,"E102.2"),sQuery(id+"F15.wireOp",EDGE,"E102.3"),sQuery(id+"F15.wireOp",EDGE,"E102.4"),sQuery(id+"F15.wireOp",EDGE,"E103.0"),sQuery(id+"F15.wireOp",EDGE,"E103.2"),sQuery(id+"F15.wireOp",EDGE,"E103.3"),sQuery(id+"F15.wireOp",EDGE,"E103.4"),sQuery(id+"F15.wireOp",EDGE,"E104.0"),sQuery(id+"F15.wireOp",EDGE,"E104.1"),sQuery(id+"F15.wireOp",EDGE,"E104.2"),sQuery(id+"F15.wireOp",EDGE,"E105.0"),sQuery(id+"F15.wireOp",EDGE,"E105.1"),sQuery(id+"F15.wireOp",EDGE,"E105.2"),sQuery(id+"F15.wireOp",EDGE,"E105.3")])],"isStart":true}),makeQuery(id+"F18.opExtrude","SWEPT_FACE",FACE,{"disambiguationData":[OSD([sQuery(id+"F17.wireOp",EDGE,"E107.6")])]})]});
            var Q5;
            Q5=makeQuery(id+"F4.opExtrude","SWEPT_FACE",FACE,{"disambiguationData":[OSD([sQuery(id+"F3.wireOp",EDGE,"E16")])]});
            var Q6;
            Q6=makeQuery(id+"F4.opExtrude","CAP_EDGE",EDGE,{"disambiguationData":[OSD([sQuery(id+"F3.wireOp",EDGE,"E2")])],"isStart":true});
            var Q7;
            Q7=makeQuery(id+"F7.opExtrude","SWEPT_FACE",FACE,{"disambiguationData":[OSD([sQuery(id+"F6.wireOp",EDGE,"E37")])]});
            var Q8;
            Q8=makeQuery(id+"F7.opExtrude","CAP_EDGE",EDGE,{"disambiguationData":[OSD([sQuery(id+"F6.wireOp",EDGE,"E36.filletArc")])],"isStart":true});
            var Q9;
            Q9=makeQuery(id+"F10.opExtrude","SWEPT_FACE",FACE,{"disambiguationData":[OSD([sQuery(id+"F9.wireOp",EDGE,"E61")])]});
            var Q10;
            Q10=makeQuery(id+"F10.opExtrude","CAP_EDGE",EDGE,{"disambiguationData":[OSD([sQuery(id+"F9.wireOp",EDGE,"E50")])],"isStart":true});
            var Q11;
            Q11=makeQuery(id+"F4.opExtrude","CAP_EDGE",EDGE,{"disambiguationData":[OSD([sQuery(id+"F3.wireOp",EDGE,"E4")])],"isStart":false});
            var Q12;
            Q12=makeQuery(id+"F7.opExtrude","CAP_EDGE",EDGE,{"disambiguationData":[OSD([sQuery(id+"F6.wireOp",EDGE,"E25")])],"isStart":false});
            var Q13;
            Q13=makeQuery(id+"F10.opExtrude","CAP_EDGE",EDGE,{"disambiguationData":[OSD([sQuery(id+"F9.wireOp",EDGE,"E50")])],"isStart":false});
            var Q14;
            Q14=makeQuery(id+"F13.opExtrude","SWEPT_FACE",FACE,{"disambiguationData":[OSD([sQuery(id+"F12.wireOp",EDGE,"E85")])]});
            var Q15;
            Q15=makeQuery(id+"F13.opExtrude","CAP_EDGE",EDGE,{"disambiguationData":[OSD([sQuery(id+"F12.wireOp",EDGE,"E73")])],"isStart":false});
            var Q16;
            Q16=makeQuery(id+"F13.opExtrude","CAP_EDGE",EDGE,{"disambiguationData":[OSD([sQuery(id+"F12.wireOp",EDGE,"E78")])],"isStart":true});
            var Q17;
            {var subQ0=sQuery(id+"F15.wireOp",EDGE,"E98.trimOffspring");var subQ1=makeQuery(id+"F18.opExtrude","CAP_FACE",FACE,{"disambiguationData":[OSD([sQuery(id+"F3.wireOp",EDGE,"E0"),sQuery(id+"F3.wireOp",EDGE,"E1"),sQuery(id+"F3.wireOp",EDGE,"E2"),sQuery(id+"F3.wireOp",EDGE,"E3"),sQuery(id+"F3.wireOp",EDGE,"E4"),sQuery(id+"F3.wireOp",EDGE,"E5"),sQuery(id+"F3.wireOp",EDGE,"E6"),sQuery(id+"F3.wireOp",EDGE,"E7"),sQuery(id+"F3.wireOp",EDGE,"E8"),sQuery(id+"F3.wireOp",EDGE,"E9"),sQuery(id+"F3.wireOp",EDGE,"E10"),sQuery(id+"F3.wireOp",EDGE,"E11"),sQuery(id+"F3.wireOp",EDGE,"E12.filletArc"),sQuery(id+"F3.wireOp",EDGE,"E13.filletArc"),sQuery(id+"F3.wireOp",EDGE,"E14.filletArc"),sQuery(id+"F3.wireOp",EDGE,"E15.filletArc"),sQuery(id+"F3.wireOp",EDGE,"E16"),sQuery(id+"F3.wireOp",EDGE,"E17.sketch_text.stroke-0"),sQuery(id+"F3.wireOp",EDGE,"E17.sketch_text.stroke-1"),sQuery(id+"F3.wireOp",EDGE,"E17.sketch_text.stroke-2"),sQuery(id+"F3.wireOp",EDGE,"E17.sketch_text.stroke-3"),sQuery(id+"F3.wireOp",EDGE,"E17.sketch_text.stroke-4"),sQuery(id+"F3.wireOp",EDGE,"E17.sketch_text.stroke-5"),sQuery(id+"F3.wireOp",EDGE,"E17.sketch_text.stroke-6"),sQuery(id+"F3.wireOp",EDGE,"E17.sketch_text.stroke-7"),sQuery(id+"F3.wireOp",EDGE,"E17.sketch_text.stroke-8"),sQuery(id+"F3.wireOp",EDGE,"E17.sketch_text.stroke-9"),sQuery(id+"F3.wireOp",EDGE,"E17.sketch_text.stroke-10"),sQuery(id+"F3.wireOp",EDGE,"E17.sketch_text.stroke-11"),sQuery(id+"F3.wireOp",EDGE,"E17.sketch_text.stroke-12"),sQuery(id+"F3.wireOp",EDGE,"E17.sketch_text.stroke-13"),sQuery(id+"F3.wireOp",EDGE,"E17.sketch_text.stroke-14"),sQuery(id+"F3.wireOp",EDGE,"E17.sketch_text.stroke-15"),sQuery(id+"F3.wireOp",EDGE,"E17.sketch_text.stroke-16"),sQuery(id+"F3.wireOp",EDGE,"E17.sketch_text.stroke-17"),sQuery(id+"F3.wireOp",EDGE,"E17.sketch_text.stroke-18"),sQuery(id+"F3.wireOp",EDGE,"E17.sketch_text.stroke-19"),sQuery(id+"F3.wireOp",EDGE,"E17.sketch_text.stroke-20"),sQuery(id+"F3.wireOp",EDGE,"E17.sketch_text.stroke-21"),sQuery(id+"F3.wireOp",EDGE,"E17.sketch_text.stroke-22"),sQuery(id+"F3.wireOp",EDGE,"E17.sketch_text.stroke-23"),sQuery(id+"F3.wireOp",EDGE,"E17.sketch_text.stroke-24"),sQuery(id+"F3.wireOp",EDGE,"E17.sketch_text.stroke-25"),sQuery(id+"F3.wireOp",EDGE,"E17.sketch_text.stroke-26"),sQuery(id+"F3.wireOp",EDGE,"E17.sketch_text.stroke-27"),sQuery(id+"F3.wireOp",EDGE,"E17.sketch_text.stroke-28"),sQuery(id+"F3.wireOp",EDGE,"E17.sketch_text.stroke-29"),sQuery(id+"F3.wireOp",EDGE,"E17.sketch_text.stroke-30"),sQuery(id+"F3.wireOp",EDGE,"E17.sketch_text.stroke-31"),sQuery(id+"F3.wireOp",EDGE,"E18.sketch_text.stroke-0"),sQuery(id+"F3.wireOp",EDGE,"E18.sketch_text.stroke-1"),sQuery(id+"F3.wireOp",EDGE,"E18.sketch_text.stroke-2"),sQuery(id+"F3.wireOp",EDGE,"E18.sketch_text.stroke-3"),sQuery(id+"F3.wireOp",EDGE,"E18.sketch_text.stroke-4"),sQuery(id+"F3.wireOp",EDGE,"E18.sketch_text.stroke-5"),sQuery(id+"F3.wireOp",EDGE,"E18.sketch_text.stroke-6"),sQuery(id+"F3.wireOp",EDGE,"E18.sketch_text.stroke-7"),sQuery(id+"F3.wireOp",EDGE,"E18.sketch_text.stroke-8"),sQuery(id+"F3.wireOp",EDGE,"E18.sketch_text.stroke-9"),sQuery(id+"F3.wireOp",EDGE,"E18.sketch_text.stroke-10"),sQuery(id+"F3.wireOp",EDGE,"E18.sketch_text.stroke-11"),sQuery(id+"F3.wireOp",EDGE,"E18.sketch_text.stroke-12"),sQuery(id+"F3.wireOp",EDGE,"E18.sketch_text.stroke-13"),sQuery(id+"F3.wireOp",EDGE,"E18.sketch_text.stroke-14"),sQuery(id+"F3.wireOp",EDGE,"E18.sketch_text.stroke-15"),sQuery(id+"F3.wireOp",EDGE,"E18.sketch_text.stroke-16"),sQuery(id+"F3.wireOp",EDGE,"E18.sketch_text.stroke-17"),sQuery(id+"F3.wireOp",EDGE,"E18.sketch_text.stroke-18"),sQuery(id+"F3.wireOp",EDGE,"E18.sketch_text.stroke-19"),sQuery(id+"F3.wireOp",EDGE,"E18.sketch_text.stroke-20"),sQuery(id+"F3.wireOp",EDGE,"E18.sketch_text.stroke-21"),sQuery(id+"F3.wireOp",EDGE,"E18.sketch_text.stroke-22"),sQuery(id+"F3.wireOp",EDGE,"E18.sketch_text.stroke-23"),sQuery(id+"F3.wireOp",EDGE,"E18.sketch_text.stroke-24"),sQuery(id+"F3.wireOp",EDGE,"E18.sketch_text.stroke-25"),sQuery(id+"F3.wireOp",EDGE,"E18.sketch_text.stroke-26"),sQuery(id+"F3.wireOp",EDGE,"E18.sketch_text.stroke-27"),sQuery(id+"F3.wireOp",EDGE,"E19.sketch_text.stroke-0"),sQuery(id+"F3.wireOp",EDGE,"E19.sketch_text.stroke-1"),sQuery(id+"F3.wireOp",EDGE,"E19.sketch_text.stroke-2"),sQuery(id+"F3.wireOp",EDGE,"E19.sketch_text.stroke-3"),sQuery(id+"F3.wireOp",EDGE,"E19.sketch_text.stroke-4"),sQuery(id+"F3.wireOp",EDGE,"E19.sketch_text.stroke-5"),sQuery(id+"F3.wireOp",EDGE,"E19.sketch_text.stroke-6"),sQuery(id+"F3.wireOp",EDGE,"E19.sketch_text.stroke-7"),sQuery(id+"F3.wireOp",EDGE,"E19.sketch_text.stroke-8"),sQuery(id+"F3.wireOp",EDGE,"E19.sketch_text.stroke-9"),sQuery(id+"F3.wireOp",EDGE,"E19.sketch_text.stroke-10"),sQuery(id+"F3.wireOp",EDGE,"E19.sketch_text.stroke-11"),sQuery(id+"F3.wireOp",EDGE,"E19.sketch_text.stroke-12"),sQuery(id+"F3.wireOp",EDGE,"E19.sketch_text.stroke-13"),sQuery(id+"F3.wireOp",EDGE,"E19.sketch_text.stroke-14"),sQuery(id+"F3.wireOp",EDGE,"E19.sketch_text.stroke-15"),sQuery(id+"F3.wireOp",EDGE,"E19.sketch_text.stroke-16"),sQuery(id+"F3.wireOp",EDGE,"E19.sketch_text.stroke-17"),sQuery(id+"F3.wireOp",EDGE,"E19.sketch_text.stroke-18"),sQuery(id+"F3.wireOp",EDGE,"E19.sketch_text.stroke-19"),sQuery(id+"F3.wireOp",EDGE,"E19.sketch_text.stroke-20"),sQuery(id+"F3.wireOp",EDGE,"E19.sketch_text.stroke-21"),sQuery(id+"F3.wireOp",EDGE,"E19.sketch_text.stroke-22"),sQuery(id+"F3.wireOp",EDGE,"E19.sketch_text.stroke-23"),sQuery(id+"F3.wireOp",EDGE,"E19.sketch_text.stroke-24"),sQuery(id+"F3.wireOp",EDGE,"E19.sketch_text.stroke-25"),sQuery(id+"F3.wireOp",EDGE,"E20.sketch_text.stroke-0"),sQuery(id+"F3.wireOp",EDGE,"E20.sketch_text.stroke-1"),sQuery(id+"F3.wireOp",EDGE,"E20.sketch_text.stroke-2"),sQuery(id+"F3.wireOp",EDGE,"E20.sketch_text.stroke-3"),sQuery(id+"F3.wireOp",EDGE,"E20.sketch_text.stroke-4"),sQuery(id+"F3.wireOp",EDGE,"E20.sketch_text.stroke-5"),sQuery(id+"F3.wireOp",EDGE,"E20.sketch_text.stroke-6"),sQuery(id+"F3.wireOp",EDGE,"E20.sketch_text.stroke-7"),sQuery(id+"F3.wireOp",EDGE,"E20.sketch_text.stroke-8"),sQuery(id+"F3.wireOp",EDGE,"E20.sketch_text.stroke-9"),sQuery(id+"F3.wireOp",EDGE,"E20.sketch_text.stroke-10"),sQuery(id+"F3.wireOp",EDGE,"E20.sketch_text.stroke-11"),sQuery(id+"F3.wireOp",EDGE,"E20.sketch_text.stroke-12"),sQuery(id+"F3.wireOp",EDGE,"E20.sketch_text.stroke-13"),sQuery(id+"F3.wireOp",EDGE,"E20.sketch_text.stroke-14"),sQuery(id+"F3.wireOp",EDGE,"E20.sketch_text.stroke-15"),sQuery(id+"F3.wireOp",EDGE,"E20.sketch_text.stroke-16")])],"isStart":false});var subQ2=makeQuery(id+"F16.opExtrude","SWEPT_FACE",FACE,{"disambiguationData":[OSD([subQ0])]});Q17=makeQuery(id+"F27.boolean.opBoolean","MERGE",EDGE,{"derivedFrom":[makeQuery(id+"F18.boolean.opBoolean","INTERSECT",EDGE,{"disambiguationData":[OD(0.0)],"derivedFrom":[subQ2,subQ1]}),makeQuery(id+"F18.boolean.opBoolean","INTERSECT",EDGE,{"disambiguationData":[OD(1.0)],"derivedFrom":[subQ2,subQ1]})],"fromTools":[makeQuery(id+"F27.opExtrude","CAP_EDGE",EDGE,{"disambiguationData":[OSD([subQ0])],"isStart":false})]});}
            var Q18;
            {var subQ0=sQuery(id+"F15.wireOp",EDGE,"E100.trimOffspring");var subQ2=makeQuery(id+"F16.opExtrude","SWEPT_FACE",FACE,{"disambiguationData":[OSD([subQ0])]});var subQ3=sQuery(id+"F3.wireOp",EDGE,"E19.sketch_text.stroke-14");var subQ4=sQuery(id+"F3.wireOp",EDGE,"E19.sketch_text.stroke-17");var subQ5=makeQuery(id+"F16.opExtrude","CAP_EDGE",EDGE,{"disambiguationData":[OSD([subQ0])],"isStart":true});var subQ6=sQuery(id+"F3.wireOp",EDGE,"E19.sketch_text.stroke-11");var subQ7=sQuery(id+"F3.wireOp",EDGE,"E19.sketch_text.stroke-12");var subQ8=makeQuery(id+"F18.opExtrude","CAP_FACE",FACE,{"disambiguationData":[OSD([sQuery(id+"F3.wireOp",EDGE,"E0"),sQuery(id+"F3.wireOp",EDGE,"E1"),sQuery(id+"F3.wireOp",EDGE,"E2"),sQuery(id+"F3.wireOp",EDGE,"E3"),sQuery(id+"F3.wireOp",EDGE,"E4"),sQuery(id+"F3.wireOp",EDGE,"E5"),sQuery(id+"F3.wireOp",EDGE,"E6"),sQuery(id+"F3.wireOp",EDGE,"E7"),sQuery(id+"F3.wireOp",EDGE,"E8"),sQuery(id+"F3.wireOp",EDGE,"E9"),sQuery(id+"F3.wireOp",EDGE,"E10"),sQuery(id+"F3.wireOp",EDGE,"E11"),sQuery(id+"F3.wireOp",EDGE,"E12.filletArc"),sQuery(id+"F3.wireOp",EDGE,"E13.filletArc"),sQuery(id+"F3.wireOp",EDGE,"E14.filletArc"),sQuery(id+"F3.wireOp",EDGE,"E15.filletArc"),sQuery(id+"F3.wireOp",EDGE,"E16"),sQuery(id+"F3.wireOp",EDGE,"E17.sketch_text.stroke-0"),sQuery(id+"F3.wireOp",EDGE,"E17.sketch_text.stroke-1"),sQuery(id+"F3.wireOp",EDGE,"E17.sketch_text.stroke-2"),sQuery(id+"F3.wireOp",EDGE,"E17.sketch_text.stroke-3"),sQuery(id+"F3.wireOp",EDGE,"E17.sketch_text.stroke-4"),sQuery(id+"F3.wireOp",EDGE,"E17.sketch_text.stroke-5"),sQuery(id+"F3.wireOp",EDGE,"E17.sketch_text.stroke-6"),sQuery(id+"F3.wireOp",EDGE,"E17.sketch_text.stroke-7"),sQuery(id+"F3.wireOp",EDGE,"E17.sketch_text.stroke-8"),sQuery(id+"F3.wireOp",EDGE,"E17.sketch_text.stroke-9"),sQuery(id+"F3.wireOp",EDGE,"E17.sketch_text.stroke-10"),sQuery(id+"F3.wireOp",EDGE,"E17.sketch_text.stroke-11"),sQuery(id+"F3.wireOp",EDGE,"E17.sketch_text.stroke-12"),sQuery(id+"F3.wireOp",EDGE,"E17.sketch_text.stroke-13"),sQuery(id+"F3.wireOp",EDGE,"E17.sketch_text.stroke-14"),sQuery(id+"F3.wireOp",EDGE,"E17.sketch_text.stroke-15"),sQuery(id+"F3.wireOp",EDGE,"E17.sketch_text.stroke-16"),sQuery(id+"F3.wireOp",EDGE,"E17.sketch_text.stroke-17"),sQuery(id+"F3.wireOp",EDGE,"E17.sketch_text.stroke-18"),sQuery(id+"F3.wireOp",EDGE,"E17.sketch_text.stroke-19"),sQuery(id+"F3.wireOp",EDGE,"E17.sketch_text.stroke-20"),sQuery(id+"F3.wireOp",EDGE,"E17.sketch_text.stroke-21"),sQuery(id+"F3.wireOp",EDGE,"E17.sketch_text.stroke-22"),sQuery(id+"F3.wireOp",EDGE,"E17.sketch_text.stroke-23"),sQuery(id+"F3.wireOp",EDGE,"E17.sketch_text.stroke-24"),sQuery(id+"F3.wireOp",EDGE,"E17.sketch_text.stroke-25"),sQuery(id+"F3.wireOp",EDGE,"E17.sketch_text.stroke-26"),sQuery(id+"F3.wireOp",EDGE,"E17.sketch_text.stroke-27"),sQuery(id+"F3.wireOp",EDGE,"E17.sketch_text.stroke-28"),sQuery(id+"F3.wireOp",EDGE,"E17.sketch_text.stroke-29"),sQuery(id+"F3.wireOp",EDGE,"E17.sketch_text.stroke-30"),sQuery(id+"F3.wireOp",EDGE,"E17.sketch_text.stroke-31"),sQuery(id+"F3.wireOp",EDGE,"E18.sketch_text.stroke-0"),sQuery(id+"F3.wireOp",EDGE,"E18.sketch_text.stroke-1"),sQuery(id+"F3.wireOp",EDGE,"E18.sketch_text.stroke-2"),sQuery(id+"F3.wireOp",EDGE,"E18.sketch_text.stroke-3"),sQuery(id+"F3.wireOp",EDGE,"E18.sketch_text.stroke-4"),sQuery(id+"F3.wireOp",EDGE,"E18.sketch_text.stroke-5"),sQuery(id+"F3.wireOp",EDGE,"E18.sketch_text.stroke-6"),sQuery(id+"F3.wireOp",EDGE,"E18.sketch_text.stroke-7"),sQuery(id+"F3.wireOp",EDGE,"E18.sketch_text.stroke-8"),sQuery(id+"F3.wireOp",EDGE,"E18.sketch_text.stroke-9"),sQuery(id+"F3.wireOp",EDGE,"E18.sketch_text.stroke-10"),sQuery(id+"F3.wireOp",EDGE,"E18.sketch_text.stroke-11"),sQuery(id+"F3.wireOp",EDGE,"E18.sketch_text.stroke-12"),sQuery(id+"F3.wireOp",EDGE,"E18.sketch_text.stroke-13"),sQuery(id+"F3.wireOp",EDGE,"E18.sketch_text.stroke-14"),sQuery(id+"F3.wireOp",EDGE,"E18.sketch_text.stroke-15"),sQuery(id+"F3.wireOp",EDGE,"E18.sketch_text.stroke-16"),sQuery(id+"F3.wireOp",EDGE,"E18.sketch_text.stroke-17"),sQuery(id+"F3.wireOp",EDGE,"E18.sketch_text.stroke-18"),sQuery(id+"F3.wireOp",EDGE,"E18.sketch_text.stroke-19"),sQuery(id+"F3.wireOp",EDGE,"E18.sketch_text.stroke-20"),sQuery(id+"F3.wireOp",EDGE,"E18.sketch_text.stroke-21"),sQuery(id+"F3.wireOp",EDGE,"E18.sketch_text.stroke-22"),sQuery(id+"F3.wireOp",EDGE,"E18.sketch_text.stroke-23"),sQuery(id+"F3.wireOp",EDGE,"E18.sketch_text.stroke-24"),sQuery(id+"F3.wireOp",EDGE,"E18.sketch_text.stroke-25"),sQuery(id+"F3.wireOp",EDGE,"E18.sketch_text.stroke-26"),sQuery(id+"F3.wireOp",EDGE,"E18.sketch_text.stroke-27"),sQuery(id+"F3.wireOp",EDGE,"E19.sketch_text.stroke-0"),sQuery(id+"F3.wireOp",EDGE,"E19.sketch_text.stroke-1"),sQuery(id+"F3.wireOp",EDGE,"E19.sketch_text.stroke-2"),sQuery(id+"F3.wireOp",EDGE,"E19.sketch_text.stroke-3"),sQuery(id+"F3.wireOp",EDGE,"E19.sketch_text.stroke-4"),sQuery(id+"F3.wireOp",EDGE,"E19.sketch_text.stroke-5"),sQuery(id+"F3.wireOp",EDGE,"E19.sketch_text.stroke-6"),sQuery(id+"F3.wireOp",EDGE,"E19.sketch_text.stroke-7"),sQuery(id+"F3.wireOp",EDGE,"E19.sketch_text.stroke-8"),sQuery(id+"F3.wireOp",EDGE,"E19.sketch_text.stroke-9"),sQuery(id+"F3.wireOp",EDGE,"E19.sketch_text.stroke-10"),subQ6,subQ7,sQuery(id+"F3.wireOp",EDGE,"E19.sketch_text.stroke-13"),subQ3,sQuery(id+"F3.wireOp",EDGE,"E19.sketch_text.stroke-15"),sQuery(id+"F3.wireOp",EDGE,"E19.sketch_text.stroke-16"),subQ4,sQuery(id+"F3.wireOp",EDGE,"E19.sketch_text.stroke-18"),sQuery(id+"F3.wireOp",EDGE,"E19.sketch_text.stroke-19"),sQuery(id+"F3.wireOp",EDGE,"E19.sketch_text.stroke-20"),sQuery(id+"F3.wireOp",EDGE,"E19.sketch_text.stroke-21"),sQuery(id+"F3.wireOp",EDGE,"E19.sketch_text.stroke-22"),sQuery(id+"F3.wireOp",EDGE,"E19.sketch_text.stroke-23"),sQuery(id+"F3.wireOp",EDGE,"E19.sketch_text.stroke-24"),sQuery(id+"F3.wireOp",EDGE,"E19.sketch_text.stroke-25"),sQuery(id+"F3.wireOp",EDGE,"E20.sketch_text.stroke-0"),sQuery(id+"F3.wireOp",EDGE,"E20.sketch_text.stroke-1"),sQuery(id+"F3.wireOp",EDGE,"E20.sketch_text.stroke-2"),sQuery(id+"F3.wireOp",EDGE,"E20.sketch_text.stroke-3"),sQuery(id+"F3.wireOp",EDGE,"E20.sketch_text.stroke-4"),sQuery(id+"F3.wireOp",EDGE,"E20.sketch_text.stroke-5"),sQuery(id+"F3.wireOp",EDGE,"E20.sketch_text.stroke-6"),sQuery(id+"F3.wireOp",EDGE,"E20.sketch_text.stroke-7"),sQuery(id+"F3.wireOp",EDGE,"E20.sketch_text.stroke-8"),sQuery(id+"F3.wireOp",EDGE,"E20.sketch_text.stroke-9"),sQuery(id+"F3.wireOp",EDGE,"E20.sketch_text.stroke-10"),sQuery(id+"F3.wireOp",EDGE,"E20.sketch_text.stroke-11"),sQuery(id+"F3.wireOp",EDGE,"E20.sketch_text.stroke-12"),sQuery(id+"F3.wireOp",EDGE,"E20.sketch_text.stroke-13"),sQuery(id+"F3.wireOp",EDGE,"E20.sketch_text.stroke-14"),sQuery(id+"F3.wireOp",EDGE,"E20.sketch_text.stroke-15"),sQuery(id+"F3.wireOp",EDGE,"E20.sketch_text.stroke-16")])],"isStart":false});Q18=makeQuery(id+"F27.boolean.opBoolean","MERGE",EDGE,{"derivedFrom":[makeQuery(id+"F18.boolean.opBoolean","INTERSECT",EDGE,{"disambiguationData":[OD(0.0)],"derivedFrom":[subQ2,subQ8]}),makeQuery(id+"F18.boolean.opBoolean","INTERSECT",EDGE,{"disambiguationData":[OD(1.0)],"derivedFrom":[subQ2,subQ8]}),makeQuery(id+"F18.boolean.opBoolean","INTERSECT",EDGE,{"disambiguationData":[OD(2.0)],"derivedFrom":[subQ2,subQ8]})],"fromTools":[makeQuery(id+"F27.opExtrude","CAP_EDGE",EDGE,{"disambiguationData":[OSD([subQ0]),TDD([makeQuery(id+"F18.boolean.opBoolean","SPLIT",EDGE,{"disambiguationData":[TD([makeQuery(id+"F18.opExtrude","SWEPT_FACE",FACE,{"disambiguationData":[OSD([subQ6])]})])],"derivedFrom":subQ5})])],"isStart":false}),makeQuery(id+"F27.opExtrude","CAP_EDGE",EDGE,{"disambiguationData":[OSD([subQ0]),TDD([makeQuery(id+"F18.boolean.opBoolean","SPLIT",EDGE,{"disambiguationData":[TD([makeQuery(id+"F18.opExtrude","SWEPT_FACE",FACE,{"disambiguationData":[OSD([subQ3])]})])],"derivedFrom":subQ5})])],"isStart":false})]});}
            var Q19;
            {var subQ0=sQuery(id+"F15.wireOp",EDGE,"E95.0");var subQ1=makeQuery(id+"F18.opExtrude","CAP_FACE",FACE,{"disambiguationData":[OSD([sQuery(id+"F3.wireOp",EDGE,"E0"),sQuery(id+"F3.wireOp",EDGE,"E1"),sQuery(id+"F3.wireOp",EDGE,"E2"),sQuery(id+"F3.wireOp",EDGE,"E3"),sQuery(id+"F3.wireOp",EDGE,"E4"),sQuery(id+"F3.wireOp",EDGE,"E5"),sQuery(id+"F3.wireOp",EDGE,"E6"),sQuery(id+"F3.wireOp",EDGE,"E7"),sQuery(id+"F3.wireOp",EDGE,"E8"),sQuery(id+"F3.wireOp",EDGE,"E9"),sQuery(id+"F3.wireOp",EDGE,"E10"),sQuery(id+"F3.wireOp",EDGE,"E11"),sQuery(id+"F3.wireOp",EDGE,"E12.filletArc"),sQuery(id+"F3.wireOp",EDGE,"E13.filletArc"),sQuery(id+"F3.wireOp",EDGE,"E14.filletArc"),sQuery(id+"F3.wireOp",EDGE,"E15.filletArc"),sQuery(id+"F3.wireOp",EDGE,"E16"),sQuery(id+"F3.wireOp",EDGE,"E17.sketch_text.stroke-0"),sQuery(id+"F3.wireOp",EDGE,"E17.sketch_text.stroke-1"),sQuery(id+"F3.wireOp",EDGE,"E17.sketch_text.stroke-2"),sQuery(id+"F3.wireOp",EDGE,"E17.sketch_text.stroke-3"),sQuery(id+"F3.wireOp",EDGE,"E17.sketch_text.stroke-4"),sQuery(id+"F3.wireOp",EDGE,"E17.sketch_text.stroke-5"),sQuery(id+"F3.wireOp",EDGE,"E17.sketch_text.stroke-6"),sQuery(id+"F3.wireOp",EDGE,"E17.sketch_text.stroke-7"),sQuery(id+"F3.wireOp",EDGE,"E17.sketch_text.stroke-8"),sQuery(id+"F3.wireOp",EDGE,"E17.sketch_text.stroke-9"),sQuery(id+"F3.wireOp",EDGE,"E17.sketch_text.stroke-10"),sQuery(id+"F3.wireOp",EDGE,"E17.sketch_text.stroke-11"),sQuery(id+"F3.wireOp",EDGE,"E17.sketch_text.stroke-12"),sQuery(id+"F3.wireOp",EDGE,"E17.sketch_text.stroke-13"),sQuery(id+"F3.wireOp",EDGE,"E17.sketch_text.stroke-14"),sQuery(id+"F3.wireOp",EDGE,"E17.sketch_text.stroke-15"),sQuery(id+"F3.wireOp",EDGE,"E17.sketch_text.stroke-16"),sQuery(id+"F3.wireOp",EDGE,"E17.sketch_text.stroke-17"),sQuery(id+"F3.wireOp",EDGE,"E17.sketch_text.stroke-18"),sQuery(id+"F3.wireOp",EDGE,"E17.sketch_text.stroke-19"),sQuery(id+"F3.wireOp",EDGE,"E17.sketch_text.stroke-20"),sQuery(id+"F3.wireOp",EDGE,"E17.sketch_text.stroke-21"),sQuery(id+"F3.wireOp",EDGE,"E17.sketch_text.stroke-22"),sQuery(id+"F3.wireOp",EDGE,"E17.sketch_text.stroke-23"),sQuery(id+"F3.wireOp",EDGE,"E17.sketch_text.stroke-24"),sQuery(id+"F3.wireOp",EDGE,"E17.sketch_text.stroke-25"),sQuery(id+"F3.wireOp",EDGE,"E17.sketch_text.stroke-26"),sQuery(id+"F3.wireOp",EDGE,"E17.sketch_text.stroke-27"),sQuery(id+"F3.wireOp",EDGE,"E17.sketch_text.stroke-28"),sQuery(id+"F3.wireOp",EDGE,"E17.sketch_text.stroke-29"),sQuery(id+"F3.wireOp",EDGE,"E17.sketch_text.stroke-30"),sQuery(id+"F3.wireOp",EDGE,"E17.sketch_text.stroke-31"),sQuery(id+"F3.wireOp",EDGE,"E18.sketch_text.stroke-0"),sQuery(id+"F3.wireOp",EDGE,"E18.sketch_text.stroke-1"),sQuery(id+"F3.wireOp",EDGE,"E18.sketch_text.stroke-2"),sQuery(id+"F3.wireOp",EDGE,"E18.sketch_text.stroke-3"),sQuery(id+"F3.wireOp",EDGE,"E18.sketch_text.stroke-4"),sQuery(id+"F3.wireOp",EDGE,"E18.sketch_text.stroke-5"),sQuery(id+"F3.wireOp",EDGE,"E18.sketch_text.stroke-6"),sQuery(id+"F3.wireOp",EDGE,"E18.sketch_text.stroke-7"),sQuery(id+"F3.wireOp",EDGE,"E18.sketch_text.stroke-8"),sQuery(id+"F3.wireOp",EDGE,"E18.sketch_text.stroke-9"),sQuery(id+"F3.wireOp",EDGE,"E18.sketch_text.stroke-10"),sQuery(id+"F3.wireOp",EDGE,"E18.sketch_text.stroke-11"),sQuery(id+"F3.wireOp",EDGE,"E18.sketch_text.stroke-12"),sQuery(id+"F3.wireOp",EDGE,"E18.sketch_text.stroke-13"),sQuery(id+"F3.wireOp",EDGE,"E18.sketch_text.stroke-14"),sQuery(id+"F3.wireOp",EDGE,"E18.sketch_text.stroke-15"),sQuery(id+"F3.wireOp",EDGE,"E18.sketch_text.stroke-16"),sQuery(id+"F3.wireOp",EDGE,"E18.sketch_text.stroke-17"),sQuery(id+"F3.wireOp",EDGE,"E18.sketch_text.stroke-18"),sQuery(id+"F3.wireOp",EDGE,"E18.sketch_text.stroke-19"),sQuery(id+"F3.wireOp",EDGE,"E18.sketch_text.stroke-20"),sQuery(id+"F3.wireOp",EDGE,"E18.sketch_text.stroke-21"),sQuery(id+"F3.wireOp",EDGE,"E18.sketch_text.stroke-22"),sQuery(id+"F3.wireOp",EDGE,"E18.sketch_text.stroke-23"),sQuery(id+"F3.wireOp",EDGE,"E18.sketch_text.stroke-24"),sQuery(id+"F3.wireOp",EDGE,"E18.sketch_text.stroke-25"),sQuery(id+"F3.wireOp",EDGE,"E18.sketch_text.stroke-26"),sQuery(id+"F3.wireOp",EDGE,"E18.sketch_text.stroke-27"),sQuery(id+"F3.wireOp",EDGE,"E19.sketch_text.stroke-0"),sQuery(id+"F3.wireOp",EDGE,"E19.sketch_text.stroke-1"),sQuery(id+"F3.wireOp",EDGE,"E19.sketch_text.stroke-2"),sQuery(id+"F3.wireOp",EDGE,"E19.sketch_text.stroke-3"),sQuery(id+"F3.wireOp",EDGE,"E19.sketch_text.stroke-4"),sQuery(id+"F3.wireOp",EDGE,"E19.sketch_text.stroke-5"),sQuery(id+"F3.wireOp",EDGE,"E19.sketch_text.stroke-6"),sQuery(id+"F3.wireOp",EDGE,"E19.sketch_text.stroke-7"),sQuery(id+"F3.wireOp",EDGE,"E19.sketch_text.stroke-8"),sQuery(id+"F3.wireOp",EDGE,"E19.sketch_text.stroke-9"),sQuery(id+"F3.wireOp",EDGE,"E19.sketch_text.stroke-10"),sQuery(id+"F3.wireOp",EDGE,"E19.sketch_text.stroke-11"),sQuery(id+"F3.wireOp",EDGE,"E19.sketch_text.stroke-12"),sQuery(id+"F3.wireOp",EDGE,"E19.sketch_text.stroke-13"),sQuery(id+"F3.wireOp",EDGE,"E19.sketch_text.stroke-14"),sQuery(id+"F3.wireOp",EDGE,"E19.sketch_text.stroke-15"),sQuery(id+"F3.wireOp",EDGE,"E19.sketch_text.stroke-16"),sQuery(id+"F3.wireOp",EDGE,"E19.sketch_text.stroke-17"),sQuery(id+"F3.wireOp",EDGE,"E19.sketch_text.stroke-18"),sQuery(id+"F3.wireOp",EDGE,"E19.sketch_text.stroke-19"),sQuery(id+"F3.wireOp",EDGE,"E19.sketch_text.stroke-20"),sQuery(id+"F3.wireOp",EDGE,"E19.sketch_text.stroke-21"),sQuery(id+"F3.wireOp",EDGE,"E19.sketch_text.stroke-22"),sQuery(id+"F3.wireOp",EDGE,"E19.sketch_text.stroke-23"),sQuery(id+"F3.wireOp",EDGE,"E19.sketch_text.stroke-24"),sQuery(id+"F3.wireOp",EDGE,"E19.sketch_text.stroke-25"),sQuery(id+"F3.wireOp",EDGE,"E20.sketch_text.stroke-0"),sQuery(id+"F3.wireOp",EDGE,"E20.sketch_text.stroke-1"),sQuery(id+"F3.wireOp",EDGE,"E20.sketch_text.stroke-2"),sQuery(id+"F3.wireOp",EDGE,"E20.sketch_text.stroke-3"),sQuery(id+"F3.wireOp",EDGE,"E20.sketch_text.stroke-4"),sQuery(id+"F3.wireOp",EDGE,"E20.sketch_text.stroke-5"),sQuery(id+"F3.wireOp",EDGE,"E20.sketch_text.stroke-6"),sQuery(id+"F3.wireOp",EDGE,"E20.sketch_text.stroke-7"),sQuery(id+"F3.wireOp",EDGE,"E20.sketch_text.stroke-8"),sQuery(id+"F3.wireOp",EDGE,"E20.sketch_text.stroke-9"),sQuery(id+"F3.wireOp",EDGE,"E20.sketch_text.stroke-10"),sQuery(id+"F3.wireOp",EDGE,"E20.sketch_text.stroke-11"),sQuery(id+"F3.wireOp",EDGE,"E20.sketch_text.stroke-12"),sQuery(id+"F3.wireOp",EDGE,"E20.sketch_text.stroke-13"),sQuery(id+"F3.wireOp",EDGE,"E20.sketch_text.stroke-14"),sQuery(id+"F3.wireOp",EDGE,"E20.sketch_text.stroke-15"),sQuery(id+"F3.wireOp",EDGE,"E20.sketch_text.stroke-16")])],"isStart":false});var subQ2=makeQuery(id+"F16.opExtrude","SWEPT_FACE",FACE,{"disambiguationData":[OSD([subQ0])]});Q19=makeQuery(id+"F27.boolean.opBoolean","MERGE",EDGE,{"derivedFrom":[makeQuery(id+"F18.boolean.opBoolean","INTERSECT",EDGE,{"disambiguationData":[OD(0.0)],"derivedFrom":[subQ2,subQ1]}),makeQuery(id+"F18.boolean.opBoolean","INTERSECT",EDGE,{"disambiguationData":[OD(1.0)],"derivedFrom":[subQ2,subQ1]})],"fromTools":[makeQuery(id+"F27.opExtrude","CAP_EDGE",EDGE,{"disambiguationData":[OSD([subQ0])],"isStart":false})]});}
            var Q20;
            {var subQ0=sQuery(id+"F15.wireOp",EDGE,"E96.trimOffspring");var subQ1=makeQuery(id+"F18.opExtrude","CAP_FACE",FACE,{"disambiguationData":[OSD([sQuery(id+"F3.wireOp",EDGE,"E0"),sQuery(id+"F3.wireOp",EDGE,"E1"),sQuery(id+"F3.wireOp",EDGE,"E2"),sQuery(id+"F3.wireOp",EDGE,"E3"),sQuery(id+"F3.wireOp",EDGE,"E4"),sQuery(id+"F3.wireOp",EDGE,"E5"),sQuery(id+"F3.wireOp",EDGE,"E6"),sQuery(id+"F3.wireOp",EDGE,"E7"),sQuery(id+"F3.wireOp",EDGE,"E8"),sQuery(id+"F3.wireOp",EDGE,"E9"),sQuery(id+"F3.wireOp",EDGE,"E10"),sQuery(id+"F3.wireOp",EDGE,"E11"),sQuery(id+"F3.wireOp",EDGE,"E12.filletArc"),sQuery(id+"F3.wireOp",EDGE,"E13.filletArc"),sQuery(id+"F3.wireOp",EDGE,"E14.filletArc"),sQuery(id+"F3.wireOp",EDGE,"E15.filletArc"),sQuery(id+"F3.wireOp",EDGE,"E16"),sQuery(id+"F3.wireOp",EDGE,"E17.sketch_text.stroke-0"),sQuery(id+"F3.wireOp",EDGE,"E17.sketch_text.stroke-1"),sQuery(id+"F3.wireOp",EDGE,"E17.sketch_text.stroke-2"),sQuery(id+"F3.wireOp",EDGE,"E17.sketch_text.stroke-3"),sQuery(id+"F3.wireOp",EDGE,"E17.sketch_text.stroke-4"),sQuery(id+"F3.wireOp",EDGE,"E17.sketch_text.stroke-5"),sQuery(id+"F3.wireOp",EDGE,"E17.sketch_text.stroke-6"),sQuery(id+"F3.wireOp",EDGE,"E17.sketch_text.stroke-7"),sQuery(id+"F3.wireOp",EDGE,"E17.sketch_text.stroke-8"),sQuery(id+"F3.wireOp",EDGE,"E17.sketch_text.stroke-9"),sQuery(id+"F3.wireOp",EDGE,"E17.sketch_text.stroke-10"),sQuery(id+"F3.wireOp",EDGE,"E17.sketch_text.stroke-11"),sQuery(id+"F3.wireOp",EDGE,"E17.sketch_text.stroke-12"),sQuery(id+"F3.wireOp",EDGE,"E17.sketch_text.stroke-13"),sQuery(id+"F3.wireOp",EDGE,"E17.sketch_text.stroke-14"),sQuery(id+"F3.wireOp",EDGE,"E17.sketch_text.stroke-15"),sQuery(id+"F3.wireOp",EDGE,"E17.sketch_text.stroke-16"),sQuery(id+"F3.wireOp",EDGE,"E17.sketch_text.stroke-17"),sQuery(id+"F3.wireOp",EDGE,"E17.sketch_text.stroke-18"),sQuery(id+"F3.wireOp",EDGE,"E17.sketch_text.stroke-19"),sQuery(id+"F3.wireOp",EDGE,"E17.sketch_text.stroke-20"),sQuery(id+"F3.wireOp",EDGE,"E17.sketch_text.stroke-21"),sQuery(id+"F3.wireOp",EDGE,"E17.sketch_text.stroke-22"),sQuery(id+"F3.wireOp",EDGE,"E17.sketch_text.stroke-23"),sQuery(id+"F3.wireOp",EDGE,"E17.sketch_text.stroke-24"),sQuery(id+"F3.wireOp",EDGE,"E17.sketch_text.stroke-25"),sQuery(id+"F3.wireOp",EDGE,"E17.sketch_text.stroke-26"),sQuery(id+"F3.wireOp",EDGE,"E17.sketch_text.stroke-27"),sQuery(id+"F3.wireOp",EDGE,"E17.sketch_text.stroke-28"),sQuery(id+"F3.wireOp",EDGE,"E17.sketch_text.stroke-29"),sQuery(id+"F3.wireOp",EDGE,"E17.sketch_text.stroke-30"),sQuery(id+"F3.wireOp",EDGE,"E17.sketch_text.stroke-31"),sQuery(id+"F3.wireOp",EDGE,"E18.sketch_text.stroke-0"),sQuery(id+"F3.wireOp",EDGE,"E18.sketch_text.stroke-1"),sQuery(id+"F3.wireOp",EDGE,"E18.sketch_text.stroke-2"),sQuery(id+"F3.wireOp",EDGE,"E18.sketch_text.stroke-3"),sQuery(id+"F3.wireOp",EDGE,"E18.sketch_text.stroke-4"),sQuery(id+"F3.wireOp",EDGE,"E18.sketch_text.stroke-5"),sQuery(id+"F3.wireOp",EDGE,"E18.sketch_text.stroke-6"),sQuery(id+"F3.wireOp",EDGE,"E18.sketch_text.stroke-7"),sQuery(id+"F3.wireOp",EDGE,"E18.sketch_text.stroke-8"),sQuery(id+"F3.wireOp",EDGE,"E18.sketch_text.stroke-9"),sQuery(id+"F3.wireOp",EDGE,"E18.sketch_text.stroke-10"),sQuery(id+"F3.wireOp",EDGE,"E18.sketch_text.stroke-11"),sQuery(id+"F3.wireOp",EDGE,"E18.sketch_text.stroke-12"),sQuery(id+"F3.wireOp",EDGE,"E18.sketch_text.stroke-13"),sQuery(id+"F3.wireOp",EDGE,"E18.sketch_text.stroke-14"),sQuery(id+"F3.wireOp",EDGE,"E18.sketch_text.stroke-15"),sQuery(id+"F3.wireOp",EDGE,"E18.sketch_text.stroke-16"),sQuery(id+"F3.wireOp",EDGE,"E18.sketch_text.stroke-17"),sQuery(id+"F3.wireOp",EDGE,"E18.sketch_text.stroke-18"),sQuery(id+"F3.wireOp",EDGE,"E18.sketch_text.stroke-19"),sQuery(id+"F3.wireOp",EDGE,"E18.sketch_text.stroke-20"),sQuery(id+"F3.wireOp",EDGE,"E18.sketch_text.stroke-21"),sQuery(id+"F3.wireOp",EDGE,"E18.sketch_text.stroke-22"),sQuery(id+"F3.wireOp",EDGE,"E18.sketch_text.stroke-23"),sQuery(id+"F3.wireOp",EDGE,"E18.sketch_text.stroke-24"),sQuery(id+"F3.wireOp",EDGE,"E18.sketch_text.stroke-25"),sQuery(id+"F3.wireOp",EDGE,"E18.sketch_text.stroke-26"),sQuery(id+"F3.wireOp",EDGE,"E18.sketch_text.stroke-27"),sQuery(id+"F3.wireOp",EDGE,"E19.sketch_text.stroke-0"),sQuery(id+"F3.wireOp",EDGE,"E19.sketch_text.stroke-1"),sQuery(id+"F3.wireOp",EDGE,"E19.sketch_text.stroke-2"),sQuery(id+"F3.wireOp",EDGE,"E19.sketch_text.stroke-3"),sQuery(id+"F3.wireOp",EDGE,"E19.sketch_text.stroke-4"),sQuery(id+"F3.wireOp",EDGE,"E19.sketch_text.stroke-5"),sQuery(id+"F3.wireOp",EDGE,"E19.sketch_text.stroke-6"),sQuery(id+"F3.wireOp",EDGE,"E19.sketch_text.stroke-7"),sQuery(id+"F3.wireOp",EDGE,"E19.sketch_text.stroke-8"),sQuery(id+"F3.wireOp",EDGE,"E19.sketch_text.stroke-9"),sQuery(id+"F3.wireOp",EDGE,"E19.sketch_text.stroke-10"),sQuery(id+"F3.wireOp",EDGE,"E19.sketch_text.stroke-11"),sQuery(id+"F3.wireOp",EDGE,"E19.sketch_text.stroke-12"),sQuery(id+"F3.wireOp",EDGE,"E19.sketch_text.stroke-13"),sQuery(id+"F3.wireOp",EDGE,"E19.sketch_text.stroke-14"),sQuery(id+"F3.wireOp",EDGE,"E19.sketch_text.stroke-15"),sQuery(id+"F3.wireOp",EDGE,"E19.sketch_text.stroke-16"),sQuery(id+"F3.wireOp",EDGE,"E19.sketch_text.stroke-17"),sQuery(id+"F3.wireOp",EDGE,"E19.sketch_text.stroke-18"),sQuery(id+"F3.wireOp",EDGE,"E19.sketch_text.stroke-19"),sQuery(id+"F3.wireOp",EDGE,"E19.sketch_text.stroke-20"),sQuery(id+"F3.wireOp",EDGE,"E19.sketch_text.stroke-21"),sQuery(id+"F3.wireOp",EDGE,"E19.sketch_text.stroke-22"),sQuery(id+"F3.wireOp",EDGE,"E19.sketch_text.stroke-23"),sQuery(id+"F3.wireOp",EDGE,"E19.sketch_text.stroke-24"),sQuery(id+"F3.wireOp",EDGE,"E19.sketch_text.stroke-25"),sQuery(id+"F3.wireOp",EDGE,"E20.sketch_text.stroke-0"),sQuery(id+"F3.wireOp",EDGE,"E20.sketch_text.stroke-1"),sQuery(id+"F3.wireOp",EDGE,"E20.sketch_text.stroke-2"),sQuery(id+"F3.wireOp",EDGE,"E20.sketch_text.stroke-3"),sQuery(id+"F3.wireOp",EDGE,"E20.sketch_text.stroke-4"),sQuery(id+"F3.wireOp",EDGE,"E20.sketch_text.stroke-5"),sQuery(id+"F3.wireOp",EDGE,"E20.sketch_text.stroke-6"),sQuery(id+"F3.wireOp",EDGE,"E20.sketch_text.stroke-7"),sQuery(id+"F3.wireOp",EDGE,"E20.sketch_text.stroke-8"),sQuery(id+"F3.wireOp",EDGE,"E20.sketch_text.stroke-9"),sQuery(id+"F3.wireOp",EDGE,"E20.sketch_text.stroke-10"),sQuery(id+"F3.wireOp",EDGE,"E20.sketch_text.stroke-11"),sQuery(id+"F3.wireOp",EDGE,"E20.sketch_text.stroke-12"),sQuery(id+"F3.wireOp",EDGE,"E20.sketch_text.stroke-13"),sQuery(id+"F3.wireOp",EDGE,"E20.sketch_text.stroke-14"),sQuery(id+"F3.wireOp",EDGE,"E20.sketch_text.stroke-15"),sQuery(id+"F3.wireOp",EDGE,"E20.sketch_text.stroke-16")])],"isStart":false});var subQ2=makeQuery(id+"F16.opExtrude","SWEPT_FACE",FACE,{"disambiguationData":[OSD([subQ0])]});Q20=makeQuery(id+"F27.boolean.opBoolean","MERGE",EDGE,{"derivedFrom":[makeQuery(id+"F18.boolean.opBoolean","INTERSECT",EDGE,{"disambiguationData":[OD(0.0)],"derivedFrom":[subQ2,subQ1]}),makeQuery(id+"F18.boolean.opBoolean","INTERSECT",EDGE,{"disambiguationData":[OD(1.0)],"derivedFrom":[subQ2,subQ1]})],"fromTools":[makeQuery(id+"F27.opExtrude","CAP_EDGE",EDGE,{"disambiguationData":[OSD([subQ0])],"isStart":false})]});}
            var Q21;
            Q21=makeQuery(id+"F18.boolean.opBoolean","INTERSECT",EDGE,{"derivedFrom":[makeQuery(id+"F16.opExtrude","SWEPT_FACE",FACE,{"disambiguationData":[OSD([sQuery(id+"F15.wireOp",EDGE,"E105.1")])]}),makeQuery(id+"F18.opExtrude","CAP_FACE",FACE,{"disambiguationData":[OSD([sQuery(id+"F3.wireOp",EDGE,"E0"),sQuery(id+"F3.wireOp",EDGE,"E1"),sQuery(id+"F3.wireOp",EDGE,"E2"),sQuery(id+"F3.wireOp",EDGE,"E3"),sQuery(id+"F3.wireOp",EDGE,"E4"),sQuery(id+"F3.wireOp",EDGE,"E5"),sQuery(id+"F3.wireOp",EDGE,"E6"),sQuery(id+"F3.wireOp",EDGE,"E7"),sQuery(id+"F3.wireOp",EDGE,"E8"),sQuery(id+"F3.wireOp",EDGE,"E9"),sQuery(id+"F3.wireOp",EDGE,"E10"),sQuery(id+"F3.wireOp",EDGE,"E11"),sQuery(id+"F3.wireOp",EDGE,"E12.filletArc"),sQuery(id+"F3.wireOp",EDGE,"E13.filletArc"),sQuery(id+"F3.wireOp",EDGE,"E14.filletArc"),sQuery(id+"F3.wireOp",EDGE,"E15.filletArc"),sQuery(id+"F3.wireOp",EDGE,"E16"),sQuery(id+"F3.wireOp",EDGE,"E17.sketch_text.stroke-0"),sQuery(id+"F3.wireOp",EDGE,"E17.sketch_text.stroke-1"),sQuery(id+"F3.wireOp",EDGE,"E17.sketch_text.stroke-2"),sQuery(id+"F3.wireOp",EDGE,"E17.sketch_text.stroke-3"),sQuery(id+"F3.wireOp",EDGE,"E17.sketch_text.stroke-4"),sQuery(id+"F3.wireOp",EDGE,"E17.sketch_text.stroke-5"),sQuery(id+"F3.wireOp",EDGE,"E17.sketch_text.stroke-6"),sQuery(id+"F3.wireOp",EDGE,"E17.sketch_text.stroke-7"),sQuery(id+"F3.wireOp",EDGE,"E17.sketch_text.stroke-8"),sQuery(id+"F3.wireOp",EDGE,"E17.sketch_text.stroke-9"),sQuery(id+"F3.wireOp",EDGE,"E17.sketch_text.stroke-10"),sQuery(id+"F3.wireOp",EDGE,"E17.sketch_text.stroke-11"),sQuery(id+"F3.wireOp",EDGE,"E17.sketch_text.stroke-12"),sQuery(id+"F3.wireOp",EDGE,"E17.sketch_text.stroke-13"),sQuery(id+"F3.wireOp",EDGE,"E17.sketch_text.stroke-14"),sQuery(id+"F3.wireOp",EDGE,"E17.sketch_text.stroke-15"),sQuery(id+"F3.wireOp",EDGE,"E17.sketch_text.stroke-16"),sQuery(id+"F3.wireOp",EDGE,"E17.sketch_text.stroke-17"),sQuery(id+"F3.wireOp",EDGE,"E17.sketch_text.stroke-18"),sQuery(id+"F3.wireOp",EDGE,"E17.sketch_text.stroke-19"),sQuery(id+"F3.wireOp",EDGE,"E17.sketch_text.stroke-20"),sQuery(id+"F3.wireOp",EDGE,"E17.sketch_text.stroke-21"),sQuery(id+"F3.wireOp",EDGE,"E17.sketch_text.stroke-22"),sQuery(id+"F3.wireOp",EDGE,"E17.sketch_text.stroke-23"),sQuery(id+"F3.wireOp",EDGE,"E17.sketch_text.stroke-24"),sQuery(id+"F3.wireOp",EDGE,"E17.sketch_text.stroke-25"),sQuery(id+"F3.wireOp",EDGE,"E17.sketch_text.stroke-26"),sQuery(id+"F3.wireOp",EDGE,"E17.sketch_text.stroke-27"),sQuery(id+"F3.wireOp",EDGE,"E17.sketch_text.stroke-28"),sQuery(id+"F3.wireOp",EDGE,"E17.sketch_text.stroke-29"),sQuery(id+"F3.wireOp",EDGE,"E17.sketch_text.stroke-30"),sQuery(id+"F3.wireOp",EDGE,"E17.sketch_text.stroke-31"),sQuery(id+"F3.wireOp",EDGE,"E18.sketch_text.stroke-0"),sQuery(id+"F3.wireOp",EDGE,"E18.sketch_text.stroke-1"),sQuery(id+"F3.wireOp",EDGE,"E18.sketch_text.stroke-2"),sQuery(id+"F3.wireOp",EDGE,"E18.sketch_text.stroke-3"),sQuery(id+"F3.wireOp",EDGE,"E18.sketch_text.stroke-4"),sQuery(id+"F3.wireOp",EDGE,"E18.sketch_text.stroke-5"),sQuery(id+"F3.wireOp",EDGE,"E18.sketch_text.stroke-6"),sQuery(id+"F3.wireOp",EDGE,"E18.sketch_text.stroke-7"),sQuery(id+"F3.wireOp",EDGE,"E18.sketch_text.stroke-8"),sQuery(id+"F3.wireOp",EDGE,"E18.sketch_text.stroke-9"),sQuery(id+"F3.wireOp",EDGE,"E18.sketch_text.stroke-10"),sQuery(id+"F3.wireOp",EDGE,"E18.sketch_text.stroke-11"),sQuery(id+"F3.wireOp",EDGE,"E18.sketch_text.stroke-12"),sQuery(id+"F3.wireOp",EDGE,"E18.sketch_text.stroke-13"),sQuery(id+"F3.wireOp",EDGE,"E18.sketch_text.stroke-14"),sQuery(id+"F3.wireOp",EDGE,"E18.sketch_text.stroke-15"),sQuery(id+"F3.wireOp",EDGE,"E18.sketch_text.stroke-16"),sQuery(id+"F3.wireOp",EDGE,"E18.sketch_text.stroke-17"),sQuery(id+"F3.wireOp",EDGE,"E18.sketch_text.stroke-18"),sQuery(id+"F3.wireOp",EDGE,"E18.sketch_text.stroke-19"),sQuery(id+"F3.wireOp",EDGE,"E18.sketch_text.stroke-20"),sQuery(id+"F3.wireOp",EDGE,"E18.sketch_text.stroke-21"),sQuery(id+"F3.wireOp",EDGE,"E18.sketch_text.stroke-22"),sQuery(id+"F3.wireOp",EDGE,"E18.sketch_text.stroke-23"),sQuery(id+"F3.wireOp",EDGE,"E18.sketch_text.stroke-24"),sQuery(id+"F3.wireOp",EDGE,"E18.sketch_text.stroke-25"),sQuery(id+"F3.wireOp",EDGE,"E18.sketch_text.stroke-26"),sQuery(id+"F3.wireOp",EDGE,"E18.sketch_text.stroke-27"),sQuery(id+"F3.wireOp",EDGE,"E19.sketch_text.stroke-0"),sQuery(id+"F3.wireOp",EDGE,"E19.sketch_text.stroke-1"),sQuery(id+"F3.wireOp",EDGE,"E19.sketch_text.stroke-2"),sQuery(id+"F3.wireOp",EDGE,"E19.sketch_text.stroke-3"),sQuery(id+"F3.wireOp",EDGE,"E19.sketch_text.stroke-4"),sQuery(id+"F3.wireOp",EDGE,"E19.sketch_text.stroke-5"),sQuery(id+"F3.wireOp",EDGE,"E19.sketch_text.stroke-6"),sQuery(id+"F3.wireOp",EDGE,"E19.sketch_text.stroke-7"),sQuery(id+"F3.wireOp",EDGE,"E19.sketch_text.stroke-8"),sQuery(id+"F3.wireOp",EDGE,"E19.sketch_text.stroke-9"),sQuery(id+"F3.wireOp",EDGE,"E19.sketch_text.stroke-10"),sQuery(id+"F3.wireOp",EDGE,"E19.sketch_text.stroke-11"),sQuery(id+"F3.wireOp",EDGE,"E19.sketch_text.stroke-12"),sQuery(id+"F3.wireOp",EDGE,"E19.sketch_text.stroke-13"),sQuery(id+"F3.wireOp",EDGE,"E19.sketch_text.stroke-14"),sQuery(id+"F3.wireOp",EDGE,"E19.sketch_text.stroke-15"),sQuery(id+"F3.wireOp",EDGE,"E19.sketch_text.stroke-16"),sQuery(id+"F3.wireOp",EDGE,"E19.sketch_text.stroke-17"),sQuery(id+"F3.wireOp",EDGE,"E19.sketch_text.stroke-18"),sQuery(id+"F3.wireOp",EDGE,"E19.sketch_text.stroke-19"),sQuery(id+"F3.wireOp",EDGE,"E19.sketch_text.stroke-20"),sQuery(id+"F3.wireOp",EDGE,"E19.sketch_text.stroke-21"),sQuery(id+"F3.wireOp",EDGE,"E19.sketch_text.stroke-22"),sQuery(id+"F3.wireOp",EDGE,"E19.sketch_text.stroke-23"),sQuery(id+"F3.wireOp",EDGE,"E19.sketch_text.stroke-24"),sQuery(id+"F3.wireOp",EDGE,"E19.sketch_text.stroke-25"),sQuery(id+"F3.wireOp",EDGE,"E20.sketch_text.stroke-0"),sQuery(id+"F3.wireOp",EDGE,"E20.sketch_text.stroke-1"),sQuery(id+"F3.wireOp",EDGE,"E20.sketch_text.stroke-2"),sQuery(id+"F3.wireOp",EDGE,"E20.sketch_text.stroke-3"),sQuery(id+"F3.wireOp",EDGE,"E20.sketch_text.stroke-4"),sQuery(id+"F3.wireOp",EDGE,"E20.sketch_text.stroke-5"),sQuery(id+"F3.wireOp",EDGE,"E20.sketch_text.stroke-6"),sQuery(id+"F3.wireOp",EDGE,"E20.sketch_text.stroke-7"),sQuery(id+"F3.wireOp",EDGE,"E20.sketch_text.stroke-8"),sQuery(id+"F3.wireOp",EDGE,"E20.sketch_text.stroke-9"),sQuery(id+"F3.wireOp",EDGE,"E20.sketch_text.stroke-10"),sQuery(id+"F3.wireOp",EDGE,"E20.sketch_text.stroke-11"),sQuery(id+"F3.wireOp",EDGE,"E20.sketch_text.stroke-12"),sQuery(id+"F3.wireOp",EDGE,"E20.sketch_text.stroke-13"),sQuery(id+"F3.wireOp",EDGE,"E20.sketch_text.stroke-14"),sQuery(id+"F3.wireOp",EDGE,"E20.sketch_text.stroke-15"),sQuery(id+"F3.wireOp",EDGE,"E20.sketch_text.stroke-16")])],"isStart":false})]});
            var Q22;
            Q22=makeQuery(id+"F18.boolean.opBoolean","INTERSECT",EDGE,{"derivedFrom":[makeQuery(id+"F16.opExtrude","SWEPT_FACE",FACE,{"disambiguationData":[OSD([sQuery(id+"F15.wireOp",EDGE,"E103.3")])]}),makeQuery(id+"F18.opExtrude","CAP_FACE",FACE,{"disambiguationData":[OSD([sQuery(id+"F3.wireOp",EDGE,"E0"),sQuery(id+"F3.wireOp",EDGE,"E1"),sQuery(id+"F3.wireOp",EDGE,"E2"),sQuery(id+"F3.wireOp",EDGE,"E3"),sQuery(id+"F3.wireOp",EDGE,"E4"),sQuery(id+"F3.wireOp",EDGE,"E5"),sQuery(id+"F3.wireOp",EDGE,"E6"),sQuery(id+"F3.wireOp",EDGE,"E7"),sQuery(id+"F3.wireOp",EDGE,"E8"),sQuery(id+"F3.wireOp",EDGE,"E9"),sQuery(id+"F3.wireOp",EDGE,"E10"),sQuery(id+"F3.wireOp",EDGE,"E11"),sQuery(id+"F3.wireOp",EDGE,"E12.filletArc"),sQuery(id+"F3.wireOp",EDGE,"E13.filletArc"),sQuery(id+"F3.wireOp",EDGE,"E14.filletArc"),sQuery(id+"F3.wireOp",EDGE,"E15.filletArc"),sQuery(id+"F3.wireOp",EDGE,"E16"),sQuery(id+"F3.wireOp",EDGE,"E17.sketch_text.stroke-0"),sQuery(id+"F3.wireOp",EDGE,"E17.sketch_text.stroke-1"),sQuery(id+"F3.wireOp",EDGE,"E17.sketch_text.stroke-2"),sQuery(id+"F3.wireOp",EDGE,"E17.sketch_text.stroke-3"),sQuery(id+"F3.wireOp",EDGE,"E17.sketch_text.stroke-4"),sQuery(id+"F3.wireOp",EDGE,"E17.sketch_text.stroke-5"),sQuery(id+"F3.wireOp",EDGE,"E17.sketch_text.stroke-6"),sQuery(id+"F3.wireOp",EDGE,"E17.sketch_text.stroke-7"),sQuery(id+"F3.wireOp",EDGE,"E17.sketch_text.stroke-8"),sQuery(id+"F3.wireOp",EDGE,"E17.sketch_text.stroke-9"),sQuery(id+"F3.wireOp",EDGE,"E17.sketch_text.stroke-10"),sQuery(id+"F3.wireOp",EDGE,"E17.sketch_text.stroke-11"),sQuery(id+"F3.wireOp",EDGE,"E17.sketch_text.stroke-12"),sQuery(id+"F3.wireOp",EDGE,"E17.sketch_text.stroke-13"),sQuery(id+"F3.wireOp",EDGE,"E17.sketch_text.stroke-14"),sQuery(id+"F3.wireOp",EDGE,"E17.sketch_text.stroke-15"),sQuery(id+"F3.wireOp",EDGE,"E17.sketch_text.stroke-16"),sQuery(id+"F3.wireOp",EDGE,"E17.sketch_text.stroke-17"),sQuery(id+"F3.wireOp",EDGE,"E17.sketch_text.stroke-18"),sQuery(id+"F3.wireOp",EDGE,"E17.sketch_text.stroke-19"),sQuery(id+"F3.wireOp",EDGE,"E17.sketch_text.stroke-20"),sQuery(id+"F3.wireOp",EDGE,"E17.sketch_text.stroke-21"),sQuery(id+"F3.wireOp",EDGE,"E17.sketch_text.stroke-22"),sQuery(id+"F3.wireOp",EDGE,"E17.sketch_text.stroke-23"),sQuery(id+"F3.wireOp",EDGE,"E17.sketch_text.stroke-24"),sQuery(id+"F3.wireOp",EDGE,"E17.sketch_text.stroke-25"),sQuery(id+"F3.wireOp",EDGE,"E17.sketch_text.stroke-26"),sQuery(id+"F3.wireOp",EDGE,"E17.sketch_text.stroke-27"),sQuery(id+"F3.wireOp",EDGE,"E17.sketch_text.stroke-28"),sQuery(id+"F3.wireOp",EDGE,"E17.sketch_text.stroke-29"),sQuery(id+"F3.wireOp",EDGE,"E17.sketch_text.stroke-30"),sQuery(id+"F3.wireOp",EDGE,"E17.sketch_text.stroke-31"),sQuery(id+"F3.wireOp",EDGE,"E18.sketch_text.stroke-0"),sQuery(id+"F3.wireOp",EDGE,"E18.sketch_text.stroke-1"),sQuery(id+"F3.wireOp",EDGE,"E18.sketch_text.stroke-2"),sQuery(id+"F3.wireOp",EDGE,"E18.sketch_text.stroke-3"),sQuery(id+"F3.wireOp",EDGE,"E18.sketch_text.stroke-4"),sQuery(id+"F3.wireOp",EDGE,"E18.sketch_text.stroke-5"),sQuery(id+"F3.wireOp",EDGE,"E18.sketch_text.stroke-6"),sQuery(id+"F3.wireOp",EDGE,"E18.sketch_text.stroke-7"),sQuery(id+"F3.wireOp",EDGE,"E18.sketch_text.stroke-8"),sQuery(id+"F3.wireOp",EDGE,"E18.sketch_text.stroke-9"),sQuery(id+"F3.wireOp",EDGE,"E18.sketch_text.stroke-10"),sQuery(id+"F3.wireOp",EDGE,"E18.sketch_text.stroke-11"),sQuery(id+"F3.wireOp",EDGE,"E18.sketch_text.stroke-12"),sQuery(id+"F3.wireOp",EDGE,"E18.sketch_text.stroke-13"),sQuery(id+"F3.wireOp",EDGE,"E18.sketch_text.stroke-14"),sQuery(id+"F3.wireOp",EDGE,"E18.sketch_text.stroke-15"),sQuery(id+"F3.wireOp",EDGE,"E18.sketch_text.stroke-16"),sQuery(id+"F3.wireOp",EDGE,"E18.sketch_text.stroke-17"),sQuery(id+"F3.wireOp",EDGE,"E18.sketch_text.stroke-18"),sQuery(id+"F3.wireOp",EDGE,"E18.sketch_text.stroke-19"),sQuery(id+"F3.wireOp",EDGE,"E18.sketch_text.stroke-20"),sQuery(id+"F3.wireOp",EDGE,"E18.sketch_text.stroke-21"),sQuery(id+"F3.wireOp",EDGE,"E18.sketch_text.stroke-22"),sQuery(id+"F3.wireOp",EDGE,"E18.sketch_text.stroke-23"),sQuery(id+"F3.wireOp",EDGE,"E18.sketch_text.stroke-24"),sQuery(id+"F3.wireOp",EDGE,"E18.sketch_text.stroke-25"),sQuery(id+"F3.wireOp",EDGE,"E18.sketch_text.stroke-26"),sQuery(id+"F3.wireOp",EDGE,"E18.sketch_text.stroke-27"),sQuery(id+"F3.wireOp",EDGE,"E19.sketch_text.stroke-0"),sQuery(id+"F3.wireOp",EDGE,"E19.sketch_text.stroke-1"),sQuery(id+"F3.wireOp",EDGE,"E19.sketch_text.stroke-2"),sQuery(id+"F3.wireOp",EDGE,"E19.sketch_text.stroke-3"),sQuery(id+"F3.wireOp",EDGE,"E19.sketch_text.stroke-4"),sQuery(id+"F3.wireOp",EDGE,"E19.sketch_text.stroke-5"),sQuery(id+"F3.wireOp",EDGE,"E19.sketch_text.stroke-6"),sQuery(id+"F3.wireOp",EDGE,"E19.sketch_text.stroke-7"),sQuery(id+"F3.wireOp",EDGE,"E19.sketch_text.stroke-8"),sQuery(id+"F3.wireOp",EDGE,"E19.sketch_text.stroke-9"),sQuery(id+"F3.wireOp",EDGE,"E19.sketch_text.stroke-10"),sQuery(id+"F3.wireOp",EDGE,"E19.sketch_text.stroke-11"),sQuery(id+"F3.wireOp",EDGE,"E19.sketch_text.stroke-12"),sQuery(id+"F3.wireOp",EDGE,"E19.sketch_text.stroke-13"),sQuery(id+"F3.wireOp",EDGE,"E19.sketch_text.stroke-14"),sQuery(id+"F3.wireOp",EDGE,"E19.sketch_text.stroke-15"),sQuery(id+"F3.wireOp",EDGE,"E19.sketch_text.stroke-16"),sQuery(id+"F3.wireOp",EDGE,"E19.sketch_text.stroke-17"),sQuery(id+"F3.wireOp",EDGE,"E19.sketch_text.stroke-18"),sQuery(id+"F3.wireOp",EDGE,"E19.sketch_text.stroke-19"),sQuery(id+"F3.wireOp",EDGE,"E19.sketch_text.stroke-20"),sQuery(id+"F3.wireOp",EDGE,"E19.sketch_text.stroke-21"),sQuery(id+"F3.wireOp",EDGE,"E19.sketch_text.stroke-22"),sQuery(id+"F3.wireOp",EDGE,"E19.sketch_text.stroke-23"),sQuery(id+"F3.wireOp",EDGE,"E19.sketch_text.stroke-24"),sQuery(id+"F3.wireOp",EDGE,"E19.sketch_text.stroke-25"),sQuery(id+"F3.wireOp",EDGE,"E20.sketch_text.stroke-0"),sQuery(id+"F3.wireOp",EDGE,"E20.sketch_text.stroke-1"),sQuery(id+"F3.wireOp",EDGE,"E20.sketch_text.stroke-2"),sQuery(id+"F3.wireOp",EDGE,"E20.sketch_text.stroke-3"),sQuery(id+"F3.wireOp",EDGE,"E20.sketch_text.stroke-4"),sQuery(id+"F3.wireOp",EDGE,"E20.sketch_text.stroke-5"),sQuery(id+"F3.wireOp",EDGE,"E20.sketch_text.stroke-6"),sQuery(id+"F3.wireOp",EDGE,"E20.sketch_text.stroke-7"),sQuery(id+"F3.wireOp",EDGE,"E20.sketch_text.stroke-8"),sQuery(id+"F3.wireOp",EDGE,"E20.sketch_text.stroke-9"),sQuery(id+"F3.wireOp",EDGE,"E20.sketch_text.stroke-10"),sQuery(id+"F3.wireOp",EDGE,"E20.sketch_text.stroke-11"),sQuery(id+"F3.wireOp",EDGE,"E20.sketch_text.stroke-12"),sQuery(id+"F3.wireOp",EDGE,"E20.sketch_text.stroke-13"),sQuery(id+"F3.wireOp",EDGE,"E20.sketch_text.stroke-14"),sQuery(id+"F3.wireOp",EDGE,"E20.sketch_text.stroke-15"),sQuery(id+"F3.wireOp",EDGE,"E20.sketch_text.stroke-16")])],"isStart":false})]});
            var Q23;
            Q23=makeQuery(id+"F18.boolean.opBoolean","INTERSECT",EDGE,{"derivedFrom":[makeQuery(id+"F16.opExtrude","SWEPT_FACE",FACE,{"disambiguationData":[OSD([sQuery(id+"F15.wireOp",EDGE,"E104.1")])]}),makeQuery(id+"F18.opExtrude","CAP_FACE",FACE,{"disambiguationData":[OSD([sQuery(id+"F3.wireOp",EDGE,"E0"),sQuery(id+"F3.wireOp",EDGE,"E1"),sQuery(id+"F3.wireOp",EDGE,"E2"),sQuery(id+"F3.wireOp",EDGE,"E3"),sQuery(id+"F3.wireOp",EDGE,"E4"),sQuery(id+"F3.wireOp",EDGE,"E5"),sQuery(id+"F3.wireOp",EDGE,"E6"),sQuery(id+"F3.wireOp",EDGE,"E7"),sQuery(id+"F3.wireOp",EDGE,"E8"),sQuery(id+"F3.wireOp",EDGE,"E9"),sQuery(id+"F3.wireOp",EDGE,"E10"),sQuery(id+"F3.wireOp",EDGE,"E11"),sQuery(id+"F3.wireOp",EDGE,"E12.filletArc"),sQuery(id+"F3.wireOp",EDGE,"E13.filletArc"),sQuery(id+"F3.wireOp",EDGE,"E14.filletArc"),sQuery(id+"F3.wireOp",EDGE,"E15.filletArc"),sQuery(id+"F3.wireOp",EDGE,"E16"),sQuery(id+"F3.wireOp",EDGE,"E17.sketch_text.stroke-0"),sQuery(id+"F3.wireOp",EDGE,"E17.sketch_text.stroke-1"),sQuery(id+"F3.wireOp",EDGE,"E17.sketch_text.stroke-2"),sQuery(id+"F3.wireOp",EDGE,"E17.sketch_text.stroke-3"),sQuery(id+"F3.wireOp",EDGE,"E17.sketch_text.stroke-4"),sQuery(id+"F3.wireOp",EDGE,"E17.sketch_text.stroke-5"),sQuery(id+"F3.wireOp",EDGE,"E17.sketch_text.stroke-6"),sQuery(id+"F3.wireOp",EDGE,"E17.sketch_text.stroke-7"),sQuery(id+"F3.wireOp",EDGE,"E17.sketch_text.stroke-8"),sQuery(id+"F3.wireOp",EDGE,"E17.sketch_text.stroke-9"),sQuery(id+"F3.wireOp",EDGE,"E17.sketch_text.stroke-10"),sQuery(id+"F3.wireOp",EDGE,"E17.sketch_text.stroke-11"),sQuery(id+"F3.wireOp",EDGE,"E17.sketch_text.stroke-12"),sQuery(id+"F3.wireOp",EDGE,"E17.sketch_text.stroke-13"),sQuery(id+"F3.wireOp",EDGE,"E17.sketch_text.stroke-14"),sQuery(id+"F3.wireOp",EDGE,"E17.sketch_text.stroke-15"),sQuery(id+"F3.wireOp",EDGE,"E17.sketch_text.stroke-16"),sQuery(id+"F3.wireOp",EDGE,"E17.sketch_text.stroke-17"),sQuery(id+"F3.wireOp",EDGE,"E17.sketch_text.stroke-18"),sQuery(id+"F3.wireOp",EDGE,"E17.sketch_text.stroke-19"),sQuery(id+"F3.wireOp",EDGE,"E17.sketch_text.stroke-20"),sQuery(id+"F3.wireOp",EDGE,"E17.sketch_text.stroke-21"),sQuery(id+"F3.wireOp",EDGE,"E17.sketch_text.stroke-22"),sQuery(id+"F3.wireOp",EDGE,"E17.sketch_text.stroke-23"),sQuery(id+"F3.wireOp",EDGE,"E17.sketch_text.stroke-24"),sQuery(id+"F3.wireOp",EDGE,"E17.sketch_text.stroke-25"),sQuery(id+"F3.wireOp",EDGE,"E17.sketch_text.stroke-26"),sQuery(id+"F3.wireOp",EDGE,"E17.sketch_text.stroke-27"),sQuery(id+"F3.wireOp",EDGE,"E17.sketch_text.stroke-28"),sQuery(id+"F3.wireOp",EDGE,"E17.sketch_text.stroke-29"),sQuery(id+"F3.wireOp",EDGE,"E17.sketch_text.stroke-30"),sQuery(id+"F3.wireOp",EDGE,"E17.sketch_text.stroke-31"),sQuery(id+"F3.wireOp",EDGE,"E18.sketch_text.stroke-0"),sQuery(id+"F3.wireOp",EDGE,"E18.sketch_text.stroke-1"),sQuery(id+"F3.wireOp",EDGE,"E18.sketch_text.stroke-2"),sQuery(id+"F3.wireOp",EDGE,"E18.sketch_text.stroke-3"),sQuery(id+"F3.wireOp",EDGE,"E18.sketch_text.stroke-4"),sQuery(id+"F3.wireOp",EDGE,"E18.sketch_text.stroke-5"),sQuery(id+"F3.wireOp",EDGE,"E18.sketch_text.stroke-6"),sQuery(id+"F3.wireOp",EDGE,"E18.sketch_text.stroke-7"),sQuery(id+"F3.wireOp",EDGE,"E18.sketch_text.stroke-8"),sQuery(id+"F3.wireOp",EDGE,"E18.sketch_text.stroke-9"),sQuery(id+"F3.wireOp",EDGE,"E18.sketch_text.stroke-10"),sQuery(id+"F3.wireOp",EDGE,"E18.sketch_text.stroke-11"),sQuery(id+"F3.wireOp",EDGE,"E18.sketch_text.stroke-12"),sQuery(id+"F3.wireOp",EDGE,"E18.sketch_text.stroke-13"),sQuery(id+"F3.wireOp",EDGE,"E18.sketch_text.stroke-14"),sQuery(id+"F3.wireOp",EDGE,"E18.sketch_text.stroke-15"),sQuery(id+"F3.wireOp",EDGE,"E18.sketch_text.stroke-16"),sQuery(id+"F3.wireOp",EDGE,"E18.sketch_text.stroke-17"),sQuery(id+"F3.wireOp",EDGE,"E18.sketch_text.stroke-18"),sQuery(id+"F3.wireOp",EDGE,"E18.sketch_text.stroke-19"),sQuery(id+"F3.wireOp",EDGE,"E18.sketch_text.stroke-20"),sQuery(id+"F3.wireOp",EDGE,"E18.sketch_text.stroke-21"),sQuery(id+"F3.wireOp",EDGE,"E18.sketch_text.stroke-22"),sQuery(id+"F3.wireOp",EDGE,"E18.sketch_text.stroke-23"),sQuery(id+"F3.wireOp",EDGE,"E18.sketch_text.stroke-24"),sQuery(id+"F3.wireOp",EDGE,"E18.sketch_text.stroke-25"),sQuery(id+"F3.wireOp",EDGE,"E18.sketch_text.stroke-26"),sQuery(id+"F3.wireOp",EDGE,"E18.sketch_text.stroke-27"),sQuery(id+"F3.wireOp",EDGE,"E19.sketch_text.stroke-0"),sQuery(id+"F3.wireOp",EDGE,"E19.sketch_text.stroke-1"),sQuery(id+"F3.wireOp",EDGE,"E19.sketch_text.stroke-2"),sQuery(id+"F3.wireOp",EDGE,"E19.sketch_text.stroke-3"),sQuery(id+"F3.wireOp",EDGE,"E19.sketch_text.stroke-4"),sQuery(id+"F3.wireOp",EDGE,"E19.sketch_text.stroke-5"),sQuery(id+"F3.wireOp",EDGE,"E19.sketch_text.stroke-6"),sQuery(id+"F3.wireOp",EDGE,"E19.sketch_text.stroke-7"),sQuery(id+"F3.wireOp",EDGE,"E19.sketch_text.stroke-8"),sQuery(id+"F3.wireOp",EDGE,"E19.sketch_text.stroke-9"),sQuery(id+"F3.wireOp",EDGE,"E19.sketch_text.stroke-10"),sQuery(id+"F3.wireOp",EDGE,"E19.sketch_text.stroke-11"),sQuery(id+"F3.wireOp",EDGE,"E19.sketch_text.stroke-12"),sQuery(id+"F3.wireOp",EDGE,"E19.sketch_text.stroke-13"),sQuery(id+"F3.wireOp",EDGE,"E19.sketch_text.stroke-14"),sQuery(id+"F3.wireOp",EDGE,"E19.sketch_text.stroke-15"),sQuery(id+"F3.wireOp",EDGE,"E19.sketch_text.stroke-16"),sQuery(id+"F3.wireOp",EDGE,"E19.sketch_text.stroke-17"),sQuery(id+"F3.wireOp",EDGE,"E19.sketch_text.stroke-18"),sQuery(id+"F3.wireOp",EDGE,"E19.sketch_text.stroke-19"),sQuery(id+"F3.wireOp",EDGE,"E19.sketch_text.stroke-20"),sQuery(id+"F3.wireOp",EDGE,"E19.sketch_text.stroke-21"),sQuery(id+"F3.wireOp",EDGE,"E19.sketch_text.stroke-22"),sQuery(id+"F3.wireOp",EDGE,"E19.sketch_text.stroke-23"),sQuery(id+"F3.wireOp",EDGE,"E19.sketch_text.stroke-24"),sQuery(id+"F3.wireOp",EDGE,"E19.sketch_text.stroke-25"),sQuery(id+"F3.wireOp",EDGE,"E20.sketch_text.stroke-0"),sQuery(id+"F3.wireOp",EDGE,"E20.sketch_text.stroke-1"),sQuery(id+"F3.wireOp",EDGE,"E20.sketch_text.stroke-2"),sQuery(id+"F3.wireOp",EDGE,"E20.sketch_text.stroke-3"),sQuery(id+"F3.wireOp",EDGE,"E20.sketch_text.stroke-4"),sQuery(id+"F3.wireOp",EDGE,"E20.sketch_text.stroke-5"),sQuery(id+"F3.wireOp",EDGE,"E20.sketch_text.stroke-6"),sQuery(id+"F3.wireOp",EDGE,"E20.sketch_text.stroke-7"),sQuery(id+"F3.wireOp",EDGE,"E20.sketch_text.stroke-8"),sQuery(id+"F3.wireOp",EDGE,"E20.sketch_text.stroke-9"),sQuery(id+"F3.wireOp",EDGE,"E20.sketch_text.stroke-10"),sQuery(id+"F3.wireOp",EDGE,"E20.sketch_text.stroke-11"),sQuery(id+"F3.wireOp",EDGE,"E20.sketch_text.stroke-12"),sQuery(id+"F3.wireOp",EDGE,"E20.sketch_text.stroke-13"),sQuery(id+"F3.wireOp",EDGE,"E20.sketch_text.stroke-14"),sQuery(id+"F3.wireOp",EDGE,"E20.sketch_text.stroke-15"),sQuery(id+"F3.wireOp",EDGE,"E20.sketch_text.stroke-16")])],"isStart":false})]});
            var Q24;
            Q24=makeQuery(id+"F18.boolean.opBoolean","INTERSECT",EDGE,{"derivedFrom":[makeQuery(id+"F16.opExtrude","SWEPT_FACE",FACE,{"disambiguationData":[OSD([sQuery(id+"F15.wireOp",EDGE,"E102.3")])]}),makeQuery(id+"F18.opExtrude","CAP_FACE",FACE,{"disambiguationData":[OSD([sQuery(id+"F3.wireOp",EDGE,"E0"),sQuery(id+"F3.wireOp",EDGE,"E1"),sQuery(id+"F3.wireOp",EDGE,"E2"),sQuery(id+"F3.wireOp",EDGE,"E3"),sQuery(id+"F3.wireOp",EDGE,"E4"),sQuery(id+"F3.wireOp",EDGE,"E5"),sQuery(id+"F3.wireOp",EDGE,"E6"),sQuery(id+"F3.wireOp",EDGE,"E7"),sQuery(id+"F3.wireOp",EDGE,"E8"),sQuery(id+"F3.wireOp",EDGE,"E9"),sQuery(id+"F3.wireOp",EDGE,"E10"),sQuery(id+"F3.wireOp",EDGE,"E11"),sQuery(id+"F3.wireOp",EDGE,"E12.filletArc"),sQuery(id+"F3.wireOp",EDGE,"E13.filletArc"),sQuery(id+"F3.wireOp",EDGE,"E14.filletArc"),sQuery(id+"F3.wireOp",EDGE,"E15.filletArc"),sQuery(id+"F3.wireOp",EDGE,"E16"),sQuery(id+"F3.wireOp",EDGE,"E17.sketch_text.stroke-0"),sQuery(id+"F3.wireOp",EDGE,"E17.sketch_text.stroke-1"),sQuery(id+"F3.wireOp",EDGE,"E17.sketch_text.stroke-2"),sQuery(id+"F3.wireOp",EDGE,"E17.sketch_text.stroke-3"),sQuery(id+"F3.wireOp",EDGE,"E17.sketch_text.stroke-4"),sQuery(id+"F3.wireOp",EDGE,"E17.sketch_text.stroke-5"),sQuery(id+"F3.wireOp",EDGE,"E17.sketch_text.stroke-6"),sQuery(id+"F3.wireOp",EDGE,"E17.sketch_text.stroke-7"),sQuery(id+"F3.wireOp",EDGE,"E17.sketch_text.stroke-8"),sQuery(id+"F3.wireOp",EDGE,"E17.sketch_text.stroke-9"),sQuery(id+"F3.wireOp",EDGE,"E17.sketch_text.stroke-10"),sQuery(id+"F3.wireOp",EDGE,"E17.sketch_text.stroke-11"),sQuery(id+"F3.wireOp",EDGE,"E17.sketch_text.stroke-12"),sQuery(id+"F3.wireOp",EDGE,"E17.sketch_text.stroke-13"),sQuery(id+"F3.wireOp",EDGE,"E17.sketch_text.stroke-14"),sQuery(id+"F3.wireOp",EDGE,"E17.sketch_text.stroke-15"),sQuery(id+"F3.wireOp",EDGE,"E17.sketch_text.stroke-16"),sQuery(id+"F3.wireOp",EDGE,"E17.sketch_text.stroke-17"),sQuery(id+"F3.wireOp",EDGE,"E17.sketch_text.stroke-18"),sQuery(id+"F3.wireOp",EDGE,"E17.sketch_text.stroke-19"),sQuery(id+"F3.wireOp",EDGE,"E17.sketch_text.stroke-20"),sQuery(id+"F3.wireOp",EDGE,"E17.sketch_text.stroke-21"),sQuery(id+"F3.wireOp",EDGE,"E17.sketch_text.stroke-22"),sQuery(id+"F3.wireOp",EDGE,"E17.sketch_text.stroke-23"),sQuery(id+"F3.wireOp",EDGE,"E17.sketch_text.stroke-24"),sQuery(id+"F3.wireOp",EDGE,"E17.sketch_text.stroke-25"),sQuery(id+"F3.wireOp",EDGE,"E17.sketch_text.stroke-26"),sQuery(id+"F3.wireOp",EDGE,"E17.sketch_text.stroke-27"),sQuery(id+"F3.wireOp",EDGE,"E17.sketch_text.stroke-28"),sQuery(id+"F3.wireOp",EDGE,"E17.sketch_text.stroke-29"),sQuery(id+"F3.wireOp",EDGE,"E17.sketch_text.stroke-30"),sQuery(id+"F3.wireOp",EDGE,"E17.sketch_text.stroke-31"),sQuery(id+"F3.wireOp",EDGE,"E18.sketch_text.stroke-0"),sQuery(id+"F3.wireOp",EDGE,"E18.sketch_text.stroke-1"),sQuery(id+"F3.wireOp",EDGE,"E18.sketch_text.stroke-2"),sQuery(id+"F3.wireOp",EDGE,"E18.sketch_text.stroke-3"),sQuery(id+"F3.wireOp",EDGE,"E18.sketch_text.stroke-4"),sQuery(id+"F3.wireOp",EDGE,"E18.sketch_text.stroke-5"),sQuery(id+"F3.wireOp",EDGE,"E18.sketch_text.stroke-6"),sQuery(id+"F3.wireOp",EDGE,"E18.sketch_text.stroke-7"),sQuery(id+"F3.wireOp",EDGE,"E18.sketch_text.stroke-8"),sQuery(id+"F3.wireOp",EDGE,"E18.sketch_text.stroke-9"),sQuery(id+"F3.wireOp",EDGE,"E18.sketch_text.stroke-10"),sQuery(id+"F3.wireOp",EDGE,"E18.sketch_text.stroke-11"),sQuery(id+"F3.wireOp",EDGE,"E18.sketch_text.stroke-12"),sQuery(id+"F3.wireOp",EDGE,"E18.sketch_text.stroke-13"),sQuery(id+"F3.wireOp",EDGE,"E18.sketch_text.stroke-14"),sQuery(id+"F3.wireOp",EDGE,"E18.sketch_text.stroke-15"),sQuery(id+"F3.wireOp",EDGE,"E18.sketch_text.stroke-16"),sQuery(id+"F3.wireOp",EDGE,"E18.sketch_text.stroke-17"),sQuery(id+"F3.wireOp",EDGE,"E18.sketch_text.stroke-18"),sQuery(id+"F3.wireOp",EDGE,"E18.sketch_text.stroke-19"),sQuery(id+"F3.wireOp",EDGE,"E18.sketch_text.stroke-20"),sQuery(id+"F3.wireOp",EDGE,"E18.sketch_text.stroke-21"),sQuery(id+"F3.wireOp",EDGE,"E18.sketch_text.stroke-22"),sQuery(id+"F3.wireOp",EDGE,"E18.sketch_text.stroke-23"),sQuery(id+"F3.wireOp",EDGE,"E18.sketch_text.stroke-24"),sQuery(id+"F3.wireOp",EDGE,"E18.sketch_text.stroke-25"),sQuery(id+"F3.wireOp",EDGE,"E18.sketch_text.stroke-26"),sQuery(id+"F3.wireOp",EDGE,"E18.sketch_text.stroke-27"),sQuery(id+"F3.wireOp",EDGE,"E19.sketch_text.stroke-0"),sQuery(id+"F3.wireOp",EDGE,"E19.sketch_text.stroke-1"),sQuery(id+"F3.wireOp",EDGE,"E19.sketch_text.stroke-2"),sQuery(id+"F3.wireOp",EDGE,"E19.sketch_text.stroke-3"),sQuery(id+"F3.wireOp",EDGE,"E19.sketch_text.stroke-4"),sQuery(id+"F3.wireOp",EDGE,"E19.sketch_text.stroke-5"),sQuery(id+"F3.wireOp",EDGE,"E19.sketch_text.stroke-6"),sQuery(id+"F3.wireOp",EDGE,"E19.sketch_text.stroke-7"),sQuery(id+"F3.wireOp",EDGE,"E19.sketch_text.stroke-8"),sQuery(id+"F3.wireOp",EDGE,"E19.sketch_text.stroke-9"),sQuery(id+"F3.wireOp",EDGE,"E19.sketch_text.stroke-10"),sQuery(id+"F3.wireOp",EDGE,"E19.sketch_text.stroke-11"),sQuery(id+"F3.wireOp",EDGE,"E19.sketch_text.stroke-12"),sQuery(id+"F3.wireOp",EDGE,"E19.sketch_text.stroke-13"),sQuery(id+"F3.wireOp",EDGE,"E19.sketch_text.stroke-14"),sQuery(id+"F3.wireOp",EDGE,"E19.sketch_text.stroke-15"),sQuery(id+"F3.wireOp",EDGE,"E19.sketch_text.stroke-16"),sQuery(id+"F3.wireOp",EDGE,"E19.sketch_text.stroke-17"),sQuery(id+"F3.wireOp",EDGE,"E19.sketch_text.stroke-18"),sQuery(id+"F3.wireOp",EDGE,"E19.sketch_text.stroke-19"),sQuery(id+"F3.wireOp",EDGE,"E19.sketch_text.stroke-20"),sQuery(id+"F3.wireOp",EDGE,"E19.sketch_text.stroke-21"),sQuery(id+"F3.wireOp",EDGE,"E19.sketch_text.stroke-22"),sQuery(id+"F3.wireOp",EDGE,"E19.sketch_text.stroke-23"),sQuery(id+"F3.wireOp",EDGE,"E19.sketch_text.stroke-24"),sQuery(id+"F3.wireOp",EDGE,"E19.sketch_text.stroke-25"),sQuery(id+"F3.wireOp",EDGE,"E20.sketch_text.stroke-0"),sQuery(id+"F3.wireOp",EDGE,"E20.sketch_text.stroke-1"),sQuery(id+"F3.wireOp",EDGE,"E20.sketch_text.stroke-2"),sQuery(id+"F3.wireOp",EDGE,"E20.sketch_text.stroke-3"),sQuery(id+"F3.wireOp",EDGE,"E20.sketch_text.stroke-4"),sQuery(id+"F3.wireOp",EDGE,"E20.sketch_text.stroke-5"),sQuery(id+"F3.wireOp",EDGE,"E20.sketch_text.stroke-6"),sQuery(id+"F3.wireOp",EDGE,"E20.sketch_text.stroke-7"),sQuery(id+"F3.wireOp",EDGE,"E20.sketch_text.stroke-8"),sQuery(id+"F3.wireOp",EDGE,"E20.sketch_text.stroke-9"),sQuery(id+"F3.wireOp",EDGE,"E20.sketch_text.stroke-10"),sQuery(id+"F3.wireOp",EDGE,"E20.sketch_text.stroke-11"),sQuery(id+"F3.wireOp",EDGE,"E20.sketch_text.stroke-12"),sQuery(id+"F3.wireOp",EDGE,"E20.sketch_text.stroke-13"),sQuery(id+"F3.wireOp",EDGE,"E20.sketch_text.stroke-14"),sQuery(id+"F3.wireOp",EDGE,"E20.sketch_text.stroke-15"),sQuery(id+"F3.wireOp",EDGE,"E20.sketch_text.stroke-16")])],"isStart":false})]});
            var Q25;
            Q25=makeQuery(id+"F16.opExtrude","CAP_FACE",FACE,{"disambiguationData":[OSD([sQuery(id+"F15.wireOp",EDGE,"E94.0"),sQuery(id+"F15.wireOp",EDGE,"E94.1"),sQuery(id+"F15.wireOp",EDGE,"E94.2"),sQuery(id+"F15.wireOp",EDGE,"E94.3"),sQuery(id+"F15.wireOp",EDGE,"E94.4"),sQuery(id+"F15.wireOp",EDGE,"E94.5"),sQuery(id+"F15.wireOp",EDGE,"E94.6"),sQuery(id+"F15.wireOp",EDGE,"E94.7"),sQuery(id+"F15.wireOp",EDGE,"E94.8"),sQuery(id+"F15.wireOp",EDGE,"E94.9"),sQuery(id+"F15.wireOp",EDGE,"E94.10"),sQuery(id+"F15.wireOp",EDGE,"E94.11"),sQuery(id+"F15.wireOp",EDGE,"E94.12"),sQuery(id+"F15.wireOp",EDGE,"E94.13"),sQuery(id+"F15.wireOp",EDGE,"E94.14"),sQuery(id+"F15.wireOp",EDGE,"E94.15"),sQuery(id+"F15.wireOp",EDGE,"E95.0"),sQuery(id+"F15.wireOp",EDGE,"E96.trimOffspring"),sQuery(id+"F15.wireOp",EDGE,"E98.trimOffspring"),sQuery(id+"F15.wireOp",EDGE,"E100.trimOffspring"),sQuery(id+"F15.wireOp",EDGE,"E102.0"),sQuery(id+"F15.wireOp",EDGE,"E102.1"),sQuery(id+"F15.wireOp",EDGE,"E102.2"),sQuery(id+"F15.wireOp",EDGE,"E102.3"),sQuery(id+"F15.wireOp",EDGE,"E102.4"),sQuery(id+"F15.wireOp",EDGE,"E103.0"),sQuery(id+"F15.wireOp",EDGE,"E103.2"),sQuery(id+"F15.wireOp",EDGE,"E103.3"),sQuery(id+"F15.wireOp",EDGE,"E103.4"),sQuery(id+"F15.wireOp",EDGE,"E104.0"),sQuery(id+"F15.wireOp",EDGE,"E104.1"),sQuery(id+"F15.wireOp",EDGE,"E104.2"),sQuery(id+"F15.wireOp",EDGE,"E105.0"),sQuery(id+"F15.wireOp",EDGE,"E105.1"),sQuery(id+"F15.wireOp",EDGE,"E105.2"),sQuery(id+"F15.wireOp",EDGE,"E105.3")])],"isStart":false});
            chamfer(context, id + "F36", {"entities" : qUnion([Q0, Q1, Q2, Q3, Q4, Q5, Q6, Q7, Q8, Q9, Q10, Q11, Q12, Q13, Q14, Q15, Q16, Q17, Q18, Q19, Q20, Q21, Q22, Q23, Q24, Q25]), "width" : 1 * mm, "tangentPropagation" : true});
        }
        {
            var Q0;
            Q0=makeQuery(id+"F16.opExtrude","CAP_FACE",FACE,{"disambiguationData":[OSD([sQuery(id+"F15.wireOp",EDGE,"E94.0"),sQuery(id+"F15.wireOp",EDGE,"E94.1"),sQuery(id+"F15.wireOp",EDGE,"E94.2"),sQuery(id+"F15.wireOp",EDGE,"E94.3"),sQuery(id+"F15.wireOp",EDGE,"E94.4"),sQuery(id+"F15.wireOp",EDGE,"E94.5"),sQuery(id+"F15.wireOp",EDGE,"E94.6"),sQuery(id+"F15.wireOp",EDGE,"E94.7"),sQuery(id+"F15.wireOp",EDGE,"E94.8"),sQuery(id+"F15.wireOp",EDGE,"E94.9"),sQuery(id+"F15.wireOp",EDGE,"E94.10"),sQuery(id+"F15.wireOp",EDGE,"E94.11"),sQuery(id+"F15.wireOp",EDGE,"E94.12"),sQuery(id+"F15.wireOp",EDGE,"E94.13"),sQuery(id+"F15.wireOp",EDGE,"E94.14"),sQuery(id+"F15.wireOp",EDGE,"E94.15"),sQuery(id+"F15.wireOp",EDGE,"E95.0"),sQuery(id+"F15.wireOp",EDGE,"E96.trimOffspring"),sQuery(id+"F15.wireOp",EDGE,"E98.trimOffspring"),sQuery(id+"F15.wireOp",EDGE,"E100.trimOffspring"),sQuery(id+"F15.wireOp",EDGE,"E102.0"),sQuery(id+"F15.wireOp",EDGE,"E102.1"),sQuery(id+"F15.wireOp",EDGE,"E102.2"),sQuery(id+"F15.wireOp",EDGE,"E102.3"),sQuery(id+"F15.wireOp",EDGE,"E102.4"),sQuery(id+"F15.wireOp",EDGE,"E103.0"),sQuery(id+"F15.wireOp",EDGE,"E103.2"),sQuery(id+"F15.wireOp",EDGE,"E103.3"),sQuery(id+"F15.wireOp",EDGE,"E103.4"),sQuery(id+"F15.wireOp",EDGE,"E104.0"),sQuery(id+"F15.wireOp",EDGE,"E104.1"),sQuery(id+"F15.wireOp",EDGE,"E104.2"),sQuery(id+"F15.wireOp",EDGE,"E105.0"),sQuery(id+"F15.wireOp",EDGE,"E105.1"),sQuery(id+"F15.wireOp",EDGE,"E105.2"),sQuery(id+"F15.wireOp",EDGE,"E105.3")])],"isStart":false});
            var sketch = newSketch(context, id + "F37", { "sketchPlane" : qUnion([Q0])});
            skLineSegment(sketch, "E163", {"start": v(5.93, -23.56) * mm, "end": v(9.4, -17.54) * mm});
            skLineSegment(sketch, "E164", {"start": v(-4.76, -23.56) * mm, "end": v(5.93, -23.56) * mm});
            skLineSegment(sketch, "E165", {"start": v(25, -19.86) * mm, "end": v(25, -0.4) * mm});
            skLineSegment(sketch, "E166", {"start": v(22.22, -21.25) * mm, "end": v(25, -19.86) * mm});
            skLineSegment(sketch, "E167", {"start": v(22.22, -3.19) * mm, "end": v(22.22, -21.25) * mm});
            skLineSegment(sketch, "E168", {"start": v(-13.89, -3.19) * mm, "end": v(22.22, -3.19) * mm});
            skLineSegment(sketch, "E169", {"start": v(-8.33, -0.4) * mm, "end": v(-13.89, -3.19) * mm});
            skLineSegment(sketch, "E170", {"start": v(25, -0.4) * mm, "end": v(-8.33, -0.4) * mm});
            skLineSegment(sketch, "E171", {"start": v(-13.85, -11.52) * mm, "end": v(-17.6, -11.52) * mm});
            skLineSegment(sketch, "E172", {"start": v(-11.71, -7.82) * mm, "end": v(-13.85, -11.52) * mm});
            skLineSegment(sketch, "E173", {"start": v(-17.6, -7.82) * mm, "end": v(-11.71, -7.82) * mm});
            skLineSegment(sketch, "E174", {"start": v(-20.37, -7.82) * mm, "end": v(-17.6, -7.82) * mm});
            skLineSegment(sketch, "E175", {"start": v(-20.37, -6.43) * mm, "end": v(-20.37, -7.82) * mm});
            skLineSegment(sketch, "E176", {"start": v(-17.6, -5.04) * mm, "end": v(-20.37, -6.43) * mm});
            skLineSegment(sketch, "E177", {"start": v(-3.16, -7.82) * mm, "end": v(4.33, -7.82) * mm});
            skLineSegment(sketch, "E178", {"start": v(4.33, -7.82) * mm, "end": v(6.2, -11.06) * mm});
            skLineSegment(sketch, "E179", {"start": v(6.2, -11.06) * mm, "end": v(9.4, -11.06) * mm});
            skLineSegment(sketch, "E180", {"start": v(9.4, -11.06) * mm, "end": v(5.93, -5.04) * mm});
            skLineSegment(sketch, "E181", {"start": v(5.93, -5.04) * mm, "end": v(-4.76, -5.04) * mm});
            skLineSegment(sketch, "E182", {"start": v(-4.76, -5.04) * mm, "end": v(-10.1, -14.3) * mm});
            skLineSegment(sketch, "E183", {"start": v(-10.1, -14.3) * mm, "end": v(-4.76, -23.56) * mm});
            skLineSegment(sketch, "E184", {"start": v(13.23, -7.82) * mm, "end": v(13.23, -20.78) * mm});
            skLineSegment(sketch, "E185", {"start": v(13.23, -20.78) * mm, "end": v(9.68, -20.78) * mm});
            skLineSegment(sketch, "E186", {"start": v(-25, -28.2) * mm, "end": v(8.33, -28.2) * mm});
            skLineSegment(sketch, "E187", {"start": v(9.68, -20.78) * mm, "end": v(8.07, -23.56) * mm});
            skLineSegment(sketch, "E188", {"start": v(8.33, -28.2) * mm, "end": v(13.89, -25.41) * mm});
            skLineSegment(sketch, "E189", {"start": v(8.07, -23.56) * mm, "end": v(17.6, -23.56) * mm});
            skLineSegment(sketch, "E190", {"start": v(13.89, -25.41) * mm, "end": v(-22.22, -25.41) * mm});
            skLineSegment(sketch, "E191", {"start": v(20.37, -7.82) * mm, "end": v(20.37, -5.04) * mm});
            skLineSegment(sketch, "E192", {"start": v(-20.37, -23.56) * mm, "end": v(-17.6, -23.56) * mm});
            skLineSegment(sketch, "E193", {"start": v(20.37, -5.04) * mm, "end": v(8.07, -5.04) * mm});
            skLineSegment(sketch, "E194", {"start": v(-17.6, -23.56) * mm, "end": v(-17.6, -15.53) * mm});
            skLineSegment(sketch, "E195", {"start": v(8.07, -5.04) * mm, "end": v(9.68, -7.82) * mm});
            skLineSegment(sketch, "E196", {"start": v(-17.6, -15.53) * mm, "end": v(-16.88, -14.3) * mm});
            skLineSegment(sketch, "E197", {"start": v(9.68, -7.82) * mm, "end": v(13.23, -7.82) * mm});
            skLineSegment(sketch, "E198", {"start": v(-16.88, -14.3) * mm, "end": v(-15.45, -14.3) * mm});
            skLineSegment(sketch, "E199", {"start": v(16.01, -7.82) * mm, "end": v(20.37, -7.82) * mm});
            skLineSegment(sketch, "E200", {"start": v(-20.37, -14.8) * mm, "end": v(-20.37, -23.56) * mm});
            skLineSegment(sketch, "E201", {"start": v(-18.48, -11.52) * mm, "end": v(-20.37, -14.8) * mm});
            skLineSegment(sketch, "E202", {"start": v(16.01, -20.78) * mm, "end": v(16.01, -7.82) * mm});
            skLineSegment(sketch, "E203", {"start": v(-17.6, -11.52) * mm, "end": v(-18.48, -11.52) * mm});
            skLineSegment(sketch, "E204", {"start": v(20.37, -20.78) * mm, "end": v(16.01, -20.78) * mm});
            skLineSegment(sketch, "E205", {"start": v(-25, -8.74) * mm, "end": v(-25, -28.2) * mm});
            skLineSegment(sketch, "E206", {"start": v(20.37, -22.17) * mm, "end": v(20.37, -20.78) * mm});
            skLineSegment(sketch, "E207", {"start": v(-22.22, -7.35) * mm, "end": v(-25, -8.74) * mm});
            skLineSegment(sketch, "E208", {"start": v(17.6, -23.56) * mm, "end": v(20.37, -22.17) * mm});
            skLineSegment(sketch, "E209", {"start": v(-22.22, -25.41) * mm, "end": v(-22.22, -7.35) * mm});
            skLineSegment(sketch, "E210", {"start": v(-6.9, -14.3) * mm, "end": v(-3.16, -7.82) * mm});
            skLineSegment(sketch, "E211", {"start": v(-3.16, -20.78) * mm, "end": v(-6.9, -14.3) * mm});
            skLineSegment(sketch, "E212", {"start": v(4.33, -20.78) * mm, "end": v(-3.16, -20.78) * mm});
            skLineSegment(sketch, "E213", {"start": v(6.2, -17.54) * mm, "end": v(4.33, -20.78) * mm});
            skLineSegment(sketch, "E214", {"start": v(9.4, -17.54) * mm, "end": v(6.2, -17.54) * mm});
            skLineSegment(sketch, "E215", {"start": v(-15.45, -14.3) * mm, "end": v(-10.1, -23.56) * mm});
            skLineSegment(sketch, "E216", {"start": v(-10.1, -23.56) * mm, "end": v(-6.9, -23.56) * mm});
            skLineSegment(sketch, "E217", {"start": v(-6.9, -23.56) * mm, "end": v(-12.24, -14.3) * mm});
            skLineSegment(sketch, "E218", {"start": v(-12.24, -14.3) * mm, "end": v(-8.02, -6.98) * mm});
            skLineSegment(sketch, "E219", {"start": v(-8.02, -6.98) * mm, "end": v(-6.9, -5.04) * mm});
            skLineSegment(sketch, "E220", {"start": v(-6.9, -5.04) * mm, "end": v(-17.6, -5.04) * mm});
            skLineSegment(sketch, "E221.0", {"start": v(-24.4, -9.11) * mm, "end": v(-24.4, -27.6) * mm});
            skLineSegment(sketch, "E221.1", {"start": v(8.19, -27.6) * mm, "end": v(11.35, -26.01) * mm});
            skLineSegment(sketch, "E221.2", {"start": v(11.35, -26.01) * mm, "end": v(-22.82, -26.01) * mm});
            skLineSegment(sketch, "E221.3", {"start": v(-24.4, -27.6) * mm, "end": v(8.19, -27.6) * mm});
            skLineSegment(sketch, "E221.4", {"start": v(-22.82, -26.01) * mm, "end": v(-22.82, -8.32) * mm});
            skLineSegment(sketch, "E221.5", {"start": v(-22.82, -8.32) * mm, "end": v(-24.4, -9.11) * mm});
            skLineSegment(sketch, "E222.0", {"start": v(-15.1, -13.7) * mm, "end": v(-9.76, -22.96) * mm});
            skLineSegment(sketch, "E222.1", {"start": v(-17.23, -13.7) * mm, "end": v(-15.1, -13.7) * mm});
            skLineSegment(sketch, "E222.2", {"start": v(-18.2, -15.37) * mm, "end": v(-17.23, -13.7) * mm});
            skLineSegment(sketch, "E222.3", {"start": v(-18.2, -22.96) * mm, "end": v(-18.2, -15.37) * mm});
            skLineSegment(sketch, "E222.4", {"start": v(-19.77, -22.96) * mm, "end": v(-18.2, -22.96) * mm});
            skLineSegment(sketch, "E222.5", {"start": v(-9.76, -22.96) * mm, "end": v(-7.94, -22.96) * mm});
            skLineSegment(sketch, "E222.6", {"start": v(-19.77, -14.95) * mm, "end": v(-19.77, -22.96) * mm});
            skLineSegment(sketch, "E222.7", {"start": v(-18.14, -12.12) * mm, "end": v(-19.77, -14.95) * mm});
            skLineSegment(sketch, "E222.8", {"start": v(-17.6, -12.12) * mm, "end": v(-18.14, -12.12) * mm});
            skLineSegment(sketch, "E222.9", {"start": v(-7.94, -5.64) * mm, "end": v(-17.45, -5.64) * mm});
            skLineSegment(sketch, "E222.10", {"start": v(-8.54, -6.68) * mm, "end": v(-7.94, -5.64) * mm});
            skLineSegment(sketch, "E222.11", {"start": v(-12.94, -14.3) * mm, "end": v(-8.54, -6.68) * mm});
            skLineSegment(sketch, "E222.12", {"start": v(-7.94, -22.96) * mm, "end": v(-12.94, -14.3) * mm});
            skLineSegment(sketch, "E222.13", {"start": v(-17.45, -5.64) * mm, "end": v(-19.77, -6.8) * mm});
            skLineSegment(sketch, "E222.14", {"start": v(-19.77, -6.8) * mm, "end": v(-19.77, -7.22) * mm});
            skLineSegment(sketch, "E222.15", {"start": v(-19.77, -7.22) * mm, "end": v(-17.6, -7.22) * mm});
            skLineSegment(sketch, "E222.16", {"start": v(-17.6, -7.22) * mm, "end": v(-10.67, -7.22) * mm});
            skLineSegment(sketch, "E222.17", {"start": v(-10.67, -7.22) * mm, "end": v(-13.5, -12.12) * mm});
            skLineSegment(sketch, "E222.18", {"start": v(-13.5, -12.12) * mm, "end": v(-17.6, -12.12) * mm});
            skLineSegment(sketch, "E223.0", {"start": v(-9.41, -14.3) * mm, "end": v(-4.41, -22.96) * mm});
            skLineSegment(sketch, "E223.1", {"start": v(-4.41, -5.64) * mm, "end": v(-9.41, -14.3) * mm});
            skLineSegment(sketch, "E223.2", {"start": v(5.59, -5.64) * mm, "end": v(-4.41, -5.64) * mm});
            skLineSegment(sketch, "E223.3", {"start": v(4.68, -21.38) * mm, "end": v(-3.5, -21.38) * mm});
            skLineSegment(sketch, "E223.4", {"start": v(6.55, -18.14) * mm, "end": v(4.68, -21.38) * mm});
            skLineSegment(sketch, "E223.5", {"start": v(8.37, -18.14) * mm, "end": v(6.55, -18.14) * mm});
            skLineSegment(sketch, "E223.6", {"start": v(5.59, -22.96) * mm, "end": v(8.37, -18.14) * mm});
            skLineSegment(sketch, "E223.7", {"start": v(-3.5, -21.38) * mm, "end": v(-7.6, -14.3) * mm});
            skLineSegment(sketch, "E223.8", {"start": v(-7.6, -14.3) * mm, "end": v(-3.5, -7.22) * mm});
            skLineSegment(sketch, "E223.9", {"start": v(-3.5, -7.22) * mm, "end": v(4.68, -7.22) * mm});
            skLineSegment(sketch, "E223.10", {"start": v(-4.41, -22.96) * mm, "end": v(5.59, -22.96) * mm});
            skLineSegment(sketch, "E223.11", {"start": v(4.68, -7.22) * mm, "end": v(6.55, -10.46) * mm});
            skLineSegment(sketch, "E223.12", {"start": v(6.55, -10.46) * mm, "end": v(8.37, -10.46) * mm});
            skLineSegment(sketch, "E223.13", {"start": v(8.37, -10.46) * mm, "end": v(5.59, -5.64) * mm});
            skLineSegment(sketch, "E224.0", {"start": v(10.02, -21.38) * mm, "end": v(9.11, -22.96) * mm});
            skLineSegment(sketch, "E224.1", {"start": v(13.83, -21.38) * mm, "end": v(10.02, -21.38) * mm});
            skLineSegment(sketch, "E224.2", {"start": v(15.41, -21.38) * mm, "end": v(15.41, -7.22) * mm});
            skLineSegment(sketch, "E224.3", {"start": v(19.77, -21.38) * mm, "end": v(15.41, -21.38) * mm});
            skLineSegment(sketch, "E224.4", {"start": v(19.77, -21.8) * mm, "end": v(19.77, -21.38) * mm});
            skLineSegment(sketch, "E224.5", {"start": v(17.45, -22.96) * mm, "end": v(19.77, -21.8) * mm});
            skLineSegment(sketch, "E224.6", {"start": v(15.41, -7.22) * mm, "end": v(19.77, -7.22) * mm});
            skLineSegment(sketch, "E224.7", {"start": v(19.77, -7.22) * mm, "end": v(19.77, -5.64) * mm});
            skLineSegment(sketch, "E224.8", {"start": v(9.11, -22.96) * mm, "end": v(17.45, -22.96) * mm});
            skLineSegment(sketch, "E224.9", {"start": v(19.77, -5.64) * mm, "end": v(9.11, -5.64) * mm});
            skLineSegment(sketch, "E224.10", {"start": v(9.11, -5.64) * mm, "end": v(10.02, -7.22) * mm});
            skLineSegment(sketch, "E224.11", {"start": v(10.02, -7.22) * mm, "end": v(13.83, -7.22) * mm});
            skLineSegment(sketch, "E224.12", {"start": v(13.83, -7.22) * mm, "end": v(13.83, -21.38) * mm});
            skLineSegment(sketch, "E225.0", {"start": v(-8.19, -1) * mm, "end": v(-11.35, -2.59) * mm});
            skLineSegment(sketch, "E225.1", {"start": v(22.82, -2.59) * mm, "end": v(22.82, -20.27) * mm});
            skLineSegment(sketch, "E225.2", {"start": v(22.82, -20.27) * mm, "end": v(24.4, -19.49) * mm});
            skLineSegment(sketch, "E225.3", {"start": v(-11.35, -2.59) * mm, "end": v(22.82, -2.59) * mm});
            skLineSegment(sketch, "E225.4", {"start": v(24.4, -19.49) * mm, "end": v(24.4, -1) * mm});
            skLineSegment(sketch, "E225.5", {"start": v(24.4, -1) * mm, "end": v(-8.19, -1) * mm});
            skSolve(sketch);
        }
        {
            var Q0;
            Q0=makeQuery(id+"F37.imprint","IMPRINT",FACE,{"disambiguationData":[TD([[makeQuery(id+"F37.imprint","IMPRINT",EDGE,{"derivedFrom":sQuery(id+"F37.wireOp",EDGE,"E163")}),-1.0]])]});
            var sketch = newSketch(context, id + "F38", { "sketchPlane" : qUnion([Q0])});
            skLineSegment(sketch, "E226", {"start": v(-16.3, 22.59) * mm, "end": v(-18.06, 21.57) * mm});
            skArc(sketch, "E227", {"start": v(25, 23.6) * mm, "mid": v(19.37, 26.1) * mm, "end": v(13.5, 27.93) * mm});
            skLineSegment(sketch, "E228", {"start": v(-16.3, 24.63) * mm, "end": v(-16.3, 22.59) * mm});
            skArc(sketch, "E229", {"start": v(8.47, 28.95) * mm, "mid": v(-4.01, 29.46) * mm, "end": v(-16.3, 27.15) * mm});
            skArc(sketch, "E230", {"start": v(-18.06, 25.65) * mm, "mid": v(-21.68, 25.13) * mm, "end": v(-25, 23.6) * mm});
            skArc(sketch, "E231", {"start": v(-25, 23.6) * mm, "mid": v(-21.68, 22.09) * mm, "end": v(-18.06, 21.57) * mm});
            skLineSegment(sketch, "E232", {"start": v(-18.06, 25.65) * mm, "end": v(-16.3, 24.63) * mm});
            skEllipticalArc(sketch, "E233", {});
            skArc(sketch, "E234", {"start": v(-16.3, 20.07) * mm, "mid": v(-13.53, 23.6) * mm, "end": v(-16.3, 27.15) * mm});
            skArc(sketch, "E235", {"start": v(-16.3, 20.07) * mm, "mid": v(4.7, 17.8) * mm, "end": v(25, 23.6) * mm});
            skLineSegment(sketch, "E236", {"start": v(-25, 23.6) * mm, "end": v(25, 23.6) * mm, "construction": true});
            skPoint(sketch, "E237", {"position": v(0, 23.6) * mm});
            const initialGuessF38  = {"E233": [0.010632281256341334, 0.026623014023974587, 0.9786970439861687, -0.205309756447996, 0.00383333788222767, 0.0024962586673014982, 2.313906, 0.8451846928204219]};
            skSetInitialGuess(sketch, initialGuessF38);
            skSolve(sketch);
        }
        {
            var Q0;
            Q0=makeQuery(id+"F38.imprint","IMPRINT",FACE,{"disambiguationData":[TD([[makeQuery(id+"F38.imprint","IMPRINT",EDGE,{"derivedFrom":makeQuery(id+"F37.imprint","IMPRINT",EDGE,{"derivedFrom":sQuery(id+"F37.wireOp",EDGE,"E186")})}),1.0]])]});
            var Q1;
            Q1=makeQuery(id+"F38.imprint","IMPRINT",FACE,{"disambiguationData":[TD([[makeQuery(id+"F38.imprint","IMPRINT",EDGE,{"derivedFrom":makeQuery(id+"F37.imprint","IMPRINT",EDGE,{"derivedFrom":sQuery(id+"F37.wireOp",EDGE,"E171")})}),1.0]])]});
            var Q2;
            Q2=makeQuery(id+"F38.imprint","IMPRINT",FACE,{"disambiguationData":[TD([[makeQuery(id+"F38.imprint","IMPRINT",EDGE,{"derivedFrom":makeQuery(id+"F37.imprint","IMPRINT",EDGE,{"derivedFrom":sQuery(id+"F37.wireOp",EDGE,"E163")})}),1.0]])]});
            var Q3;
            Q3=makeQuery(id+"F38.imprint","IMPRINT",FACE,{"disambiguationData":[TD([[makeQuery(id+"F38.imprint","IMPRINT",EDGE,{"derivedFrom":makeQuery(id+"F37.imprint","IMPRINT",EDGE,{"derivedFrom":sQuery(id+"F37.wireOp",EDGE,"E184")})}),1.0]])]});
            var Q4;
            Q4=makeQuery(id+"F38.imprint","IMPRINT",FACE,{"disambiguationData":[TD([[makeQuery(id+"F38.imprint","IMPRINT",EDGE,{"derivedFrom":makeQuery(id+"F37.imprint","IMPRINT",EDGE,{"derivedFrom":sQuery(id+"F37.wireOp",EDGE,"E165")})}),1.0]])]});
            var Q5;
            Q5=makeQuery(id+"F38.imprint","IMPRINT",FACE,{"disambiguationData":[TD([[makeQuery(id+"F38.imprint","IMPRINT",EDGE,{"derivedFrom":sQuery(id+"F38.wireOp",EDGE,"E227")}),1.0]])]});
            var Q6;
            Q6=makeQuery(id+"F38.imprint","IMPRINT",FACE,{"disambiguationData":[TD([[makeQuery(id+"F38.imprint","IMPRINT",EDGE,{"derivedFrom":sQuery(id+"F38.wireOp",EDGE,"E226")}),-1.0]])]});
            extrude(context, id + "F39", {"entities" : qUnion([Q0, Q1, Q2, Q3, Q4, Q5, Q6]), "operationType" : NewBodyOperationType.REMOVE, "oppositeDirection" : true, "depth" : 1 * mm, "offsetDistance" : 25 * mm});
        }
    });
